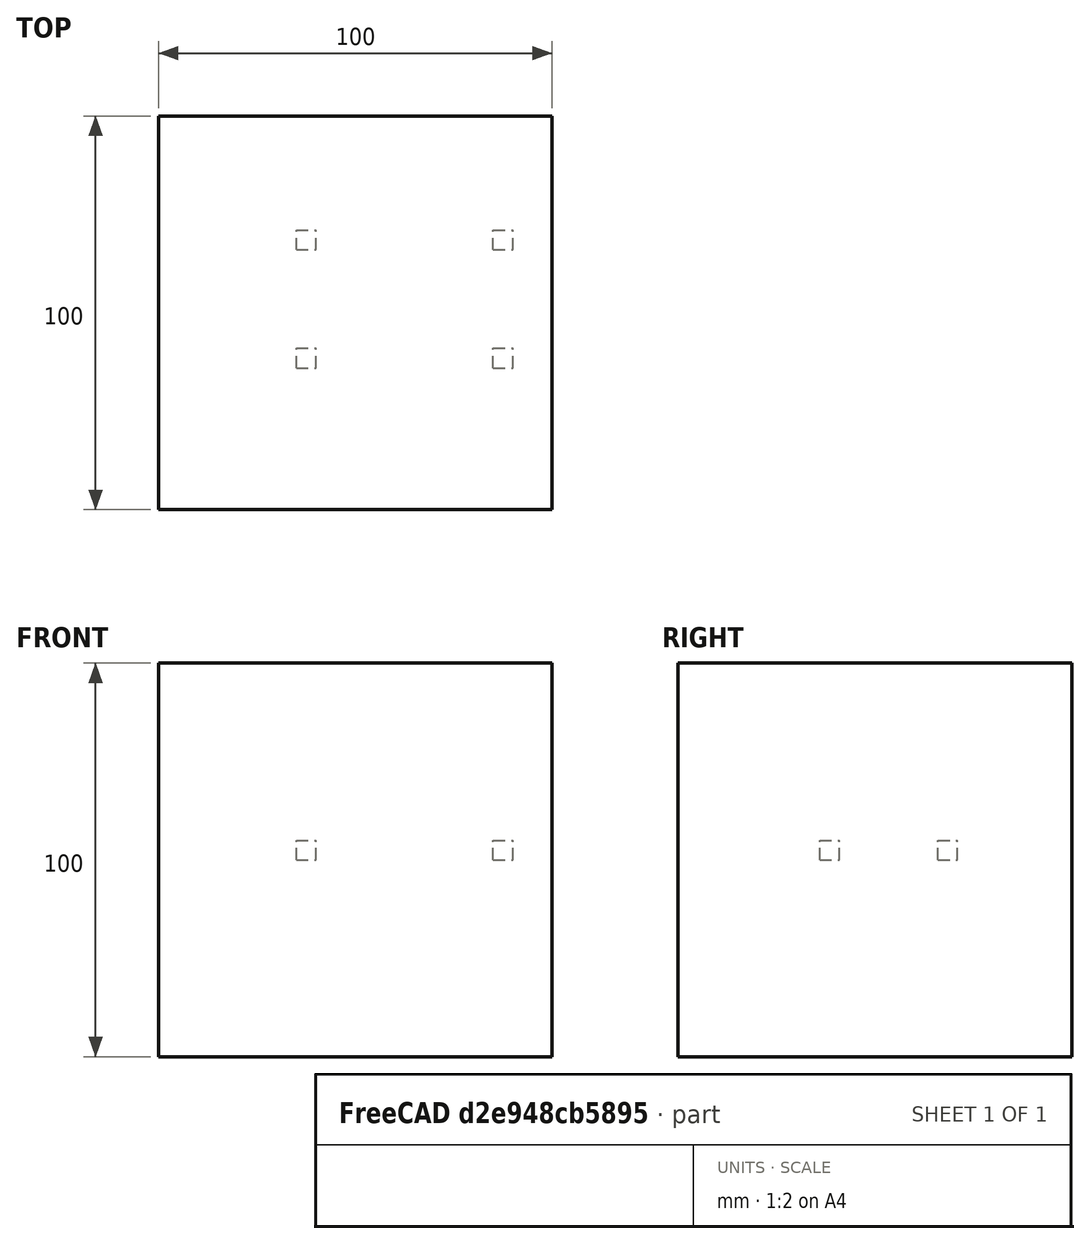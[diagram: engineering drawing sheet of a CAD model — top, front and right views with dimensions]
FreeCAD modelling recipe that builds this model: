
FCSTD DOCUMENT  (FreeCAD 1.0R39109 (Git))
Label: arrayTest-3
License: All rights reserved
LicenseURL: http://en.wikipedia.org/wiki/All_rights_reserved
objects: App::DocumentObjectGroupPython×1248, Part::FeaturePython×2, App::Part×2, Part::Box×1
note: 3 computed .brp shape members not serialized (recipe doc carries the construction recipe); baked Part::Feature solids carry a one-line shape summary decoded from their .brp

FEATURE [App::DocumentObjectGroupPython] HALFPI  # scripted group (container) (typed FeaturePython)
  name = HALFPI
  value = pi/2.
FEATURE [App::DocumentObjectGroupPython] PI  # scripted group (container) (typed FeaturePython)
  name = PI
  value = 1.*pi
FEATURE [App::DocumentObjectGroupPython] TWOPI  # scripted group (container) (typed FeaturePython)
  name = TWOPI
  value = 2.*pi
FEATURE [App::DocumentObjectGroupPython] Constants  # scripted group (container) (typed FeaturePython)
  Group = -> [HALFPI,PI,TWOPI]
FEATURE [App::DocumentObjectGroupPython] Variables  # scripted group (container) (typed FeaturePython)
FEATURE [App::DocumentObjectGroupPython] Quantities  # scripted group (container) (typed FeaturePython)
FEATURE [App::DocumentObjectGroupPython] Isotopes  # scripted group (container) (typed FeaturePython)
FEATURE [App::DocumentObjectGroupPython] Elements  # scripted group (container) (typed FeaturePython)
FEATURE [App::DocumentObjectGroupPython] G4Isotopes  # scripted group (container) (typed FeaturePython)
FEATURE [App::DocumentObjectGroupPython] H_element  # scripted group (container) (typed FeaturePython)
  Z = 1
  atom_value = 1.008
  formula = H
  name = H_element
FEATURE [App::DocumentObjectGroupPython] He_element  # scripted group (container) (typed FeaturePython)
  Z = 2
  atom_value = 4.0026
  formula = He
  name = He_element
FEATURE [App::DocumentObjectGroupPython] Li_element  # scripted group (container) (typed FeaturePython)
  Z = 3
  atom_value = 6.94
  formula = Li
  name = Li_element
FEATURE [App::DocumentObjectGroupPython] Be_element  # scripted group (container) (typed FeaturePython)
  Z = 4
  atom_value = 9.01218
  formula = Be
  name = Be_element
FEATURE [App::DocumentObjectGroupPython] B_element  # scripted group (container) (typed FeaturePython)
  Z = 5
  atom_value = 10.81
  formula = B
  name = B_element
FEATURE [App::DocumentObjectGroupPython] C_element  # scripted group (container) (typed FeaturePython)
  Z = 6
  atom_value = 12.011
  formula = C
  name = C_element
FEATURE [App::DocumentObjectGroupPython] N_element  # scripted group (container) (typed FeaturePython)
  Z = 7
  atom_value = 14.007
  formula = N
  name = N_element
FEATURE [App::DocumentObjectGroupPython] O_element  # scripted group (container) (typed FeaturePython)
  Z = 8
  atom_value = 15.999
  formula = O
  name = O_element
FEATURE [App::DocumentObjectGroupPython] F_element  # scripted group (container) (typed FeaturePython)
  Z = 9
  atom_value = 18.9984
  formula = F
  name = F_element
FEATURE [App::DocumentObjectGroupPython] Ne_element  # scripted group (container) (typed FeaturePython)
  Z = 10
  atom_value = 20.1797
  formula = Ne
  name = Ne_element
FEATURE [App::DocumentObjectGroupPython] Na_element  # scripted group (container) (typed FeaturePython)
  Z = 11
  atom_value = 22.9898
  formula = Na
  name = Na_element
FEATURE [App::DocumentObjectGroupPython] Mg_element  # scripted group (container) (typed FeaturePython)
  Z = 12
  atom_value = 24.305
  formula = Mg
  name = Mg_element
FEATURE [App::DocumentObjectGroupPython] Al_element  # scripted group (container) (typed FeaturePython)
  Z = 13
  atom_value = 26.9815
  formula = Al
  name = Al_element
FEATURE [App::DocumentObjectGroupPython] Si_element  # scripted group (container) (typed FeaturePython)
  Z = 14
  atom_value = 28.085
  formula = Si
  name = Si_element
FEATURE [App::DocumentObjectGroupPython] P_element  # scripted group (container) (typed FeaturePython)
  Z = 15
  atom_value = 30.9738
  formula = P
  name = P_element
FEATURE [App::DocumentObjectGroupPython] S_element  # scripted group (container) (typed FeaturePython)
  Z = 16
  atom_value = 32.06
  formula = S
  name = S_element
FEATURE [App::DocumentObjectGroupPython] Cl_element  # scripted group (container) (typed FeaturePython)
  Z = 17
  atom_value = 35.45
  formula = Cl
  name = Cl_element
FEATURE [App::DocumentObjectGroupPython] Ar_element  # scripted group (container) (typed FeaturePython)
  Z = 18
  atom_value = 39.95
  formula = Ar
  name = Ar_element
FEATURE [App::DocumentObjectGroupPython] K_element  # scripted group (container) (typed FeaturePython)
  Z = 19
  atom_value = 39.0983
  formula = K
  name = K_element
FEATURE [App::DocumentObjectGroupPython] Ca_element  # scripted group (container) (typed FeaturePython)
  Z = 20
  atom_value = 40.078
  formula = Ca
  name = Ca_element
FEATURE [App::DocumentObjectGroupPython] Sc_element  # scripted group (container) (typed FeaturePython)
  Z = 21
  atom_value = 44.9559
  formula = Sc
  name = Sc_element
FEATURE [App::DocumentObjectGroupPython] Ti_element  # scripted group (container) (typed FeaturePython)
  Z = 22
  atom_value = 47.867
  formula = Ti
  name = Ti_element
FEATURE [App::DocumentObjectGroupPython] V_element  # scripted group (container) (typed FeaturePython)
  Z = 23
  atom_value = 50.9415
  formula = V
  name = V_element
FEATURE [App::DocumentObjectGroupPython] Cr_element  # scripted group (container) (typed FeaturePython)
  Z = 24
  atom_value = 51.9961
  formula = Cr
  name = Cr_element
FEATURE [App::DocumentObjectGroupPython] Mn_element  # scripted group (container) (typed FeaturePython)
  Z = 25
  atom_value = 54.938
  formula = Mn
  name = Mn_element
FEATURE [App::DocumentObjectGroupPython] Fe_element  # scripted group (container) (typed FeaturePython)
  Z = 26
  atom_value = 55.845
  formula = Fe
  name = Fe_element
FEATURE [App::DocumentObjectGroupPython] Co_element  # scripted group (container) (typed FeaturePython)
  Z = 27
  atom_value = 58.9332
  formula = Co
  name = Co_element
FEATURE [App::DocumentObjectGroupPython] Ni_element  # scripted group (container) (typed FeaturePython)
  Z = 28
  atom_value = 58.6934
  formula = Ni
  name = Ni_element
FEATURE [App::DocumentObjectGroupPython] Cu_element  # scripted group (container) (typed FeaturePython)
  Z = 29
  atom_value = 63.546
  formula = Cu
  name = Cu_element
FEATURE [App::DocumentObjectGroupPython] Zn_element  # scripted group (container) (typed FeaturePython)
  Z = 30
  atom_value = 65.38
  formula = Zn
  name = Zn_element
FEATURE [App::DocumentObjectGroupPython] Ga_element  # scripted group (container) (typed FeaturePython)
  Z = 31
  atom_value = 69.723
  formula = Ga
  name = Ga_element
FEATURE [App::DocumentObjectGroupPython] Ge_element  # scripted group (container) (typed FeaturePython)
  Z = 32
  atom_value = 72.63
  formula = Ge
  name = Ge_element
FEATURE [App::DocumentObjectGroupPython] As_element  # scripted group (container) (typed FeaturePython)
  Z = 33
  atom_value = 74.9216
  formula = As
  name = As_element
FEATURE [App::DocumentObjectGroupPython] Se_element  # scripted group (container) (typed FeaturePython)
  Z = 34
  atom_value = 78.971
  formula = Se
  name = Se_element
FEATURE [App::DocumentObjectGroupPython] Br_element  # scripted group (container) (typed FeaturePython)
  Z = 35
  atom_value = 79.904
  formula = Br
  name = Br_element
FEATURE [App::DocumentObjectGroupPython] Kr_element  # scripted group (container) (typed FeaturePython)
  Z = 36
  atom_value = 83.798
  formula = Kr
  name = Kr_element
FEATURE [App::DocumentObjectGroupPython] Rb_element  # scripted group (container) (typed FeaturePython)
  Z = 37
  atom_value = 85.4678
  formula = Rb
  name = Rb_element
FEATURE [App::DocumentObjectGroupPython] Sr_element  # scripted group (container) (typed FeaturePython)
  Z = 38
  atom_value = 87.62
  formula = Sr
  name = Sr_element
FEATURE [App::DocumentObjectGroupPython] Y_element  # scripted group (container) (typed FeaturePython)
  Z = 39
  atom_value = 88.9058
  formula = Y
  name = Y_element
FEATURE [App::DocumentObjectGroupPython] Zr_element  # scripted group (container) (typed FeaturePython)
  Z = 40
  atom_value = 91.224
  formula = Zr
  name = Zr_element
FEATURE [App::DocumentObjectGroupPython] Nb_element  # scripted group (container) (typed FeaturePython)
  Z = 41
  atom_value = 92.9064
  formula = Nb
  name = Nb_element
FEATURE [App::DocumentObjectGroupPython] Mo_element  # scripted group (container) (typed FeaturePython)
  Z = 42
  atom_value = 95.95
  formula = Mo
  name = Mo_element
FEATURE [App::DocumentObjectGroupPython] Tc_element  # scripted group (container) (typed FeaturePython)
  Z = 43
  atom_value = 97
  formula = Tc
  name = Tc_element
FEATURE [App::DocumentObjectGroupPython] Ru_element  # scripted group (container) (typed FeaturePython)
  Z = 44
  atom_value = 101.07
  formula = Ru
  name = Ru_element
FEATURE [App::DocumentObjectGroupPython] Rh_element  # scripted group (container) (typed FeaturePython)
  Z = 45
  atom_value = 102.905
  formula = Rh
  name = Rh_element
FEATURE [App::DocumentObjectGroupPython] Pd_element  # scripted group (container) (typed FeaturePython)
  Z = 46
  atom_value = 106.42
  formula = Pd
  name = Pd_element
FEATURE [App::DocumentObjectGroupPython] Ag_element  # scripted group (container) (typed FeaturePython)
  Z = 47
  atom_value = 107.868
  formula = Ag
  name = Ag_element
FEATURE [App::DocumentObjectGroupPython] Cd_element  # scripted group (container) (typed FeaturePython)
  Z = 48
  atom_value = 112.414
  formula = Cd
  name = Cd_element
FEATURE [App::DocumentObjectGroupPython] In_element  # scripted group (container) (typed FeaturePython)
  Z = 49
  atom_value = 114.818
  formula = In
  name = In_element
FEATURE [App::DocumentObjectGroupPython] Sn_element  # scripted group (container) (typed FeaturePython)
  Z = 50
  atom_value = 118.71
  formula = Sn
  name = Sn_element
FEATURE [App::DocumentObjectGroupPython] Sb_element  # scripted group (container) (typed FeaturePython)
  Z = 51
  atom_value = 121.76
  formula = Sb
  name = Sb_element
FEATURE [App::DocumentObjectGroupPython] Te_element  # scripted group (container) (typed FeaturePython)
  Z = 52
  atom_value = 127.6
  formula = Te
  name = Te_element
FEATURE [App::DocumentObjectGroupPython] I_element  # scripted group (container) (typed FeaturePython)
  Z = 53
  atom_value = 126.904
  formula = I
  name = I_element
FEATURE [App::DocumentObjectGroupPython] Xe_element  # scripted group (container) (typed FeaturePython)
  Z = 54
  atom_value = 131.293
  formula = Xe
  name = Xe_element
FEATURE [App::DocumentObjectGroupPython] Cs_element  # scripted group (container) (typed FeaturePython)
  Z = 55
  atom_value = 132.905
  formula = Cs
  name = Cs_element
FEATURE [App::DocumentObjectGroupPython] Ba_element  # scripted group (container) (typed FeaturePython)
  Z = 56
  atom_value = 137.327
  formula = Ba
  name = Ba_element
FEATURE [App::DocumentObjectGroupPython] La_element  # scripted group (container) (typed FeaturePython)
  Z = 57
  atom_value = 138.905
  formula = La
  name = La_element
FEATURE [App::DocumentObjectGroupPython] Ce_element  # scripted group (container) (typed FeaturePython)
  Z = 58
  atom_value = 140.116
  formula = Ce
  name = Ce_element
FEATURE [App::DocumentObjectGroupPython] Pr_element  # scripted group (container) (typed FeaturePython)
  Z = 59
  atom_value = 140.908
  formula = Pr
  name = Pr_element
FEATURE [App::DocumentObjectGroupPython] Nd_element  # scripted group (container) (typed FeaturePython)
  Z = 60
  atom_value = 144.242
  formula = Nd
  name = Nd_element
FEATURE [App::DocumentObjectGroupPython] Pm_element  # scripted group (container) (typed FeaturePython)
  Z = 61
  atom_value = 145
  formula = Pm
  name = Pm_element
FEATURE [App::DocumentObjectGroupPython] Sm_element  # scripted group (container) (typed FeaturePython)
  Z = 62
  atom_value = 150.36
  formula = Sm
  name = Sm_element
FEATURE [App::DocumentObjectGroupPython] Eu_element  # scripted group (container) (typed FeaturePython)
  Z = 63
  atom_value = 151.964
  formula = Eu
  name = Eu_element
FEATURE [App::DocumentObjectGroupPython] Gd_element  # scripted group (container) (typed FeaturePython)
  Z = 64
  atom_value = 157.25
  formula = Gd
  name = Gd_element
FEATURE [App::DocumentObjectGroupPython] Tb_element  # scripted group (container) (typed FeaturePython)
  Z = 65
  atom_value = 158.925
  formula = Tb
  name = Tb_element
FEATURE [App::DocumentObjectGroupPython] Dy_element  # scripted group (container) (typed FeaturePython)
  Z = 66
  atom_value = 162.5
  formula = Dy
  name = Dy_element
FEATURE [App::DocumentObjectGroupPython] Ho_element  # scripted group (container) (typed FeaturePython)
  Z = 67
  atom_value = 164.93
  formula = Ho
  name = Ho_element
FEATURE [App::DocumentObjectGroupPython] Er_element  # scripted group (container) (typed FeaturePython)
  Z = 68
  atom_value = 167.259
  formula = Er
  name = Er_element
FEATURE [App::DocumentObjectGroupPython] Tm_element  # scripted group (container) (typed FeaturePython)
  Z = 69
  atom_value = 168.934
  formula = Tm
  name = Tm_element
FEATURE [App::DocumentObjectGroupPython] Yb_element  # scripted group (container) (typed FeaturePython)
  Z = 70
  atom_value = 173.045
  formula = Yb
  name = Yb_element
FEATURE [App::DocumentObjectGroupPython] Lu_element  # scripted group (container) (typed FeaturePython)
  Z = 71
  atom_value = 174.967
  formula = Lu
  name = Lu_element
FEATURE [App::DocumentObjectGroupPython] Hf_element  # scripted group (container) (typed FeaturePython)
  Z = 72
  atom_value = 178.49
  formula = Hf
  name = Hf_element
FEATURE [App::DocumentObjectGroupPython] Ta_element  # scripted group (container) (typed FeaturePython)
  Z = 73
  atom_value = 180.948
  formula = Ta
  name = Ta_element
FEATURE [App::DocumentObjectGroupPython] W_element  # scripted group (container) (typed FeaturePython)
  Z = 74
  atom_value = 183.84
  formula = W
  name = W_element
FEATURE [App::DocumentObjectGroupPython] Re_element  # scripted group (container) (typed FeaturePython)
  Z = 75
  atom_value = 186.207
  formula = Re
  name = Re_element
FEATURE [App::DocumentObjectGroupPython] Os_element  # scripted group (container) (typed FeaturePython)
  Z = 76
  atom_value = 190.23
  formula = Os
  name = Os_element
FEATURE [App::DocumentObjectGroupPython] Ir_element  # scripted group (container) (typed FeaturePython)
  Z = 77
  atom_value = 192.217
  formula = Ir
  name = Ir_element
FEATURE [App::DocumentObjectGroupPython] Pt_element  # scripted group (container) (typed FeaturePython)
  Z = 78
  atom_value = 195.084
  formula = Pt
  name = Pt_element
FEATURE [App::DocumentObjectGroupPython] Au_element  # scripted group (container) (typed FeaturePython)
  Z = 79
  atom_value = 196.967
  formula = Au
  name = Au_element
FEATURE [App::DocumentObjectGroupPython] Hg_element  # scripted group (container) (typed FeaturePython)
  Z = 80
  atom_value = 200.592
  formula = Hg
  name = Hg_element
FEATURE [App::DocumentObjectGroupPython] Tl_element  # scripted group (container) (typed FeaturePython)
  Z = 81
  atom_value = 204.38
  formula = Tl
  name = Tl_element
FEATURE [App::DocumentObjectGroupPython] Pb_element  # scripted group (container) (typed FeaturePython)
  Z = 82
  atom_value = 207.2
  formula = Pb
  name = Pb_element
FEATURE [App::DocumentObjectGroupPython] Bi_element  # scripted group (container) (typed FeaturePython)
  Z = 83
  atom_value = 208.98
  formula = Bi
  name = Bi_element
FEATURE [App::DocumentObjectGroupPython] Po_element  # scripted group (container) (typed FeaturePython)
  Z = 84
  atom_value = 209
  formula = Po
  name = Po_element
FEATURE [App::DocumentObjectGroupPython] At_element  # scripted group (container) (typed FeaturePython)
  Z = 85
  atom_value = 210
  formula = At
  name = At_element
FEATURE [App::DocumentObjectGroupPython] Rn_element  # scripted group (container) (typed FeaturePython)
  Z = 86
  atom_value = 222
  formula = Rn
  name = Rn_element
FEATURE [App::DocumentObjectGroupPython] Fr_element  # scripted group (container) (typed FeaturePython)
  Z = 87
  atom_value = 223
  formula = Fr
  name = Fr_element
FEATURE [App::DocumentObjectGroupPython] Ra_element  # scripted group (container) (typed FeaturePython)
  Z = 88
  atom_value = 226
  formula = Ra
  name = Ra_element
FEATURE [App::DocumentObjectGroupPython] Ac_element  # scripted group (container) (typed FeaturePython)
  Z = 89
  atom_value = 227
  formula = Ac
  name = Ac_element
FEATURE [App::DocumentObjectGroupPython] Th_element  # scripted group (container) (typed FeaturePython)
  Z = 90
  atom_value = 232.038
  formula = Th
  name = Th_element
FEATURE [App::DocumentObjectGroupPython] Pa_element  # scripted group (container) (typed FeaturePython)
  Z = 91
  atom_value = 231.036
  formula = Pa
  name = Pa_element
FEATURE [App::DocumentObjectGroupPython] U_element  # scripted group (container) (typed FeaturePython)
  Z = 92
  atom_value = 238.029
  formula = U
  name = U_element
FEATURE [App::DocumentObjectGroupPython] Np_element  # scripted group (container) (typed FeaturePython)
  Z = 93
  atom_value = 237
  formula = Np
  name = Np_element
FEATURE [App::DocumentObjectGroupPython] Pu_element  # scripted group (container) (typed FeaturePython)
  Z = 94
  atom_value = 244
  formula = Pu
  name = Pu_element
FEATURE [App::DocumentObjectGroupPython] Am_element  # scripted group (container) (typed FeaturePython)
  Z = 95
  atom_value = 243
  formula = Am
  name = Am_element
FEATURE [App::DocumentObjectGroupPython] Cm_element  # scripted group (container) (typed FeaturePython)
  Z = 96
  atom_value = 247
  formula = Cm
  name = Cm_element
FEATURE [App::DocumentObjectGroupPython] Bk_element  # scripted group (container) (typed FeaturePython)
  Z = 97
  atom_value = 247
  formula = Bk
  name = Bk_element
FEATURE [App::DocumentObjectGroupPython] Cf_element  # scripted group (container) (typed FeaturePython)
  Z = 98
  atom_value = 251
  formula = Cf
  name = Cf_element
FEATURE [App::DocumentObjectGroupPython] G4Elements  # scripted group (container) (typed FeaturePython)
  Group = -> [H_element,He_element,Li_element,Be_element,B_element,C_element,N_element,O_element,F_element,Ne_element,Na_element,Mg_element,Al_element,Si_element,P_element,S_element,Cl_element,Ar_element,K_element,Ca_element,Sc_element,Ti_element,V_element,Cr_element,Mn_element,Fe_element,Co_element,Ni_element,Cu_element,Zn_element,Ga_element,Ge_element,As_element,Se_element,Br_element,Kr_element,Rb_element,+61 more]
FEATURE [App::DocumentObjectGroupPython] H_element001  label="H_element : 0.101"  # scripted group (container) (typed FeaturePython)
  n = 0.101327
FEATURE [App::DocumentObjectGroupPython] C_element001  label="C_element : 0.775"  # scripted group (container) (typed FeaturePython)
  n = 0.7755
FEATURE [App::DocumentObjectGroupPython] N_element001  label="N_element : 0.035"  # scripted group (container) (typed FeaturePython)
  n = 0.035057
FEATURE [App::DocumentObjectGroupPython] O_element001  label="O_element : 0.052"  # scripted group (container) (typed FeaturePython)
  n = 0.0523159
FEATURE [App::DocumentObjectGroupPython] F_element001  label="F_element : 0.017"  # scripted group (container) (typed FeaturePython)
  n = 0.017422
FEATURE [App::DocumentObjectGroupPython] Ca_element001  label="Ca_element : 0.018"  # scripted group (container) (typed FeaturePython)
  n = 0.018378
FEATURE [App::DocumentObjectGroupPython] G4_A_150_TISSUE  label="G4_A-150_TISSUE"  # scripted group (container) (typed FeaturePython)
  Dunit = g/cm3
  Dvalue = 1.127
  Group = -> [H_element001,C_element001,N_element001,O_element001,F_element001,Ca_element001]
  conduct = 2
  density = 1
  expand = 3
  formula = G4_A-150_TISSUE
  name = G4_A-150_TISSUE
  specific = 4
FEATURE [App::DocumentObjectGroupPython] C_element002  label="C_element : 3"  # scripted group (container) (typed FeaturePython)
  n = 3
  ref = C_element
FEATURE [App::DocumentObjectGroupPython] H_element002  label="H_element : 6"  # scripted group (container) (typed FeaturePython)
  n = 6
  ref = H_element
FEATURE [App::DocumentObjectGroupPython] O_element002  label="O_element : 1"  # scripted group (container) (typed FeaturePython)
  n = 1
  ref = O_element
FEATURE [App::DocumentObjectGroupPython] G4_ACETONE  # scripted group (container) (typed FeaturePython)
  Dunit = g/cm3
  Dvalue = 0.7899
  Group = -> [C_element002,H_element002,O_element002]
  conduct = 2
  density = 1
  expand = 3
  formula = G4_ACETONE
  name = G4_ACETONE
  specific = 4
FEATURE [App::DocumentObjectGroupPython] C_element003  label="C_element : 2"  # scripted group (container) (typed FeaturePython)
  n = 2
  ref = C_element
FEATURE [App::DocumentObjectGroupPython] H_element003  label="H_element : 2"  # scripted group (container) (typed FeaturePython)
  n = 2
  ref = H_element
FEATURE [App::DocumentObjectGroupPython] G4_ACETYLENE  # scripted group (container) (typed FeaturePython)
  Dunit = g/cm3
  Dvalue = 0.0010967
  Group = -> [C_element003,H_element003]
  conduct = 2
  density = 1
  expand = 3
  formula = G4_ACETYLENE
  name = G4_ACETYLENE
  specific = 4
FEATURE [App::DocumentObjectGroupPython] C_element004  label="C_element : 5"  # scripted group (container) (typed FeaturePython)
  n = 5
  ref = C_element
FEATURE [App::DocumentObjectGroupPython] H_element004  label="H_element : 5"  # scripted group (container) (typed FeaturePython)
  n = 5
  ref = H_element
FEATURE [App::DocumentObjectGroupPython] N_element002  label="N_element : 5"  # scripted group (container) (typed FeaturePython)
  n = 5
  ref = N_element
FEATURE [App::DocumentObjectGroupPython] G4_ADENINE  # scripted group (container) (typed FeaturePython)
  Dunit = g/cm3
  Dvalue = 1.6
  Group = -> [C_element004,H_element004,N_element002]
  conduct = 2
  density = 1
  expand = 3
  formula = G4_ADENINE
  name = G4_ADENINE
  specific = 4
FEATURE [App::DocumentObjectGroupPython] H_element005  label="H_element : 0.114"  # scripted group (container) (typed FeaturePython)
  n = 0.114
FEATURE [App::DocumentObjectGroupPython] C_element005  label="C_element : 0.598"  # scripted group (container) (typed FeaturePython)
  n = 0.598
FEATURE [App::DocumentObjectGroupPython] N_element003  label="N_element : 0.007"  # scripted group (container) (typed FeaturePython)
  n = 0.007
FEATURE [App::DocumentObjectGroupPython] O_element003  label="O_element : 0.278"  # scripted group (container) (typed FeaturePython)
  n = 0.278
FEATURE [App::DocumentObjectGroupPython] Na_element001  label="Na_element : 0.001"  # scripted group (container) (typed FeaturePython)
  n = 0.001
FEATURE [App::DocumentObjectGroupPython] S_element001  label="S_element : 0.001"  # scripted group (container) (typed FeaturePython)
  n = 0.001
FEATURE [App::DocumentObjectGroupPython] Cl_element001  label="Cl_element : 0.001"  # scripted group (container) (typed FeaturePython)
  n = 0.001
FEATURE [App::DocumentObjectGroupPython] G4_ADIPOSE_TISSUE_ICRP  # scripted group (container) (typed FeaturePython)
  Dunit = g/cm3
  Dvalue = 0.95
  Group = -> [H_element005,C_element005,N_element003,O_element003,Na_element001,S_element001,Cl_element001]
  conduct = 2
  density = 1
  expand = 3
  formula = G4_ADIPOSE_TISSUE_ICRP
  name = G4_ADIPOSE_TISSUE_ICRP
  specific = 4
FEATURE [App::DocumentObjectGroupPython] C_element006  label="C_element : 0.000"  # scripted group (container) (typed FeaturePython)
  n = 0.000124
FEATURE [App::DocumentObjectGroupPython] N_element004  label="N_element : 0.755"  # scripted group (container) (typed FeaturePython)
  n = 0.755268
FEATURE [App::DocumentObjectGroupPython] O_element004  label="O_element : 0.232"  # scripted group (container) (typed FeaturePython)
  n = 0.231781
FEATURE [App::DocumentObjectGroupPython] Ar_element001  label="Ar_element : 0.013"  # scripted group (container) (typed FeaturePython)
  n = 0.012827
FEATURE [App::DocumentObjectGroupPython] G4_AIR  # scripted group (container) (typed FeaturePython)
  Dunit = g/cm3
  Dvalue = 0.00120479
  Group = -> [C_element006,N_element004,O_element004,Ar_element001]
  conduct = 2
  density = 1
  expand = 3
  formula = G4_AIR
  name = G4_AIR
  specific = 4
FEATURE [App::DocumentObjectGroupPython] C_element007  label="C_element : 006"  # scripted group (container) (typed FeaturePython)
  n = 3
  ref = C_element
FEATURE [App::DocumentObjectGroupPython] H_element006  label="H_element : 7"  # scripted group (container) (typed FeaturePython)
  n = 7
  ref = H_element
FEATURE [App::DocumentObjectGroupPython] N_element005  label="N_element : 1"  # scripted group (container) (typed FeaturePython)
  n = 1
  ref = N_element
FEATURE [App::DocumentObjectGroupPython] O_element005  label="O_element : 2"  # scripted group (container) (typed FeaturePython)
  n = 2
  ref = O_element
FEATURE [App::DocumentObjectGroupPython] G4_ALANINE  # scripted group (container) (typed FeaturePython)
  Dunit = g/cm3
  Dvalue = 1.42
  Group = -> [C_element007,H_element006,N_element005,O_element005]
  conduct = 2
  density = 1
  expand = 3
  formula = G4_ALANINE
  name = G4_ALANINE
  specific = 4
FEATURE [App::DocumentObjectGroupPython] Al_element001  label="Al_element : 2"  # scripted group (container) (typed FeaturePython)
  n = 2
  ref = Al_element
FEATURE [App::DocumentObjectGroupPython] O_element006  label="O_element : 3"  # scripted group (container) (typed FeaturePython)
  n = 3
  ref = O_element
FEATURE [App::DocumentObjectGroupPython] G4_ALUMINUM_OXIDE  # scripted group (container) (typed FeaturePython)
  Dunit = g/cm3
  Dvalue = 3.97
  Group = -> [Al_element001,O_element006]
  conduct = 2
  density = 1
  expand = 3
  formula = G4_ALUMINUM_OXIDE
  name = G4_ALUMINUM_OXIDE
  specific = 4
FEATURE [App::DocumentObjectGroupPython] H_element007  label="H_element : 0.106"  # scripted group (container) (typed FeaturePython)
  n = 0.10593
FEATURE [App::DocumentObjectGroupPython] C_element008  label="C_element : 0.789"  # scripted group (container) (typed FeaturePython)
  n = 0.788974
FEATURE [App::DocumentObjectGroupPython] O_element007  label="O_element : 0.105"  # scripted group (container) (typed FeaturePython)
  n = 0.105096
FEATURE [App::DocumentObjectGroupPython] G4_AMBER  # scripted group (container) (typed FeaturePython)
  Dunit = g/cm3
  Dvalue = 1.1
  Group = -> [H_element007,C_element008,O_element007]
  conduct = 2
  density = 1
  expand = 3
  formula = G4_AMBER
  name = G4_AMBER
  specific = 4
FEATURE [App::DocumentObjectGroupPython] N_element006  label="N_element : 006"  # scripted group (container) (typed FeaturePython)
  n = 1
  ref = N_element
FEATURE [App::DocumentObjectGroupPython] H_element008  label="H_element : 3"  # scripted group (container) (typed FeaturePython)
  n = 3
  ref = H_element
FEATURE [App::DocumentObjectGroupPython] G4_AMMONIA  # scripted group (container) (typed FeaturePython)
  Dunit = g/cm3
  Dvalue = 0.000826019
  Group = -> [N_element006,H_element008]
  conduct = 2
  density = 1
  expand = 3
  formula = G4_AMMONIA
  name = G4_AMMONIA
  specific = 4
FEATURE [App::DocumentObjectGroupPython] C_element009  label="C_element : 6"  # scripted group (container) (typed FeaturePython)
  n = 6
  ref = C_element
FEATURE [App::DocumentObjectGroupPython] H_element009  label="H_element : 008"  # scripted group (container) (typed FeaturePython)
  n = 7
  ref = H_element
FEATURE [App::DocumentObjectGroupPython] N_element007  label="N_element : 007"  # scripted group (container) (typed FeaturePython)
  n = 1
  ref = N_element
FEATURE [App::DocumentObjectGroupPython] G4_ANILINE  # scripted group (container) (typed FeaturePython)
  Dunit = g/cm3
  Dvalue = 1.0235
  Group = -> [C_element009,H_element009,N_element007]
  conduct = 2
  density = 1
  expand = 3
  formula = G4_ANILINE
  name = G4_ANILINE
  specific = 4
FEATURE [App::DocumentObjectGroupPython] C_element010  label="C_element : 14"  # scripted group (container) (typed FeaturePython)
  n = 14
  ref = C_element
FEATURE [App::DocumentObjectGroupPython] H_element010  label="H_element : 10"  # scripted group (container) (typed FeaturePython)
  n = 10
  ref = H_element
FEATURE [App::DocumentObjectGroupPython] G4_ANTHRACENE  # scripted group (container) (typed FeaturePython)
  Dunit = g/cm3
  Dvalue = 1.283
  Group = -> [C_element010,H_element010]
  conduct = 2
  density = 1
  expand = 3
  formula = G4_ANTHRACENE
  name = G4_ANTHRACENE
  specific = 4
FEATURE [App::DocumentObjectGroupPython] H_element011  label="H_element : 0.065"  # scripted group (container) (typed FeaturePython)
  n = 0.0654709
FEATURE [App::DocumentObjectGroupPython] C_element011  label="C_element : 0.537"  # scripted group (container) (typed FeaturePython)
  n = 0.536944
FEATURE [App::DocumentObjectGroupPython] N_element008  label="N_element : 0.021"  # scripted group (container) (typed FeaturePython)
  n = 0.0215
FEATURE [App::DocumentObjectGroupPython] O_element008  label="O_element : 0.032"  # scripted group (container) (typed FeaturePython)
  n = 0.032085
FEATURE [App::DocumentObjectGroupPython] F_element002  label="F_element : 0.167"  # scripted group (container) (typed FeaturePython)
  n = 0.167411
FEATURE [App::DocumentObjectGroupPython] Ca_element002  label="Ca_element : 0.177"  # scripted group (container) (typed FeaturePython)
  n = 0.176589
FEATURE [App::DocumentObjectGroupPython] G4_B_100_BONE  label="G4_B-100_BONE"  # scripted group (container) (typed FeaturePython)
  Dunit = g/cm3
  Dvalue = 1.45
  Group = -> [H_element011,C_element011,N_element008,O_element008,F_element002,Ca_element002]
  conduct = 2
  density = 1
  expand = 3
  formula = G4_B-100_BONE
  name = G4_B-100_BONE
  specific = 4
FEATURE [App::DocumentObjectGroupPython] H_element012  label="H_element : 0.057"  # scripted group (container) (typed FeaturePython)
  n = 0.057441
FEATURE [App::DocumentObjectGroupPython] C_element012  label="C_element : 0.790"  # scripted group (container) (typed FeaturePython)
  n = 0.774591
FEATURE [App::DocumentObjectGroupPython] O_element009  label="O_element : 0.168"  # scripted group (container) (typed FeaturePython)
  n = 0.167968
FEATURE [App::DocumentObjectGroupPython] G4_BAKELITE  # scripted group (container) (typed FeaturePython)
  Dunit = g/cm3
  Dvalue = 1.25
  Group = -> [H_element012,C_element012,O_element009]
  conduct = 2
  density = 1
  expand = 3
  formula = G4_BAKELITE
  name = G4_BAKELITE
  specific = 4
FEATURE [App::DocumentObjectGroupPython] Ba_element001  label="Ba_element : 1"  # scripted group (container) (typed FeaturePython)
  n = 1
  ref = Ba_element
FEATURE [App::DocumentObjectGroupPython] F_element003  label="F_element : 2"  # scripted group (container) (typed FeaturePython)
  n = 2
  ref = F_element
FEATURE [App::DocumentObjectGroupPython] G4_BARIUM_FLUORIDE  # scripted group (container) (typed FeaturePython)
  Dunit = g/cm3
  Dvalue = 4.89
  Group = -> [Ba_element001,F_element003]
  conduct = 2
  density = 1
  expand = 3
  formula = G4_BARIUM_FLUORIDE
  name = G4_BARIUM_FLUORIDE
  specific = 4
FEATURE [App::DocumentObjectGroupPython] Ba_element002  label="Ba_element : 002"  # scripted group (container) (typed FeaturePython)
  n = 1
  ref = Ba_element
FEATURE [App::DocumentObjectGroupPython] S_element002  label="S_element : 1"  # scripted group (container) (typed FeaturePython)
  n = 1
  ref = S_element
FEATURE [App::DocumentObjectGroupPython] O_element010  label="O_element : 4"  # scripted group (container) (typed FeaturePython)
  n = 4
  ref = O_element
FEATURE [App::DocumentObjectGroupPython] G4_BARIUM_SULFATE  # scripted group (container) (typed FeaturePython)
  Dunit = g/cm3
  Dvalue = 4.5
  Group = -> [Ba_element002,S_element002,O_element010]
  conduct = 2
  density = 1
  expand = 3
  formula = G4_BARIUM_SULFATE
  name = G4_BARIUM_SULFATE
  specific = 4
FEATURE [App::DocumentObjectGroupPython] C_element013  label="C_element : 007"  # scripted group (container) (typed FeaturePython)
  n = 6
  ref = C_element
FEATURE [App::DocumentObjectGroupPython] H_element013  label="H_element : 009"  # scripted group (container) (typed FeaturePython)
  n = 6
  ref = H_element
FEATURE [App::DocumentObjectGroupPython] G4_BENZENE  # scripted group (container) (typed FeaturePython)
  Dunit = g/cm3
  Dvalue = 0.87865
  Group = -> [C_element013,H_element013]
  conduct = 2
  density = 1
  expand = 3
  formula = G4_BENZENE
  name = G4_BENZENE
  specific = 4
FEATURE [App::DocumentObjectGroupPython] Be_element001  label="Be_element : 1"  # scripted group (container) (typed FeaturePython)
  n = 1
  ref = Be_element
FEATURE [App::DocumentObjectGroupPython] O_element011  label="O_element : 005"  # scripted group (container) (typed FeaturePython)
  n = 1
  ref = O_element
FEATURE [App::DocumentObjectGroupPython] G4_BERYLLIUM_OXIDE  # scripted group (container) (typed FeaturePython)
  Dunit = g/cm3
  Dvalue = 3.01
  Group = -> [Be_element001,O_element011]
  conduct = 2
  density = 1
  expand = 3
  formula = G4_BERYLLIUM_OXIDE
  name = G4_BERYLLIUM_OXIDE
  specific = 4
FEATURE [App::DocumentObjectGroupPython] Bi_element001  label="Bi_element : 4"  # scripted group (container) (typed FeaturePython)
  n = 4
  ref = Bi_element
FEATURE [App::DocumentObjectGroupPython] Ge_element001  label="Ge_element : 3"  # scripted group (container) (typed FeaturePython)
  n = 3
  ref = Ge_element
FEATURE [App::DocumentObjectGroupPython] O_element012  label="O_element : 12"  # scripted group (container) (typed FeaturePython)
  n = 12
  ref = O_element
FEATURE [App::DocumentObjectGroupPython] G4_BGO  # scripted group (container) (typed FeaturePython)
  Dunit = g/cm3
  Dvalue = 7.13
  Group = -> [Bi_element001,Ge_element001,O_element012]
  conduct = 2
  density = 1
  expand = 3
  formula = G4_BGO
  name = G4_BGO
  specific = 4
FEATURE [App::DocumentObjectGroupPython] H_element014  label="H_element : 0.102"  # scripted group (container) (typed FeaturePython)
  n = 0.102
FEATURE [App::DocumentObjectGroupPython] C_element014  label="C_element : 0.110"  # scripted group (container) (typed FeaturePython)
  n = 0.11
FEATURE [App::DocumentObjectGroupPython] N_element009  label="N_element : 0.033"  # scripted group (container) (typed FeaturePython)
  n = 0.033
FEATURE [App::DocumentObjectGroupPython] O_element013  label="O_element : 0.745"  # scripted group (container) (typed FeaturePython)
  n = 0.745
FEATURE [App::DocumentObjectGroupPython] Na_element002  label="Na_element : 0.002"  # scripted group (container) (typed FeaturePython)
  n = 0.001
FEATURE [App::DocumentObjectGroupPython] P_element001  label="P_element : 0.001"  # scripted group (container) (typed FeaturePython)
  n = 0.001
FEATURE [App::DocumentObjectGroupPython] S_element003  label="S_element : 0.002"  # scripted group (container) (typed FeaturePython)
  n = 0.002
FEATURE [App::DocumentObjectGroupPython] Cl_element002  label="Cl_element : 0.003"  # scripted group (container) (typed FeaturePython)
  n = 0.003
FEATURE [App::DocumentObjectGroupPython] K_element001  label="K_element : 0.002"  # scripted group (container) (typed FeaturePython)
  n = 0.002
FEATURE [App::DocumentObjectGroupPython] Fe_element001  label="Fe_element : 0.001"  # scripted group (container) (typed FeaturePython)
  n = 0.001
FEATURE [App::DocumentObjectGroupPython] G4_BLOOD_ICRP  # scripted group (container) (typed FeaturePython)
  Dunit = g/cm3
  Dvalue = 1.06
  Group = -> [H_element014,C_element014,N_element009,O_element013,Na_element002,P_element001,S_element003,Cl_element002,K_element001,Fe_element001]
  conduct = 2
  density = 1
  expand = 3
  formula = G4_BLOOD_ICRP
  name = G4_BLOOD_ICRP
  specific = 4
FEATURE [App::DocumentObjectGroupPython] H_element015  label="H_element : 0.064"  # scripted group (container) (typed FeaturePython)
  n = 0.064
FEATURE [App::DocumentObjectGroupPython] C_element015  label="C_element : 0.278"  # scripted group (container) (typed FeaturePython)
  n = 0.278
FEATURE [App::DocumentObjectGroupPython] N_element010  label="N_element : 0.027"  # scripted group (container) (typed FeaturePython)
  n = 0.027
FEATURE [App::DocumentObjectGroupPython] O_element014  label="O_element : 0.410"  # scripted group (container) (typed FeaturePython)
  n = 0.41
FEATURE [App::DocumentObjectGroupPython] Mg_element001  label="Mg_element : 0.002"  # scripted group (container) (typed FeaturePython)
  n = 0.002
FEATURE [App::DocumentObjectGroupPython] P_element002  label="P_element : 0.070"  # scripted group (container) (typed FeaturePython)
  n = 0.07
FEATURE [App::DocumentObjectGroupPython] S_element004  label="S_element : 0.003"  # scripted group (container) (typed FeaturePython)
  n = 0.002
FEATURE [App::DocumentObjectGroupPython] Ca_element003  label="Ca_element : 0.147"  # scripted group (container) (typed FeaturePython)
  n = 0.147
FEATURE [App::DocumentObjectGroupPython] G4_BONE_COMPACT_ICRU  # scripted group (container) (typed FeaturePython)
  Dunit = g/cm3
  Dvalue = 1.85
  Group = -> [H_element015,C_element015,N_element010,O_element014,Mg_element001,P_element002,S_element004,Ca_element003]
  conduct = 2
  density = 1
  expand = 3
  formula = G4_BONE_COMPACT_ICRU
  name = G4_BONE_COMPACT_ICRU
  specific = 4
FEATURE [App::DocumentObjectGroupPython] H_element016  label="H_element : 0.034"  # scripted group (container) (typed FeaturePython)
  n = 0.034
FEATURE [App::DocumentObjectGroupPython] C_element016  label="C_element : 0.155"  # scripted group (container) (typed FeaturePython)
  n = 0.155
FEATURE [App::DocumentObjectGroupPython] N_element011  label="N_element : 0.042"  # scripted group (container) (typed FeaturePython)
  n = 0.042
FEATURE [App::DocumentObjectGroupPython] O_element015  label="O_element : 0.435"  # scripted group (container) (typed FeaturePython)
  n = 0.435
FEATURE [App::DocumentObjectGroupPython] Na_element003  label="Na_element : 0.003"  # scripted group (container) (typed FeaturePython)
  n = 0.001
FEATURE [App::DocumentObjectGroupPython] Mg_element002  label="Mg_element : 0.003"  # scripted group (container) (typed FeaturePython)
  n = 0.002
FEATURE [App::DocumentObjectGroupPython] P_element003  label="P_element : 0.103"  # scripted group (container) (typed FeaturePython)
  n = 0.103
FEATURE [App::DocumentObjectGroupPython] S_element005  label="S_element : 0.004"  # scripted group (container) (typed FeaturePython)
  n = 0.003
FEATURE [App::DocumentObjectGroupPython] Ca_element004  label="Ca_element : 0.225"  # scripted group (container) (typed FeaturePython)
  n = 0.225
FEATURE [App::DocumentObjectGroupPython] G4_BONE_CORTICAL_ICRP  # scripted group (container) (typed FeaturePython)
  Dunit = g/cm3
  Dvalue = 1.92
  Group = -> [H_element016,C_element016,N_element011,O_element015,Na_element003,Mg_element002,P_element003,S_element005,Ca_element004]
  conduct = 2
  density = 1
  expand = 3
  formula = G4_BONE_CORTICAL_ICRP
  name = G4_BONE_CORTICAL_ICRP
  specific = 4
FEATURE [App::DocumentObjectGroupPython] B_element001  label="B_element : 4"  # scripted group (container) (typed FeaturePython)
  n = 4
  ref = B_element
FEATURE [App::DocumentObjectGroupPython] C_element017  label="C_element : 1"  # scripted group (container) (typed FeaturePython)
  n = 1
  ref = C_element
FEATURE [App::DocumentObjectGroupPython] G4_BORON_CARBIDE  # scripted group (container) (typed FeaturePython)
  Dunit = g/cm3
  Dvalue = 2.52
  Group = -> [B_element001,C_element017]
  conduct = 2
  density = 1
  expand = 3
  formula = G4_BORON_CARBIDE
  name = G4_BORON_CARBIDE
  specific = 4
FEATURE [App::DocumentObjectGroupPython] B_element002  label="B_element : 2"  # scripted group (container) (typed FeaturePython)
  n = 2
  ref = B_element
FEATURE [App::DocumentObjectGroupPython] O_element016  label="O_element : 006"  # scripted group (container) (typed FeaturePython)
  n = 3
  ref = O_element
FEATURE [App::DocumentObjectGroupPython] G4_BORON_OXIDE  # scripted group (container) (typed FeaturePython)
  Dunit = g/cm3
  Dvalue = 1.812
  Group = -> [B_element002,O_element016]
  conduct = 2
  density = 1
  expand = 3
  formula = G4_BORON_OXIDE
  name = G4_BORON_OXIDE
  specific = 4
FEATURE [App::DocumentObjectGroupPython] H_element017  label="H_element : 0.107"  # scripted group (container) (typed FeaturePython)
  n = 0.107
FEATURE [App::DocumentObjectGroupPython] C_element018  label="C_element : 0.145"  # scripted group (container) (typed FeaturePython)
  n = 0.145
FEATURE [App::DocumentObjectGroupPython] N_element012  label="N_element : 0.022"  # scripted group (container) (typed FeaturePython)
  n = 0.022
FEATURE [App::DocumentObjectGroupPython] O_element017  label="O_element : 0.712"  # scripted group (container) (typed FeaturePython)
  n = 0.712
FEATURE [App::DocumentObjectGroupPython] Na_element004  label="Na_element : 0.004"  # scripted group (container) (typed FeaturePython)
  n = 0.002
FEATURE [App::DocumentObjectGroupPython] P_element004  label="P_element : 0.004"  # scripted group (container) (typed FeaturePython)
  n = 0.004
FEATURE [App::DocumentObjectGroupPython] S_element006  label="S_element : 0.005"  # scripted group (container) (typed FeaturePython)
  n = 0.002
FEATURE [App::DocumentObjectGroupPython] Cl_element003  label="Cl_element : 0.004"  # scripted group (container) (typed FeaturePython)
  n = 0.003
FEATURE [App::DocumentObjectGroupPython] K_element002  label="K_element : 0.003"  # scripted group (container) (typed FeaturePython)
  n = 0.003
FEATURE [App::DocumentObjectGroupPython] G4_BRAIN_ICRP  # scripted group (container) (typed FeaturePython)
  Dunit = g/cm3
  Dvalue = 1.04
  Group = -> [H_element017,C_element018,N_element012,O_element017,Na_element004,P_element004,S_element006,Cl_element003,K_element002]
  conduct = 2
  density = 1
  expand = 3
  formula = G4_BRAIN_ICRP
  name = G4_BRAIN_ICRP
  specific = 4
FEATURE [App::DocumentObjectGroupPython] C_element019  label="C_element : 4"  # scripted group (container) (typed FeaturePython)
  n = 4
  ref = C_element
FEATURE [App::DocumentObjectGroupPython] H_element018  label="H_element : 010"  # scripted group (container) (typed FeaturePython)
  n = 10
  ref = H_element
FEATURE [App::DocumentObjectGroupPython] G4_BUTANE  # scripted group (container) (typed FeaturePython)
  Dunit = g/cm3
  Dvalue = 0.00249343
  Group = -> [C_element019,H_element018]
  conduct = 2
  density = 1
  expand = 3
  formula = G4_BUTANE
  name = G4_BUTANE
  specific = 4
FEATURE [App::DocumentObjectGroupPython] C_element020  label="C_element : 008"  # scripted group (container) (typed FeaturePython)
  n = 4
  ref = C_element
FEATURE [App::DocumentObjectGroupPython] H_element019  label="H_element : 011"  # scripted group (container) (typed FeaturePython)
  n = 10
  ref = H_element
FEATURE [App::DocumentObjectGroupPython] O_element018  label="O_element : 007"  # scripted group (container) (typed FeaturePython)
  n = 1
  ref = O_element
FEATURE [App::DocumentObjectGroupPython] G4_N_BUTYL_ALCOHOL  label="G4_N-BUTYL_ALCOHOL"  # scripted group (container) (typed FeaturePython)
  Dunit = g/cm3
  Dvalue = 0.8098
  Group = -> [C_element020,H_element019,O_element018]
  conduct = 2
  density = 1
  expand = 3
  formula = G4_N-BUTYL_ALCOHOL
  name = G4_N-BUTYL_ALCOHOL
  specific = 4
FEATURE [App::DocumentObjectGroupPython] H_element020  label="H_element : 0.025"  # scripted group (container) (typed FeaturePython)
  n = 0.02468
FEATURE [App::DocumentObjectGroupPython] C_element021  label="C_element : 0.502"  # scripted group (container) (typed FeaturePython)
  n = 0.501611
FEATURE [App::DocumentObjectGroupPython] O_element019  label="O_element : 0.005"  # scripted group (container) (typed FeaturePython)
  n = 0.004527
FEATURE [App::DocumentObjectGroupPython] F_element004  label="F_element : 0.465"  # scripted group (container) (typed FeaturePython)
  n = 0.465209
FEATURE [App::DocumentObjectGroupPython] Si_element001  label="Si_element : 0.004"  # scripted group (container) (typed FeaturePython)
  n = 0.003973
FEATURE [App::DocumentObjectGroupPython] G4_C_552  label="G4_C-552"  # scripted group (container) (typed FeaturePython)
  Dunit = g/cm3
  Dvalue = 1.76
  Group = -> [H_element020,C_element021,O_element019,F_element004,Si_element001]
  conduct = 2
  density = 1
  expand = 3
  formula = G4_C-552
  name = G4_C-552
  specific = 4
FEATURE [App::DocumentObjectGroupPython] Cd_element001  label="Cd_element : 1"  # scripted group (container) (typed FeaturePython)
  n = 1
  ref = Cd_element
FEATURE [App::DocumentObjectGroupPython] Te_element001  label="Te_element : 1"  # scripted group (container) (typed FeaturePython)
  n = 1
  ref = Te_element
FEATURE [App::DocumentObjectGroupPython] G4_CADMIUM_TELLURIDE  # scripted group (container) (typed FeaturePython)
  Dunit = g/cm3
  Dvalue = 6.2
  Group = -> [Cd_element001,Te_element001]
  conduct = 2
  density = 1
  expand = 3
  formula = G4_CADMIUM_TELLURIDE
  name = G4_CADMIUM_TELLURIDE
  specific = 4
FEATURE [App::DocumentObjectGroupPython] Cd_element002  label="Cd_element : 002"  # scripted group (container) (typed FeaturePython)
  n = 1
  ref = Cd_element
FEATURE [App::DocumentObjectGroupPython] W_element001  label="W_element : 1"  # scripted group (container) (typed FeaturePython)
  n = 1
  ref = W_element
FEATURE [App::DocumentObjectGroupPython] O_element020  label="O_element : 008"  # scripted group (container) (typed FeaturePython)
  n = 4
  ref = O_element
FEATURE [App::DocumentObjectGroupPython] G4_CADMIUM_TUNGSTATE  # scripted group (container) (typed FeaturePython)
  Dunit = g/cm3
  Dvalue = 7.9
  Group = -> [Cd_element002,W_element001,O_element020]
  conduct = 2
  density = 1
  expand = 3
  formula = G4_CADMIUM_TUNGSTATE
  name = G4_CADMIUM_TUNGSTATE
  specific = 4
FEATURE [App::DocumentObjectGroupPython] Ca_element005  label="Ca_element : 1"  # scripted group (container) (typed FeaturePython)
  n = 1
  ref = Ca_element
FEATURE [App::DocumentObjectGroupPython] C_element022  label="C_element : 009"  # scripted group (container) (typed FeaturePython)
  n = 1
  ref = C_element
FEATURE [App::DocumentObjectGroupPython] O_element021  label="O_element : 009"  # scripted group (container) (typed FeaturePython)
  n = 3
  ref = O_element
FEATURE [App::DocumentObjectGroupPython] G4_CALCIUM_CARBONATE  # scripted group (container) (typed FeaturePython)
  Dunit = g/cm3
  Dvalue = 2.8
  Group = -> [Ca_element005,C_element022,O_element021]
  conduct = 2
  density = 1
  expand = 3
  formula = G4_CALCIUM_CARBONATE
  name = G4_CALCIUM_CARBONATE
  specific = 4
FEATURE [App::DocumentObjectGroupPython] Ca_element006  label="Ca_element : 002"  # scripted group (container) (typed FeaturePython)
  n = 1
  ref = Ca_element
FEATURE [App::DocumentObjectGroupPython] F_element005  label="F_element : 003"  # scripted group (container) (typed FeaturePython)
  n = 2
  ref = F_element
FEATURE [App::DocumentObjectGroupPython] G4_CALCIUM_FLUORIDE  # scripted group (container) (typed FeaturePython)
  Dunit = g/cm3
  Dvalue = 3.18
  Group = -> [Ca_element006,F_element005]
  conduct = 2
  density = 1
  expand = 3
  formula = G4_CALCIUM_FLUORIDE
  name = G4_CALCIUM_FLUORIDE
  specific = 4
FEATURE [App::DocumentObjectGroupPython] Ca_element007  label="Ca_element : 003"  # scripted group (container) (typed FeaturePython)
  n = 1
  ref = Ca_element
FEATURE [App::DocumentObjectGroupPython] O_element022  label="O_element : 010"  # scripted group (container) (typed FeaturePython)
  n = 1
  ref = O_element
FEATURE [App::DocumentObjectGroupPython] G4_CALCIUM_OXIDE  # scripted group (container) (typed FeaturePython)
  Dunit = g/cm3
  Dvalue = 3.3
  Group = -> [Ca_element007,O_element022]
  conduct = 2
  density = 1
  expand = 3
  formula = G4_CALCIUM_OXIDE
  name = G4_CALCIUM_OXIDE
  specific = 4
FEATURE [App::DocumentObjectGroupPython] Ca_element008  label="Ca_element : 004"  # scripted group (container) (typed FeaturePython)
  n = 1
  ref = Ca_element
FEATURE [App::DocumentObjectGroupPython] S_element007  label="S_element : 002"  # scripted group (container) (typed FeaturePython)
  n = 1
  ref = S_element
FEATURE [App::DocumentObjectGroupPython] O_element023  label="O_element : 011"  # scripted group (container) (typed FeaturePython)
  n = 4
  ref = O_element
FEATURE [App::DocumentObjectGroupPython] G4_CALCIUM_SULFATE  # scripted group (container) (typed FeaturePython)
  Dunit = g/cm3
  Dvalue = 2.96
  Group = -> [Ca_element008,S_element007,O_element023]
  conduct = 2
  density = 1
  expand = 3
  formula = G4_CALCIUM_SULFATE
  name = G4_CALCIUM_SULFATE
  specific = 4
FEATURE [App::DocumentObjectGroupPython] Ca_element009  label="Ca_element : 005"  # scripted group (container) (typed FeaturePython)
  n = 1
  ref = Ca_element
FEATURE [App::DocumentObjectGroupPython] W_element002  label="W_element : 002"  # scripted group (container) (typed FeaturePython)
  n = 1
  ref = W_element
FEATURE [App::DocumentObjectGroupPython] O_element024  label="O_element : 012"  # scripted group (container) (typed FeaturePython)
  n = 4
  ref = O_element
FEATURE [App::DocumentObjectGroupPython] G4_CALCIUM_TUNGSTATE  # scripted group (container) (typed FeaturePython)
  Dunit = g/cm3
  Dvalue = 6.062
  Group = -> [Ca_element009,W_element002,O_element024]
  conduct = 2
  density = 1
  expand = 3
  formula = G4_CALCIUM_TUNGSTATE
  name = G4_CALCIUM_TUNGSTATE
  specific = 4
FEATURE [App::DocumentObjectGroupPython] C_element023  label="C_element : 010"  # scripted group (container) (typed FeaturePython)
  n = 1
  ref = C_element
FEATURE [App::DocumentObjectGroupPython] O_element025  label="O_element : 013"  # scripted group (container) (typed FeaturePython)
  n = 2
  ref = O_element
FEATURE [App::DocumentObjectGroupPython] G4_CARBON_DIOXIDE  # scripted group (container) (typed FeaturePython)
  Dunit = g/cm3
  Dvalue = 0.00184212
  Group = -> [C_element023,O_element025]
  conduct = 2
  density = 1
  expand = 3
  formula = G4_CARBON_DIOXIDE
  name = G4_CARBON_DIOXIDE
  specific = 4
FEATURE [App::DocumentObjectGroupPython] C_element024  label="C_element : 011"  # scripted group (container) (typed FeaturePython)
  n = 1
  ref = C_element
FEATURE [App::DocumentObjectGroupPython] Cl_element004  label="Cl_element : 4"  # scripted group (container) (typed FeaturePython)
  n = 4
  ref = Cl_element
FEATURE [App::DocumentObjectGroupPython] G4_CARBON_TETRACHLORIDE  # scripted group (container) (typed FeaturePython)
  Dunit = g/cm3
  Dvalue = 1.594
  Group = -> [C_element024,Cl_element004]
  conduct = 2
  density = 1
  expand = 3
  formula = G4_CARBON_TETRACHLORIDE
  name = G4_CARBON_TETRACHLORIDE
  specific = 4
FEATURE [App::DocumentObjectGroupPython] C_element025  label="C_element : 012"  # scripted group (container) (typed FeaturePython)
  n = 6
  ref = C_element
FEATURE [App::DocumentObjectGroupPython] H_element021  label="H_element : 012"  # scripted group (container) (typed FeaturePython)
  n = 10
  ref = H_element
FEATURE [App::DocumentObjectGroupPython] O_element026  label="O_element : 5"  # scripted group (container) (typed FeaturePython)
  n = 5
  ref = O_element
FEATURE [App::DocumentObjectGroupPython] G4_CELLULOSE_CELLOPHANE  # scripted group (container) (typed FeaturePython)
  Dunit = g/cm3
  Dvalue = 1.42
  Group = -> [C_element025,H_element021,O_element026]
  conduct = 2
  density = 1
  expand = 3
  formula = G4_CELLULOSE_CELLOPHANE
  name = G4_CELLULOSE_CELLOPHANE
  specific = 4
FEATURE [App::DocumentObjectGroupPython] H_element022  label="H_element : 0.067"  # scripted group (container) (typed FeaturePython)
  n = 0.067125
FEATURE [App::DocumentObjectGroupPython] C_element026  label="C_element : 0.545"  # scripted group (container) (typed FeaturePython)
  n = 0.545403
FEATURE [App::DocumentObjectGroupPython] O_element027  label="O_element : 0.387"  # scripted group (container) (typed FeaturePython)
  n = 0.387472
FEATURE [App::DocumentObjectGroupPython] G4_CELLULOSE_BUTYRATE  # scripted group (container) (typed FeaturePython)
  Dunit = g/cm3
  Dvalue = 1.2
  Group = -> [H_element022,C_element026,O_element027]
  conduct = 2
  density = 1
  expand = 3
  formula = G4_CELLULOSE_BUTYRATE
  name = G4_CELLULOSE_BUTYRATE
  specific = 4
FEATURE [App::DocumentObjectGroupPython] H_element023  label="H_element : 0.029"  # scripted group (container) (typed FeaturePython)
  n = 0.029216
FEATURE [App::DocumentObjectGroupPython] C_element027  label="C_element : 0.271"  # scripted group (container) (typed FeaturePython)
  n = 0.271296
FEATURE [App::DocumentObjectGroupPython] N_element013  label="N_element : 0.121"  # scripted group (container) (typed FeaturePython)
  n = 0.121276
FEATURE [App::DocumentObjectGroupPython] O_element028  label="O_element : 0.578"  # scripted group (container) (typed FeaturePython)
  n = 0.578212
FEATURE [App::DocumentObjectGroupPython] G4_CELLULOSE_NITRATE  # scripted group (container) (typed FeaturePython)
  Dunit = g/cm3
  Dvalue = 1.49
  Group = -> [H_element023,C_element027,N_element013,O_element028]
  conduct = 2
  density = 1
  expand = 3
  formula = G4_CELLULOSE_NITRATE
  name = G4_CELLULOSE_NITRATE
  specific = 4
FEATURE [App::DocumentObjectGroupPython] H_element024  label="H_element : 0.108"  # scripted group (container) (typed FeaturePython)
  n = 0.107596
FEATURE [App::DocumentObjectGroupPython] N_element014  label="N_element : 0.001"  # scripted group (container) (typed FeaturePython)
  n = 0.0008
FEATURE [App::DocumentObjectGroupPython] O_element029  label="O_element : 0.875"  # scripted group (container) (typed FeaturePython)
  n = 0.874976
FEATURE [App::DocumentObjectGroupPython] S_element008  label="S_element : 0.015"  # scripted group (container) (typed FeaturePython)
  n = 0.014627
FEATURE [App::DocumentObjectGroupPython] Ce_element001  label="Ce_element : 0.002"  # scripted group (container) (typed FeaturePython)
  n = 0.002001
FEATURE [App::DocumentObjectGroupPython] G4_CERIC_SULFATE  # scripted group (container) (typed FeaturePython)
  Dunit = g/cm3
  Dvalue = 1.03
  Group = -> [H_element024,N_element014,O_element029,S_element008,Ce_element001]
  conduct = 2
  density = 1
  expand = 3
  formula = G4_CERIC_SULFATE
  name = G4_CERIC_SULFATE
  specific = 4
FEATURE [App::DocumentObjectGroupPython] Cs_element001  label="Cs_element : 1"  # scripted group (container) (typed FeaturePython)
  n = 1
  ref = Cs_element
FEATURE [App::DocumentObjectGroupPython] F_element006  label="F_element : 1"  # scripted group (container) (typed FeaturePython)
  n = 1
  ref = F_element
FEATURE [App::DocumentObjectGroupPython] G4_CESIUM_FLUORIDE  # scripted group (container) (typed FeaturePython)
  Dunit = g/cm3
  Dvalue = 4.115
  Group = -> [Cs_element001,F_element006]
  conduct = 2
  density = 1
  expand = 3
  formula = G4_CESIUM_FLUORIDE
  name = G4_CESIUM_FLUORIDE
  specific = 4
FEATURE [App::DocumentObjectGroupPython] Cs_element002  label="Cs_element : 002"  # scripted group (container) (typed FeaturePython)
  n = 1
  ref = Cs_element
FEATURE [App::DocumentObjectGroupPython] I_element001  label="I_element : 1"  # scripted group (container) (typed FeaturePython)
  n = 1
  ref = I_element
FEATURE [App::DocumentObjectGroupPython] G4_CESIUM_IODIDE  # scripted group (container) (typed FeaturePython)
  Dunit = g/cm3
  Dvalue = 4.51
  Group = -> [Cs_element002,I_element001]
  conduct = 2
  density = 1
  expand = 3
  formula = G4_CESIUM_IODIDE
  name = G4_CESIUM_IODIDE
  specific = 4
FEATURE [App::DocumentObjectGroupPython] C_element028  label="C_element : 013"  # scripted group (container) (typed FeaturePython)
  n = 6
  ref = C_element
FEATURE [App::DocumentObjectGroupPython] H_element025  label="H_element : 013"  # scripted group (container) (typed FeaturePython)
  n = 5
  ref = H_element
FEATURE [App::DocumentObjectGroupPython] Cl_element005  label="Cl_element : 1"  # scripted group (container) (typed FeaturePython)
  n = 1
  ref = Cl_element
FEATURE [App::DocumentObjectGroupPython] G4_CHLOROBENZENE  # scripted group (container) (typed FeaturePython)
  Dunit = g/cm3
  Dvalue = 1.1058
  Group = -> [C_element028,H_element025,Cl_element005]
  conduct = 2
  density = 1
  expand = 3
  formula = G4_CHLOROBENZENE
  name = G4_CHLOROBENZENE
  specific = 4
FEATURE [App::DocumentObjectGroupPython] C_element029  label="C_element : 014"  # scripted group (container) (typed FeaturePython)
  n = 1
  ref = C_element
FEATURE [App::DocumentObjectGroupPython] H_element026  label="H_element : 1"  # scripted group (container) (typed FeaturePython)
  n = 1
  ref = H_element
FEATURE [App::DocumentObjectGroupPython] Cl_element006  label="Cl_element : 3"  # scripted group (container) (typed FeaturePython)
  n = 3
  ref = Cl_element
FEATURE [App::DocumentObjectGroupPython] G4_CHLOROFORM  # scripted group (container) (typed FeaturePython)
  Dunit = g/cm3
  Dvalue = 1.4832
  Group = -> [C_element029,H_element026,Cl_element006]
  conduct = 2
  density = 1
  expand = 3
  formula = G4_CHLOROFORM
  name = G4_CHLOROFORM
  specific = 4
FEATURE [App::DocumentObjectGroupPython] H_element027  label="H_element : 0.010"  # scripted group (container) (typed FeaturePython)
  n = 0.01
FEATURE [App::DocumentObjectGroupPython] C_element030  label="C_element : 0.001"  # scripted group (container) (typed FeaturePython)
  n = 0.001
FEATURE [App::DocumentObjectGroupPython] O_element030  label="O_element : 0.529"  # scripted group (container) (typed FeaturePython)
  n = 0.529107
FEATURE [App::DocumentObjectGroupPython] Na_element005  label="Na_element : 0.016"  # scripted group (container) (typed FeaturePython)
  n = 0.016
FEATURE [App::DocumentObjectGroupPython] Mg_element003  label="Mg_element : 0.004"  # scripted group (container) (typed FeaturePython)
  n = 0.002
FEATURE [App::DocumentObjectGroupPython] Al_element002  label="Al_element : 0.034"  # scripted group (container) (typed FeaturePython)
  n = 0.033872
FEATURE [App::DocumentObjectGroupPython] Si_element002  label="Si_element : 0.337"  # scripted group (container) (typed FeaturePython)
  n = 0.337021
FEATURE [App::DocumentObjectGroupPython] K_element003  label="K_element : 0.013"  # scripted group (container) (typed FeaturePython)
  n = 0.013
FEATURE [App::DocumentObjectGroupPython] Ca_element010  label="Ca_element : 0.044"  # scripted group (container) (typed FeaturePython)
  n = 0.044
FEATURE [App::DocumentObjectGroupPython] Fe_element002  label="Fe_element : 0.014"  # scripted group (container) (typed FeaturePython)
  n = 0.014
FEATURE [App::DocumentObjectGroupPython] G4_CONCRETE  # scripted group (container) (typed FeaturePython)
  Dunit = g/cm3
  Dvalue = 2.3
  Group = -> [H_element027,C_element030,O_element030,Na_element005,Mg_element003,Al_element002,Si_element002,K_element003,Ca_element010,Fe_element002]
  conduct = 2
  density = 1
  expand = 3
  formula = G4_CONCRETE
  name = G4_CONCRETE
  specific = 4
FEATURE [App::DocumentObjectGroupPython] C_element031  label="C_element : 015"  # scripted group (container) (typed FeaturePython)
  n = 6
  ref = C_element
FEATURE [App::DocumentObjectGroupPython] H_element028  label="H_element : 12"  # scripted group (container) (typed FeaturePython)
  n = 12
  ref = H_element
FEATURE [App::DocumentObjectGroupPython] G4_CYCLOHEXANE  # scripted group (container) (typed FeaturePython)
  Dunit = g/cm3
  Dvalue = 0.779
  Group = -> [C_element031,H_element028]
  conduct = 2
  density = 1
  expand = 3
  formula = G4_CYCLOHEXANE
  name = G4_CYCLOHEXANE
  specific = 4
FEATURE [App::DocumentObjectGroupPython] C_element032  label="C_element : 016"  # scripted group (container) (typed FeaturePython)
  n = 6
  ref = C_element
FEATURE [App::DocumentObjectGroupPython] H_element029  label="H_element : 4"  # scripted group (container) (typed FeaturePython)
  n = 4
  ref = H_element
FEATURE [App::DocumentObjectGroupPython] Cl_element007  label="Cl_element : 2"  # scripted group (container) (typed FeaturePython)
  n = 2
  ref = Cl_element
FEATURE [App::DocumentObjectGroupPython] G4_1_2_DICHLOROBENZENE  label="G4_1.2-DICHLOROBENZENE"  # scripted group (container) (typed FeaturePython)
  Dunit = g/cm3
  Dvalue = 1.3048
  Group = -> [C_element032,H_element029,Cl_element007]
  conduct = 2
  density = 1
  expand = 3
  formula = G4_1.2-DICHLOROBENZENE
  name = G4_1.2-DICHLOROBENZENE
  specific = 4
FEATURE [App::DocumentObjectGroupPython] C_element033  label="C_element : 017"  # scripted group (container) (typed FeaturePython)
  n = 4
  ref = C_element
FEATURE [App::DocumentObjectGroupPython] H_element030  label="H_element : 8"  # scripted group (container) (typed FeaturePython)
  n = 8
  ref = H_element
FEATURE [App::DocumentObjectGroupPython] O_element031  label="O_element : 014"  # scripted group (container) (typed FeaturePython)
  n = 1
  ref = O_element
FEATURE [App::DocumentObjectGroupPython] Cl_element008  label="Cl_element : 005"  # scripted group (container) (typed FeaturePython)
  n = 2
  ref = Cl_element
FEATURE [App::DocumentObjectGroupPython] G4_DICHLORODIETHYL_ETHER  # scripted group (container) (typed FeaturePython)
  Dunit = g/cm3
  Dvalue = 1.2199
  Group = -> [C_element033,H_element030,O_element031,Cl_element008]
  conduct = 2
  density = 1
  expand = 3
  formula = G4_DICHLORODIETHYL_ETHER
  name = G4_DICHLORODIETHYL_ETHER
  specific = 4
FEATURE [App::DocumentObjectGroupPython] C_element034  label="C_element : 018"  # scripted group (container) (typed FeaturePython)
  n = 2
  ref = C_element
FEATURE [App::DocumentObjectGroupPython] H_element031  label="H_element : 014"  # scripted group (container) (typed FeaturePython)
  n = 4
  ref = H_element
FEATURE [App::DocumentObjectGroupPython] Cl_element009  label="Cl_element : 006"  # scripted group (container) (typed FeaturePython)
  n = 2
  ref = Cl_element
FEATURE [App::DocumentObjectGroupPython] G4_1_2_DICHLOROETHANE  label="G4_1.2-DICHLOROETHANE"  # scripted group (container) (typed FeaturePython)
  Dunit = g/cm3
  Dvalue = 1.2351
  Group = -> [C_element034,H_element031,Cl_element009]
  conduct = 2
  density = 1
  expand = 3
  formula = G4_1.2-DICHLOROETHANE
  name = G4_1.2-DICHLOROETHANE
  specific = 4
FEATURE [App::DocumentObjectGroupPython] C_element035  label="C_element : 019"  # scripted group (container) (typed FeaturePython)
  n = 4
  ref = C_element
FEATURE [App::DocumentObjectGroupPython] H_element032  label="H_element : 015"  # scripted group (container) (typed FeaturePython)
  n = 10
  ref = H_element
FEATURE [App::DocumentObjectGroupPython] O_element032  label="O_element : 015"  # scripted group (container) (typed FeaturePython)
  n = 1
  ref = O_element
FEATURE [App::DocumentObjectGroupPython] G4_DIETHYL_ETHER  # scripted group (container) (typed FeaturePython)
  Dunit = g/cm3
  Dvalue = 0.71378
  Group = -> [C_element035,H_element032,O_element032]
  conduct = 2
  density = 1
  expand = 3
  formula = G4_DIETHYL_ETHER
  name = G4_DIETHYL_ETHER
  specific = 4
FEATURE [App::DocumentObjectGroupPython] C_element036  label="C_element : 020"  # scripted group (container) (typed FeaturePython)
  n = 3
  ref = C_element
FEATURE [App::DocumentObjectGroupPython] H_element033  label="H_element : 016"  # scripted group (container) (typed FeaturePython)
  n = 7
  ref = H_element
FEATURE [App::DocumentObjectGroupPython] N_element015  label="N_element : 008"  # scripted group (container) (typed FeaturePython)
  n = 1
  ref = N_element
FEATURE [App::DocumentObjectGroupPython] O_element033  label="O_element : 016"  # scripted group (container) (typed FeaturePython)
  n = 1
  ref = O_element
FEATURE [App::DocumentObjectGroupPython] G4_N_N_DIMETHYL_FORMAMIDE  label="G4_N.N-DIMETHYL_FORMAMIDE"  # scripted group (container) (typed FeaturePython)
  Dunit = g/cm3
  Dvalue = 0.9487
  Group = -> [C_element036,H_element033,N_element015,O_element033]
  conduct = 2
  density = 1
  expand = 3
  formula = G4_N.N-DIMETHYL_FORMAMIDE
  name = G4_N.N-DIMETHYL_FORMAMIDE
  specific = 4
FEATURE [App::DocumentObjectGroupPython] C_element037  label="C_element : 021"  # scripted group (container) (typed FeaturePython)
  n = 2
  ref = C_element
FEATURE [App::DocumentObjectGroupPython] H_element034  label="H_element : 017"  # scripted group (container) (typed FeaturePython)
  n = 6
  ref = H_element
FEATURE [App::DocumentObjectGroupPython] O_element034  label="O_element : 017"  # scripted group (container) (typed FeaturePython)
  n = 1
  ref = O_element
FEATURE [App::DocumentObjectGroupPython] S_element009  label="S_element : 003"  # scripted group (container) (typed FeaturePython)
  n = 1
  ref = S_element
FEATURE [App::DocumentObjectGroupPython] G4_DIMETHYL_SULFOXIDE  # scripted group (container) (typed FeaturePython)
  Dunit = g/cm3
  Dvalue = 1.1014
  Group = -> [C_element037,H_element034,O_element034,S_element009]
  conduct = 2
  density = 1
  expand = 3
  formula = G4_DIMETHYL_SULFOXIDE
  name = G4_DIMETHYL_SULFOXIDE
  specific = 4
FEATURE [App::DocumentObjectGroupPython] C_element038  label="C_element : 022"  # scripted group (container) (typed FeaturePython)
  n = 2
  ref = C_element
FEATURE [App::DocumentObjectGroupPython] H_element035  label="H_element : 018"  # scripted group (container) (typed FeaturePython)
  n = 6
  ref = H_element
FEATURE [App::DocumentObjectGroupPython] G4_ETHANE  # scripted group (container) (typed FeaturePython)
  Dunit = g/cm3
  Dvalue = 0.00125324
  Group = -> [C_element038,H_element035]
  conduct = 2
  density = 1
  expand = 3
  formula = G4_ETHANE
  name = G4_ETHANE
  specific = 4
FEATURE [App::DocumentObjectGroupPython] C_element039  label="C_element : 023"  # scripted group (container) (typed FeaturePython)
  n = 2
  ref = C_element
FEATURE [App::DocumentObjectGroupPython] H_element036  label="H_element : 019"  # scripted group (container) (typed FeaturePython)
  n = 6
  ref = H_element
FEATURE [App::DocumentObjectGroupPython] O_element035  label="O_element : 018"  # scripted group (container) (typed FeaturePython)
  n = 1
  ref = O_element
FEATURE [App::DocumentObjectGroupPython] G4_ETHYL_ALCOHOL  # scripted group (container) (typed FeaturePython)
  Dunit = g/cm3
  Dvalue = 0.7893
  Group = -> [C_element039,H_element036,O_element035]
  conduct = 2
  density = 1
  expand = 3
  formula = G4_ETHYL_ALCOHOL
  name = G4_ETHYL_ALCOHOL
  specific = 4
FEATURE [App::DocumentObjectGroupPython] H_element037  label="H_element : 0.090"  # scripted group (container) (typed FeaturePython)
  n = 0.090027
FEATURE [App::DocumentObjectGroupPython] C_element040  label="C_element : 0.585"  # scripted group (container) (typed FeaturePython)
  n = 0.585182
FEATURE [App::DocumentObjectGroupPython] O_element036  label="O_element : 0.325"  # scripted group (container) (typed FeaturePython)
  n = 0.324791
FEATURE [App::DocumentObjectGroupPython] G4_ETHYL_CELLULOSE  # scripted group (container) (typed FeaturePython)
  Dunit = g/cm3
  Dvalue = 1.13
  Group = -> [H_element037,C_element040,O_element036]
  conduct = 2
  density = 1
  expand = 3
  formula = G4_ETHYL_CELLULOSE
  name = G4_ETHYL_CELLULOSE
  specific = 4
FEATURE [App::DocumentObjectGroupPython] C_element041  label="C_element : 024"  # scripted group (container) (typed FeaturePython)
  n = 2
  ref = C_element
FEATURE [App::DocumentObjectGroupPython] H_element038  label="H_element : 020"  # scripted group (container) (typed FeaturePython)
  n = 4
  ref = H_element
FEATURE [App::DocumentObjectGroupPython] G4_ETHYLENE  # scripted group (container) (typed FeaturePython)
  Dunit = g/cm3
  Dvalue = 0.00117497
  Group = -> [C_element041,H_element038]
  conduct = 2
  density = 1
  expand = 3
  formula = G4_ETHYLENE
  name = G4_ETHYLENE
  specific = 4
FEATURE [App::DocumentObjectGroupPython] H_element039  label="H_element : 0.096"  # scripted group (container) (typed FeaturePython)
  n = 0.096
FEATURE [App::DocumentObjectGroupPython] C_element042  label="C_element : 0.195"  # scripted group (container) (typed FeaturePython)
  n = 0.195
FEATURE [App::DocumentObjectGroupPython] N_element016  label="N_element : 0.057"  # scripted group (container) (typed FeaturePython)
  n = 0.057
FEATURE [App::DocumentObjectGroupPython] O_element037  label="O_element : 0.646"  # scripted group (container) (typed FeaturePython)
  n = 0.646
FEATURE [App::DocumentObjectGroupPython] Na_element006  label="Na_element : 0.017"  # scripted group (container) (typed FeaturePython)
  n = 0.001
FEATURE [App::DocumentObjectGroupPython] P_element005  label="P_element : 0.104"  # scripted group (container) (typed FeaturePython)
  n = 0.001
FEATURE [App::DocumentObjectGroupPython] S_element010  label="S_element : 0.016"  # scripted group (container) (typed FeaturePython)
  n = 0.003
FEATURE [App::DocumentObjectGroupPython] Cl_element010  label="Cl_element : 0.005"  # scripted group (container) (typed FeaturePython)
  n = 0.001
FEATURE [App::DocumentObjectGroupPython] G4_EYE_LENS_ICRP  # scripted group (container) (typed FeaturePython)
  Dunit = g/cm3
  Dvalue = 1.07
  Group = -> [H_element039,C_element042,N_element016,O_element037,Na_element006,P_element005,S_element010,Cl_element010]
  conduct = 2
  density = 1
  expand = 3
  formula = G4_EYE_LENS_ICRP
  name = G4_EYE_LENS_ICRP
  specific = 4
FEATURE [App::DocumentObjectGroupPython] Fe_element003  label="Fe_element : 2"  # scripted group (container) (typed FeaturePython)
  n = 2
  ref = Fe_element
FEATURE [App::DocumentObjectGroupPython] O_element038  label="O_element : 019"  # scripted group (container) (typed FeaturePython)
  n = 3
  ref = O_element
FEATURE [App::DocumentObjectGroupPython] G4_FERRIC_OXIDE  # scripted group (container) (typed FeaturePython)
  Dunit = g/cm3
  Dvalue = 5.2
  Group = -> [Fe_element003,O_element038]
  conduct = 2
  density = 1
  expand = 3
  formula = G4_FERRIC_OXIDE
  name = G4_FERRIC_OXIDE
  specific = 4
FEATURE [App::DocumentObjectGroupPython] Fe_element004  label="Fe_element : 1"  # scripted group (container) (typed FeaturePython)
  n = 1
  ref = Fe_element
FEATURE [App::DocumentObjectGroupPython] B_element003  label="B_element : 1"  # scripted group (container) (typed FeaturePython)
  n = 1
  ref = B_element
FEATURE [App::DocumentObjectGroupPython] G4_FERROBORIDE  # scripted group (container) (typed FeaturePython)
  Dunit = g/cm3
  Dvalue = 7.15
  Group = -> [Fe_element004,B_element003]
  conduct = 2
  density = 1
  expand = 3
  formula = G4_FERROBORIDE
  name = G4_FERROBORIDE
  specific = 4
FEATURE [App::DocumentObjectGroupPython] Fe_element005  label="Fe_element : 003"  # scripted group (container) (typed FeaturePython)
  n = 1
  ref = Fe_element
FEATURE [App::DocumentObjectGroupPython] O_element039  label="O_element : 020"  # scripted group (container) (typed FeaturePython)
  n = 1
  ref = O_element
FEATURE [App::DocumentObjectGroupPython] G4_FERROUS_OXIDE  # scripted group (container) (typed FeaturePython)
  Dunit = g/cm3
  Dvalue = 5.7
  Group = -> [Fe_element005,O_element039]
  conduct = 2
  density = 1
  expand = 3
  formula = G4_FERROUS_OXIDE
  name = G4_FERROUS_OXIDE
  specific = 4
FEATURE [App::DocumentObjectGroupPython] H_element040  label="H_element : 0.115"  # scripted group (container) (typed FeaturePython)
  n = 0.108259
FEATURE [App::DocumentObjectGroupPython] N_element017  label="N_element : 0.000"  # scripted group (container) (typed FeaturePython)
  n = 2.7e-05
FEATURE [App::DocumentObjectGroupPython] O_element040  label="O_element : 0.879"  # scripted group (container) (typed FeaturePython)
  n = 0.878636
FEATURE [App::DocumentObjectGroupPython] Na_element007  label="Na_element : 0.000"  # scripted group (container) (typed FeaturePython)
  n = 2.2e-05
FEATURE [App::DocumentObjectGroupPython] S_element011  label="S_element : 0.013"  # scripted group (container) (typed FeaturePython)
  n = 0.012968
FEATURE [App::DocumentObjectGroupPython] Cl_element011  label="Cl_element : 0.000"  # scripted group (container) (typed FeaturePython)
  n = 3.4e-05
FEATURE [App::DocumentObjectGroupPython] Fe_element006  label="Fe_element : 0.000"  # scripted group (container) (typed FeaturePython)
  n = 5.4e-05
FEATURE [App::DocumentObjectGroupPython] G4_FERROUS_SULFATE  # scripted group (container) (typed FeaturePython)
  Dunit = g/cm3
  Dvalue = 1.024
  Group = -> [H_element040,N_element017,O_element040,Na_element007,S_element011,Cl_element011,Fe_element006]
  conduct = 2
  density = 1
  expand = 3
  formula = G4_FERROUS_SULFATE
  name = G4_FERROUS_SULFATE
  specific = 4
FEATURE [App::DocumentObjectGroupPython] C_element043  label="C_element : 0.099"  # scripted group (container) (typed FeaturePython)
  n = 0.099335
FEATURE [App::DocumentObjectGroupPython] F_element007  label="F_element : 0.314"  # scripted group (container) (typed FeaturePython)
  n = 0.314247
FEATURE [App::DocumentObjectGroupPython] Cl_element012  label="Cl_element : 0.586"  # scripted group (container) (typed FeaturePython)
  n = 0.586418
FEATURE [App::DocumentObjectGroupPython] G4_FREON_12  label="G4_FREON-12"  # scripted group (container) (typed FeaturePython)
  Dunit = g/cm3
  Dvalue = 1.12
  Group = -> [C_element043,F_element007,Cl_element012]
  conduct = 2
  density = 1
  expand = 3
  formula = G4_FREON-12
  name = G4_FREON-12
  specific = 4
FEATURE [App::DocumentObjectGroupPython] C_element044  label="C_element : 0.057"  # scripted group (container) (typed FeaturePython)
  n = 0.057245
FEATURE [App::DocumentObjectGroupPython] F_element008  label="F_element : 0.181"  # scripted group (container) (typed FeaturePython)
  n = 0.181096
FEATURE [App::DocumentObjectGroupPython] Br_element001  label="Br_element : 0.762"  # scripted group (container) (typed FeaturePython)
  n = 0.761659
FEATURE [App::DocumentObjectGroupPython] G4_FREON_12B2  label="G4_FREON-12B2"  # scripted group (container) (typed FeaturePython)
  Dunit = g/cm3
  Dvalue = 1.8
  Group = -> [C_element044,F_element008,Br_element001]
  conduct = 2
  density = 1
  expand = 3
  formula = G4_FREON-12B2
  name = G4_FREON-12B2
  specific = 4
FEATURE [App::DocumentObjectGroupPython] C_element045  label="C_element : 0.115"  # scripted group (container) (typed FeaturePython)
  n = 0.114983
FEATURE [App::DocumentObjectGroupPython] F_element009  label="F_element : 0.546"  # scripted group (container) (typed FeaturePython)
  n = 0.545621
FEATURE [App::DocumentObjectGroupPython] Cl_element013  label="Cl_element : 0.339"  # scripted group (container) (typed FeaturePython)
  n = 0.339396
FEATURE [App::DocumentObjectGroupPython] G4_FREON_13  label="G4_FREON-13"  # scripted group (container) (typed FeaturePython)
  Dunit = g/cm3
  Dvalue = 0.95
  Group = -> [C_element045,F_element009,Cl_element013]
  conduct = 2
  density = 1
  expand = 3
  formula = G4_FREON-13
  name = G4_FREON-13
  specific = 4
FEATURE [App::DocumentObjectGroupPython] C_element046  label="C_element : 025"  # scripted group (container) (typed FeaturePython)
  n = 1
  ref = C_element
FEATURE [App::DocumentObjectGroupPython] F_element010  label="F_element : 3"  # scripted group (container) (typed FeaturePython)
  n = 3
  ref = F_element
FEATURE [App::DocumentObjectGroupPython] Br_element002  label="Br_element : 1"  # scripted group (container) (typed FeaturePython)
  n = 1
  ref = Br_element
FEATURE [App::DocumentObjectGroupPython] G4_FREON_13B1  label="G4_FREON-13B1"  # scripted group (container) (typed FeaturePython)
  Dunit = g/cm3
  Dvalue = 1.5
  Group = -> [C_element046,F_element010,Br_element002]
  conduct = 2
  density = 1
  expand = 3
  formula = G4_FREON-13B1
  name = G4_FREON-13B1
  specific = 4
FEATURE [App::DocumentObjectGroupPython] C_element047  label="C_element : 0.061"  # scripted group (container) (typed FeaturePython)
  n = 0.061309
FEATURE [App::DocumentObjectGroupPython] F_element011  label="F_element : 0.291"  # scripted group (container) (typed FeaturePython)
  n = 0.290924
FEATURE [App::DocumentObjectGroupPython] I_element002  label="I_element : 0.648"  # scripted group (container) (typed FeaturePython)
  n = 0.647767
FEATURE [App::DocumentObjectGroupPython] G4_FREON_13I1  label="G4_FREON-13I1"  # scripted group (container) (typed FeaturePython)
  Dunit = g/cm3
  Dvalue = 1.8
  Group = -> [C_element047,F_element011,I_element002]
  conduct = 2
  density = 1
  expand = 3
  formula = G4_FREON-13I1
  name = G4_FREON-13I1
  specific = 4
FEATURE [App::DocumentObjectGroupPython] Gd_element001  label="Gd_element : 2"  # scripted group (container) (typed FeaturePython)
  n = 2
  ref = Gd_element
FEATURE [App::DocumentObjectGroupPython] O_element041  label="O_element : 021"  # scripted group (container) (typed FeaturePython)
  n = 2
  ref = O_element
FEATURE [App::DocumentObjectGroupPython] S_element012  label="S_element : 004"  # scripted group (container) (typed FeaturePython)
  n = 1
  ref = S_element
FEATURE [App::DocumentObjectGroupPython] G4_GADOLINIUM_OXYSULFIDE  # scripted group (container) (typed FeaturePython)
  Dunit = g/cm3
  Dvalue = 7.44
  Group = -> [Gd_element001,O_element041,S_element012]
  conduct = 2
  density = 1
  expand = 3
  formula = G4_GADOLINIUM_OXYSULFIDE
  name = G4_GADOLINIUM_OXYSULFIDE
  specific = 4
FEATURE [App::DocumentObjectGroupPython] Ga_element001  label="Ga_element : 1"  # scripted group (container) (typed FeaturePython)
  n = 1
  ref = Ga_element
FEATURE [App::DocumentObjectGroupPython] As_element001  label="As_element : 1"  # scripted group (container) (typed FeaturePython)
  n = 1
  ref = As_element
FEATURE [App::DocumentObjectGroupPython] G4_GALLIUM_ARSENIDE  # scripted group (container) (typed FeaturePython)
  Dunit = g/cm3
  Dvalue = 5.31
  Group = -> [Ga_element001,As_element001]
  conduct = 2
  density = 1
  expand = 3
  formula = G4_GALLIUM_ARSENIDE
  name = G4_GALLIUM_ARSENIDE
  specific = 4
FEATURE [App::DocumentObjectGroupPython] H_element041  label="H_element : 0.081"  # scripted group (container) (typed FeaturePython)
  n = 0.08118
FEATURE [App::DocumentObjectGroupPython] C_element048  label="C_element : 0.416"  # scripted group (container) (typed FeaturePython)
  n = 0.41606
FEATURE [App::DocumentObjectGroupPython] N_element018  label="N_element : 0.111"  # scripted group (container) (typed FeaturePython)
  n = 0.11124
FEATURE [App::DocumentObjectGroupPython] O_element042  label="O_element : 0.381"  # scripted group (container) (typed FeaturePython)
  n = 0.38064
FEATURE [App::DocumentObjectGroupPython] S_element013  label="S_element : 0.011"  # scripted group (container) (typed FeaturePython)
  n = 0.01088
FEATURE [App::DocumentObjectGroupPython] G4_GEL_PHOTO_EMULSION  # scripted group (container) (typed FeaturePython)
  Dunit = g/cm3
  Dvalue = 1.2914
  Group = -> [H_element041,C_element048,N_element018,O_element042,S_element013]
  conduct = 2
  density = 1
  expand = 3
  formula = G4_GEL_PHOTO_EMULSION
  name = G4_GEL_PHOTO_EMULSION
  specific = 4
FEATURE [App::DocumentObjectGroupPython] B_element004  label="B_element : 0.040"  # scripted group (container) (typed FeaturePython)
  n = 0.0400639
FEATURE [App::DocumentObjectGroupPython] O_element043  label="O_element : 0.540"  # scripted group (container) (typed FeaturePython)
  n = 0.539561
FEATURE [App::DocumentObjectGroupPython] Na_element008  label="Na_element : 0.028"  # scripted group (container) (typed FeaturePython)
  n = 0.0281909
FEATURE [App::DocumentObjectGroupPython] Al_element003  label="Al_element : 0.012"  # scripted group (container) (typed FeaturePython)
  n = 0.011644
FEATURE [App::DocumentObjectGroupPython] Si_element003  label="Si_element : 0.377"  # scripted group (container) (typed FeaturePython)
  n = 0.377219
FEATURE [App::DocumentObjectGroupPython] K_element004  label="K_element : 0.014"  # scripted group (container) (typed FeaturePython)
  n = 0.00332099
FEATURE [App::DocumentObjectGroupPython] G4_Pyrex_Glass  # scripted group (container) (typed FeaturePython)
  Dunit = g/cm3
  Dvalue = 2.23
  Group = -> [B_element004,O_element043,Na_element008,Al_element003,Si_element003,K_element004]
  conduct = 2
  density = 1
  expand = 3
  formula = G4_Pyrex_Glass
  name = G4_Pyrex_Glass
  specific = 4
FEATURE [App::DocumentObjectGroupPython] O_element044  label="O_element : 0.156"  # scripted group (container) (typed FeaturePython)
  n = 0.156453
FEATURE [App::DocumentObjectGroupPython] Si_element004  label="Si_element : 0.081"  # scripted group (container) (typed FeaturePython)
  n = 0.080866
FEATURE [App::DocumentObjectGroupPython] Ti_element001  label="Ti_element : 0.008"  # scripted group (container) (typed FeaturePython)
  n = 0.008092
FEATURE [App::DocumentObjectGroupPython] As_element002  label="As_element : 0.003"  # scripted group (container) (typed FeaturePython)
  n = 0.002651
FEATURE [App::DocumentObjectGroupPython] Pb_element001  label="Pb_element : 0.752"  # scripted group (container) (typed FeaturePython)
  n = 0.751938
FEATURE [App::DocumentObjectGroupPython] G4_GLASS_LEAD  # scripted group (container) (typed FeaturePython)
  Dunit = g/cm3
  Dvalue = 6.22
  Group = -> [O_element044,Si_element004,Ti_element001,As_element002,Pb_element001]
  conduct = 2
  density = 1
  expand = 3
  formula = G4_GLASS_LEAD
  name = G4_GLASS_LEAD
  specific = 4
FEATURE [App::DocumentObjectGroupPython] O_element045  label="O_element : 0.460"  # scripted group (container) (typed FeaturePython)
  n = 0.4598
FEATURE [App::DocumentObjectGroupPython] Na_element009  label="Na_element : 0.096"  # scripted group (container) (typed FeaturePython)
  n = 0.0964411
FEATURE [App::DocumentObjectGroupPython] Si_element005  label="Si_element : 0.378"  # scripted group (container) (typed FeaturePython)
  n = 0.336553
FEATURE [App::DocumentObjectGroupPython] Ca_element011  label="Ca_element : 0.107"  # scripted group (container) (typed FeaturePython)
  n = 0.107205
FEATURE [App::DocumentObjectGroupPython] G4_GLASS_PLATE  # scripted group (container) (typed FeaturePython)
  Dunit = g/cm3
  Dvalue = 2.4
  Group = -> [O_element045,Na_element009,Si_element005,Ca_element011]
  conduct = 2
  density = 1
  expand = 3
  formula = G4_GLASS_PLATE
  name = G4_GLASS_PLATE
  specific = 4
FEATURE [App::DocumentObjectGroupPython] C_element049  label="C_element : 026"  # scripted group (container) (typed FeaturePython)
  n = 5
  ref = C_element
FEATURE [App::DocumentObjectGroupPython] H_element042  label="H_element : 021"  # scripted group (container) (typed FeaturePython)
  n = 10
  ref = H_element
FEATURE [App::DocumentObjectGroupPython] N_element019  label="N_element : 2"  # scripted group (container) (typed FeaturePython)
  n = 2
  ref = N_element
FEATURE [App::DocumentObjectGroupPython] O_element046  label="O_element : 022"  # scripted group (container) (typed FeaturePython)
  n = 3
  ref = O_element
FEATURE [App::DocumentObjectGroupPython] G4_GLUTAMINE  # scripted group (container) (typed FeaturePython)
  Dunit = g/cm3
  Dvalue = 1.46
  Group = -> [C_element049,H_element042,N_element019,O_element046]
  conduct = 2
  density = 1
  expand = 3
  formula = G4_GLUTAMINE
  name = G4_GLUTAMINE
  specific = 4
FEATURE [App::DocumentObjectGroupPython] C_element050  label="C_element : 027"  # scripted group (container) (typed FeaturePython)
  n = 3
  ref = C_element
FEATURE [App::DocumentObjectGroupPython] H_element043  label="H_element : 022"  # scripted group (container) (typed FeaturePython)
  n = 8
  ref = H_element
FEATURE [App::DocumentObjectGroupPython] O_element047  label="O_element : 023"  # scripted group (container) (typed FeaturePython)
  n = 3
  ref = O_element
FEATURE [App::DocumentObjectGroupPython] G4_GLYCEROL  # scripted group (container) (typed FeaturePython)
  Dunit = g/cm3
  Dvalue = 1.2613
  Group = -> [C_element050,H_element043,O_element047]
  conduct = 2
  density = 1
  expand = 3
  formula = G4_GLYCEROL
  name = G4_GLYCEROL
  specific = 4
FEATURE [App::DocumentObjectGroupPython] C_element051  label="C_element : 028"  # scripted group (container) (typed FeaturePython)
  n = 5
  ref = C_element
FEATURE [App::DocumentObjectGroupPython] H_element044  label="H_element : 023"  # scripted group (container) (typed FeaturePython)
  n = 5
  ref = H_element
FEATURE [App::DocumentObjectGroupPython] N_element020  label="N_element : 009"  # scripted group (container) (typed FeaturePython)
  n = 5
  ref = N_element
FEATURE [App::DocumentObjectGroupPython] O_element048  label="O_element : 024"  # scripted group (container) (typed FeaturePython)
  n = 1
  ref = O_element
FEATURE [App::DocumentObjectGroupPython] G4_GUANINE  # scripted group (container) (typed FeaturePython)
  Dunit = g/cm3
  Dvalue = 2.2
  Group = -> [C_element051,H_element044,N_element020,O_element048]
  conduct = 2
  density = 1
  expand = 3
  formula = G4_GUANINE
  name = G4_GUANINE
  specific = 4
FEATURE [App::DocumentObjectGroupPython] Ca_element012  label="Ca_element : 006"  # scripted group (container) (typed FeaturePython)
  n = 1
  ref = Ca_element
FEATURE [App::DocumentObjectGroupPython] S_element014  label="S_element : 005"  # scripted group (container) (typed FeaturePython)
  n = 1
  ref = S_element
FEATURE [App::DocumentObjectGroupPython] O_element049  label="O_element : 6"  # scripted group (container) (typed FeaturePython)
  n = 6
  ref = O_element
FEATURE [App::DocumentObjectGroupPython] H_element045  label="H_element : 024"  # scripted group (container) (typed FeaturePython)
  n = 4
  ref = H_element
FEATURE [App::DocumentObjectGroupPython] G4_GYPSUM  # scripted group (container) (typed FeaturePython)
  Dunit = g/cm3
  Dvalue = 2.32
  Group = -> [Ca_element012,S_element014,O_element049,H_element045]
  conduct = 2
  density = 1
  expand = 3
  formula = G4_GYPSUM
  name = G4_GYPSUM
  specific = 4
FEATURE [App::DocumentObjectGroupPython] C_element052  label="C_element : 7"  # scripted group (container) (typed FeaturePython)
  n = 7
  ref = C_element
FEATURE [App::DocumentObjectGroupPython] H_element046  label="H_element : 16"  # scripted group (container) (typed FeaturePython)
  n = 16
  ref = H_element
FEATURE [App::DocumentObjectGroupPython] G4_N_HEPTANE  label="G4_N-HEPTANE"  # scripted group (container) (typed FeaturePython)
  Dunit = g/cm3
  Dvalue = 0.68376
  Group = -> [C_element052,H_element046]
  conduct = 2
  density = 1
  expand = 3
  formula = G4_N-HEPTANE
  name = G4_N-HEPTANE
  specific = 4
FEATURE [App::DocumentObjectGroupPython] C_element053  label="C_element : 029"  # scripted group (container) (typed FeaturePython)
  n = 6
  ref = C_element
FEATURE [App::DocumentObjectGroupPython] H_element047  label="H_element : 14"  # scripted group (container) (typed FeaturePython)
  n = 14
  ref = H_element
FEATURE [App::DocumentObjectGroupPython] G4_N_HEXANE  label="G4_N-HEXANE"  # scripted group (container) (typed FeaturePython)
  Dunit = g/cm3
  Dvalue = 0.6603
  Group = -> [C_element053,H_element047]
  conduct = 2
  density = 1
  expand = 3
  formula = G4_N-HEXANE
  name = G4_N-HEXANE
  specific = 4
FEATURE [App::DocumentObjectGroupPython] C_element054  label="C_element : 22"  # scripted group (container) (typed FeaturePython)
  n = 22
  ref = C_element
FEATURE [App::DocumentObjectGroupPython] H_element048  label="H_element : 025"  # scripted group (container) (typed FeaturePython)
  n = 10
  ref = H_element
FEATURE [App::DocumentObjectGroupPython] N_element021  label="N_element : 010"  # scripted group (container) (typed FeaturePython)
  n = 2
  ref = N_element
FEATURE [App::DocumentObjectGroupPython] O_element050  label="O_element : 025"  # scripted group (container) (typed FeaturePython)
  n = 5
  ref = O_element
FEATURE [App::DocumentObjectGroupPython] G4_KAPTON  # scripted group (container) (typed FeaturePython)
  Dunit = g/cm3
  Dvalue = 1.42
  Group = -> [C_element054,H_element048,N_element021,O_element050]
  conduct = 2
  density = 1
  expand = 3
  formula = G4_KAPTON
  name = G4_KAPTON
  specific = 4
FEATURE [App::DocumentObjectGroupPython] La_element001  label="La_element : 1"  # scripted group (container) (typed FeaturePython)
  n = 1
  ref = La_element
FEATURE [App::DocumentObjectGroupPython] Br_element003  label="Br_element : 002"  # scripted group (container) (typed FeaturePython)
  n = 1
  ref = Br_element
FEATURE [App::DocumentObjectGroupPython] O_element051  label="O_element : 026"  # scripted group (container) (typed FeaturePython)
  n = 1
  ref = O_element
FEATURE [App::DocumentObjectGroupPython] G4_LANTHANUM_OXYBROMIDE  # scripted group (container) (typed FeaturePython)
  Dunit = g/cm3
  Dvalue = 6.28
  Group = -> [La_element001,Br_element003,O_element051]
  conduct = 2
  density = 1
  expand = 3
  formula = G4_LANTHANUM_OXYBROMIDE
  name = G4_LANTHANUM_OXYBROMIDE
  specific = 4
FEATURE [App::DocumentObjectGroupPython] La_element002  label="La_element : 2"  # scripted group (container) (typed FeaturePython)
  n = 2
  ref = La_element
FEATURE [App::DocumentObjectGroupPython] O_element052  label="O_element : 027"  # scripted group (container) (typed FeaturePython)
  n = 2
  ref = O_element
FEATURE [App::DocumentObjectGroupPython] S_element015  label="S_element : 006"  # scripted group (container) (typed FeaturePython)
  n = 1
  ref = S_element
FEATURE [App::DocumentObjectGroupPython] G4_LANTHANUM_OXYSULFIDE  # scripted group (container) (typed FeaturePython)
  Dunit = g/cm3
  Dvalue = 5.86
  Group = -> [La_element002,O_element052,S_element015]
  conduct = 2
  density = 1
  expand = 3
  formula = G4_LANTHANUM_OXYSULFIDE
  name = G4_LANTHANUM_OXYSULFIDE
  specific = 4
FEATURE [App::DocumentObjectGroupPython] O_element053  label="O_element : 0.072"  # scripted group (container) (typed FeaturePython)
  n = 0.071682
FEATURE [App::DocumentObjectGroupPython] Pb_element002  label="Pb_element : 0.928"  # scripted group (container) (typed FeaturePython)
  n = 0.928318
FEATURE [App::DocumentObjectGroupPython] G4_LEAD_OXIDE  # scripted group (container) (typed FeaturePython)
  Dunit = g/cm3
  Dvalue = 9.53
  Group = -> [O_element053,Pb_element002]
  conduct = 2
  density = 1
  expand = 3
  formula = G4_LEAD_OXIDE
  name = G4_LEAD_OXIDE
  specific = 4
FEATURE [App::DocumentObjectGroupPython] Li_element001  label="Li_element : 1"  # scripted group (container) (typed FeaturePython)
  n = 1
  ref = Li_element
FEATURE [App::DocumentObjectGroupPython] N_element022  label="N_element : 011"  # scripted group (container) (typed FeaturePython)
  n = 1
  ref = N_element
FEATURE [App::DocumentObjectGroupPython] H_element049  label="H_element : 026"  # scripted group (container) (typed FeaturePython)
  n = 2
  ref = H_element
FEATURE [App::DocumentObjectGroupPython] G4_LITHIUM_AMIDE  # scripted group (container) (typed FeaturePython)
  Dunit = g/cm3
  Dvalue = 1.178
  Group = -> [Li_element001,N_element022,H_element049]
  conduct = 2
  density = 1
  expand = 3
  formula = G4_LITHIUM_AMIDE
  name = G4_LITHIUM_AMIDE
  specific = 4
FEATURE [App::DocumentObjectGroupPython] Li_element002  label="Li_element : 2"  # scripted group (container) (typed FeaturePython)
  n = 2
  ref = Li_element
FEATURE [App::DocumentObjectGroupPython] C_element055  label="C_element : 030"  # scripted group (container) (typed FeaturePython)
  n = 1
  ref = C_element
FEATURE [App::DocumentObjectGroupPython] O_element054  label="O_element : 028"  # scripted group (container) (typed FeaturePython)
  n = 3
  ref = O_element
FEATURE [App::DocumentObjectGroupPython] G4_LITHIUM_CARBONATE  # scripted group (container) (typed FeaturePython)
  Dunit = g/cm3
  Dvalue = 2.11
  Group = -> [Li_element002,C_element055,O_element054]
  conduct = 2
  density = 1
  expand = 3
  formula = G4_LITHIUM_CARBONATE
  name = G4_LITHIUM_CARBONATE
  specific = 4
FEATURE [App::DocumentObjectGroupPython] Li_element003  label="Li_element : 003"  # scripted group (container) (typed FeaturePython)
  n = 1
  ref = Li_element
FEATURE [App::DocumentObjectGroupPython] F_element012  label="F_element : 004"  # scripted group (container) (typed FeaturePython)
  n = 1
  ref = F_element
FEATURE [App::DocumentObjectGroupPython] G4_LITHIUM_FLUORIDE  # scripted group (container) (typed FeaturePython)
  Dunit = g/cm3
  Dvalue = 2.635
  Group = -> [Li_element003,F_element012]
  conduct = 2
  density = 1
  expand = 3
  formula = G4_LITHIUM_FLUORIDE
  name = G4_LITHIUM_FLUORIDE
  specific = 4
FEATURE [App::DocumentObjectGroupPython] Li_element004  label="Li_element : 004"  # scripted group (container) (typed FeaturePython)
  n = 1
  ref = Li_element
FEATURE [App::DocumentObjectGroupPython] H_element050  label="H_element : 027"  # scripted group (container) (typed FeaturePython)
  n = 1
  ref = H_element
FEATURE [App::DocumentObjectGroupPython] G4_LITHIUM_HYDRIDE  # scripted group (container) (typed FeaturePython)
  Dunit = g/cm3
  Dvalue = 0.82
  Group = -> [Li_element004,H_element050]
  conduct = 2
  density = 1
  expand = 3
  formula = G4_LITHIUM_HYDRIDE
  name = G4_LITHIUM_HYDRIDE
  specific = 4
FEATURE [App::DocumentObjectGroupPython] Li_element005  label="Li_element : 005"  # scripted group (container) (typed FeaturePython)
  n = 1
  ref = Li_element
FEATURE [App::DocumentObjectGroupPython] I_element003  label="I_element : 002"  # scripted group (container) (typed FeaturePython)
  n = 1
  ref = I_element
FEATURE [App::DocumentObjectGroupPython] G4_LITHIUM_IODIDE  # scripted group (container) (typed FeaturePython)
  Dunit = g/cm3
  Dvalue = 3.494
  Group = -> [Li_element005,I_element003]
  conduct = 2
  density = 1
  expand = 3
  formula = G4_LITHIUM_IODIDE
  name = G4_LITHIUM_IODIDE
  specific = 4
FEATURE [App::DocumentObjectGroupPython] Li_element006  label="Li_element : 006"  # scripted group (container) (typed FeaturePython)
  n = 2
  ref = Li_element
FEATURE [App::DocumentObjectGroupPython] O_element055  label="O_element : 029"  # scripted group (container) (typed FeaturePython)
  n = 1
  ref = O_element
FEATURE [App::DocumentObjectGroupPython] G4_LITHIUM_OXIDE  # scripted group (container) (typed FeaturePython)
  Dunit = g/cm3
  Dvalue = 2.013
  Group = -> [Li_element006,O_element055]
  conduct = 2
  density = 1
  expand = 3
  formula = G4_LITHIUM_OXIDE
  name = G4_LITHIUM_OXIDE
  specific = 4
FEATURE [App::DocumentObjectGroupPython] Li_element007  label="Li_element : 007"  # scripted group (container) (typed FeaturePython)
  n = 2
  ref = Li_element
FEATURE [App::DocumentObjectGroupPython] B_element005  label="B_element : 005"  # scripted group (container) (typed FeaturePython)
  n = 4
  ref = B_element
FEATURE [App::DocumentObjectGroupPython] O_element056  label="O_element : 7"  # scripted group (container) (typed FeaturePython)
  n = 7
  ref = O_element
FEATURE [App::DocumentObjectGroupPython] G4_LITHIUM_TETRABORATE  # scripted group (container) (typed FeaturePython)
  Dunit = g/cm3
  Dvalue = 2.44
  Group = -> [Li_element007,B_element005,O_element056]
  conduct = 2
  density = 1
  expand = 3
  formula = G4_LITHIUM_TETRABORATE
  name = G4_LITHIUM_TETRABORATE
  specific = 4
FEATURE [App::DocumentObjectGroupPython] H_element051  label="H_element : 0.105"  # scripted group (container) (typed FeaturePython)
  n = 0.105
FEATURE [App::DocumentObjectGroupPython] C_element056  label="C_element : 0.083"  # scripted group (container) (typed FeaturePython)
  n = 0.083
FEATURE [App::DocumentObjectGroupPython] N_element023  label="N_element : 0.023"  # scripted group (container) (typed FeaturePython)
  n = 0.023
FEATURE [App::DocumentObjectGroupPython] O_element057  label="O_element : 0.779"  # scripted group (container) (typed FeaturePython)
  n = 0.779
FEATURE [App::DocumentObjectGroupPython] Na_element010  label="Na_element : 0.097"  # scripted group (container) (typed FeaturePython)
  n = 0.002
FEATURE [App::DocumentObjectGroupPython] P_element006  label="P_element : 0.105"  # scripted group (container) (typed FeaturePython)
  n = 0.001
FEATURE [App::DocumentObjectGroupPython] S_element016  label="S_element : 0.017"  # scripted group (container) (typed FeaturePython)
  n = 0.002
FEATURE [App::DocumentObjectGroupPython] Cl_element014  label="Cl_element : 0.587"  # scripted group (container) (typed FeaturePython)
  n = 0.003
FEATURE [App::DocumentObjectGroupPython] K_element005  label="K_element : 0.015"  # scripted group (container) (typed FeaturePython)
  n = 0.002
FEATURE [App::DocumentObjectGroupPython] G4_LUNG_ICRP  # scripted group (container) (typed FeaturePython)
  Dunit = g/cm3
  Dvalue = 1.04
  Group = -> [H_element051,C_element056,N_element023,O_element057,Na_element010,P_element006,S_element016,Cl_element014,K_element005]
  conduct = 2
  density = 1
  expand = 3
  formula = G4_LUNG_ICRP
  name = G4_LUNG_ICRP
  specific = 4
FEATURE [App::DocumentObjectGroupPython] H_element052  label="H_element : 0.116"  # scripted group (container) (typed FeaturePython)
  n = 0.114318
FEATURE [App::DocumentObjectGroupPython] C_element057  label="C_element : 0.656"  # scripted group (container) (typed FeaturePython)
  n = 0.655824
FEATURE [App::DocumentObjectGroupPython] O_element058  label="O_element : 0.092"  # scripted group (container) (typed FeaturePython)
  n = 0.0921831
FEATURE [App::DocumentObjectGroupPython] Mg_element004  label="Mg_element : 0.135"  # scripted group (container) (typed FeaturePython)
  n = 0.134792
FEATURE [App::DocumentObjectGroupPython] Ca_element013  label="Ca_element : 0.003"  # scripted group (container) (typed FeaturePython)
  n = 0.002883
FEATURE [App::DocumentObjectGroupPython] G4_M3_WAX  # scripted group (container) (typed FeaturePython)
  Dunit = g/cm3
  Dvalue = 1.05
  Group = -> [H_element052,C_element057,O_element058,Mg_element004,Ca_element013]
  conduct = 2
  density = 1
  expand = 3
  formula = G4_M3_WAX
  name = G4_M3_WAX
  specific = 4
FEATURE [App::DocumentObjectGroupPython] Mg_element005  label="Mg_element : 1"  # scripted group (container) (typed FeaturePython)
  n = 1
  ref = Mg_element
FEATURE [App::DocumentObjectGroupPython] C_element058  label="C_element : 031"  # scripted group (container) (typed FeaturePython)
  n = 1
  ref = C_element
FEATURE [App::DocumentObjectGroupPython] O_element059  label="O_element : 030"  # scripted group (container) (typed FeaturePython)
  n = 3
  ref = O_element
FEATURE [App::DocumentObjectGroupPython] G4_MAGNESIUM_CARBONATE  # scripted group (container) (typed FeaturePython)
  Dunit = g/cm3
  Dvalue = 2.958
  Group = -> [Mg_element005,C_element058,O_element059]
  conduct = 2
  density = 1
  expand = 3
  formula = G4_MAGNESIUM_CARBONATE
  name = G4_MAGNESIUM_CARBONATE
  specific = 4
FEATURE [App::DocumentObjectGroupPython] Mg_element006  label="Mg_element : 002"  # scripted group (container) (typed FeaturePython)
  n = 1
  ref = Mg_element
FEATURE [App::DocumentObjectGroupPython] F_element013  label="F_element : 005"  # scripted group (container) (typed FeaturePython)
  n = 2
  ref = F_element
FEATURE [App::DocumentObjectGroupPython] G4_MAGNESIUM_FLUORIDE  # scripted group (container) (typed FeaturePython)
  Dunit = g/cm3
  Dvalue = 3
  Group = -> [Mg_element006,F_element013]
  conduct = 2
  density = 1
  expand = 3
  formula = G4_MAGNESIUM_FLUORIDE
  name = G4_MAGNESIUM_FLUORIDE
  specific = 4
FEATURE [App::DocumentObjectGroupPython] Mg_element007  label="Mg_element : 003"  # scripted group (container) (typed FeaturePython)
  n = 1
  ref = Mg_element
FEATURE [App::DocumentObjectGroupPython] O_element060  label="O_element : 031"  # scripted group (container) (typed FeaturePython)
  n = 1
  ref = O_element
FEATURE [App::DocumentObjectGroupPython] G4_MAGNESIUM_OXIDE  # scripted group (container) (typed FeaturePython)
  Dunit = g/cm3
  Dvalue = 3.58
  Group = -> [Mg_element007,O_element060]
  conduct = 2
  density = 1
  expand = 3
  formula = G4_MAGNESIUM_OXIDE
  name = G4_MAGNESIUM_OXIDE
  specific = 4
FEATURE [App::DocumentObjectGroupPython] Mg_element008  label="Mg_element : 004"  # scripted group (container) (typed FeaturePython)
  n = 1
  ref = Mg_element
FEATURE [App::DocumentObjectGroupPython] B_element006  label="B_element : 006"  # scripted group (container) (typed FeaturePython)
  n = 4
  ref = B_element
FEATURE [App::DocumentObjectGroupPython] O_element061  label="O_element : 032"  # scripted group (container) (typed FeaturePython)
  n = 7
  ref = O_element
FEATURE [App::DocumentObjectGroupPython] G4_MAGNESIUM_TETRABORATE  # scripted group (container) (typed FeaturePython)
  Dunit = g/cm3
  Dvalue = 2.53
  Group = -> [Mg_element008,B_element006,O_element061]
  conduct = 2
  density = 1
  expand = 3
  formula = G4_MAGNESIUM_TETRABORATE
  name = G4_MAGNESIUM_TETRABORATE
  specific = 4
FEATURE [App::DocumentObjectGroupPython] Hg_element001  label="Hg_element : 1"  # scripted group (container) (typed FeaturePython)
  n = 1
  ref = Hg_element
FEATURE [App::DocumentObjectGroupPython] I_element004  label="I_element : 2"  # scripted group (container) (typed FeaturePython)
  n = 2
  ref = I_element
FEATURE [App::DocumentObjectGroupPython] G4_MERCURIC_IODIDE  # scripted group (container) (typed FeaturePython)
  Dunit = g/cm3
  Dvalue = 6.36
  Group = -> [Hg_element001,I_element004]
  conduct = 2
  density = 1
  expand = 3
  formula = G4_MERCURIC_IODIDE
  name = G4_MERCURIC_IODIDE
  specific = 4
FEATURE [App::DocumentObjectGroupPython] C_element059  label="C_element : 032"  # scripted group (container) (typed FeaturePython)
  n = 1
  ref = C_element
FEATURE [App::DocumentObjectGroupPython] H_element053  label="H_element : 028"  # scripted group (container) (typed FeaturePython)
  n = 4
  ref = H_element
FEATURE [App::DocumentObjectGroupPython] G4_METHANE  # scripted group (container) (typed FeaturePython)
  Dunit = g/cm3
  Dvalue = 0.000667151
  Group = -> [C_element059,H_element053]
  conduct = 2
  density = 1
  expand = 3
  formula = G4_METHANE
  name = G4_METHANE
  specific = 4
FEATURE [App::DocumentObjectGroupPython] C_element060  label="C_element : 033"  # scripted group (container) (typed FeaturePython)
  n = 1
  ref = C_element
FEATURE [App::DocumentObjectGroupPython] H_element054  label="H_element : 029"  # scripted group (container) (typed FeaturePython)
  n = 4
  ref = H_element
FEATURE [App::DocumentObjectGroupPython] O_element062  label="O_element : 033"  # scripted group (container) (typed FeaturePython)
  n = 1
  ref = O_element
FEATURE [App::DocumentObjectGroupPython] G4_METHANOL  # scripted group (container) (typed FeaturePython)
  Dunit = g/cm3
  Dvalue = 0.7914
  Group = -> [C_element060,H_element054,O_element062]
  conduct = 2
  density = 1
  expand = 3
  formula = G4_METHANOL
  name = G4_METHANOL
  specific = 4
FEATURE [App::DocumentObjectGroupPython] H_element055  label="H_element : 0.134"  # scripted group (container) (typed FeaturePython)
  n = 0.13404
FEATURE [App::DocumentObjectGroupPython] C_element061  label="C_element : 0.778"  # scripted group (container) (typed FeaturePython)
  n = 0.77796
FEATURE [App::DocumentObjectGroupPython] O_element063  label="O_element : 0.035"  # scripted group (container) (typed FeaturePython)
  n = 0.03502
FEATURE [App::DocumentObjectGroupPython] Mg_element009  label="Mg_element : 0.039"  # scripted group (container) (typed FeaturePython)
  n = 0.038594
FEATURE [App::DocumentObjectGroupPython] Ti_element002  label="Ti_element : 0.014"  # scripted group (container) (typed FeaturePython)
  n = 0.014386
FEATURE [App::DocumentObjectGroupPython] G4_MIX_D_WAX  # scripted group (container) (typed FeaturePython)
  Dunit = g/cm3
  Dvalue = 0.99
  Group = -> [H_element055,C_element061,O_element063,Mg_element009,Ti_element002]
  conduct = 2
  density = 1
  expand = 3
  formula = G4_MIX_D_WAX
  name = G4_MIX_D_WAX
  specific = 4
FEATURE [App::DocumentObjectGroupPython] H_element056  label="H_element : 0.135"  # scripted group (container) (typed FeaturePython)
  n = 0.081192
FEATURE [App::DocumentObjectGroupPython] C_element062  label="C_element : 0.583"  # scripted group (container) (typed FeaturePython)
  n = 0.583442
FEATURE [App::DocumentObjectGroupPython] N_element024  label="N_element : 0.018"  # scripted group (container) (typed FeaturePython)
  n = 0.017798
FEATURE [App::DocumentObjectGroupPython] O_element064  label="O_element : 0.186"  # scripted group (container) (typed FeaturePython)
  n = 0.186381
FEATURE [App::DocumentObjectGroupPython] Mg_element010  label="Mg_element : 0.130"  # scripted group (container) (typed FeaturePython)
  n = 0.130287
FEATURE [App::DocumentObjectGroupPython] Cl_element015  label="Cl_element : 0.588"  # scripted group (container) (typed FeaturePython)
  n = 0.0009
FEATURE [App::DocumentObjectGroupPython] G4_MS20_TISSUE  # scripted group (container) (typed FeaturePython)
  Dunit = g/cm3
  Dvalue = 1
  Group = -> [H_element056,C_element062,N_element024,O_element064,Mg_element010,Cl_element015]
  conduct = 2
  density = 1
  expand = 3
  formula = G4_MS20_TISSUE
  name = G4_MS20_TISSUE
  specific = 4
FEATURE [App::DocumentObjectGroupPython] H_element057  label="H_element : 0.136"  # scripted group (container) (typed FeaturePython)
  n = 0.102
FEATURE [App::DocumentObjectGroupPython] C_element063  label="C_element : 0.143"  # scripted group (container) (typed FeaturePython)
  n = 0.143
FEATURE [App::DocumentObjectGroupPython] N_element025  label="N_element : 0.034"  # scripted group (container) (typed FeaturePython)
  n = 0.034
FEATURE [App::DocumentObjectGroupPython] O_element065  label="O_element : 0.710"  # scripted group (container) (typed FeaturePython)
  n = 0.71
FEATURE [App::DocumentObjectGroupPython] Na_element011  label="Na_element : 0.098"  # scripted group (container) (typed FeaturePython)
  n = 0.001
FEATURE [App::DocumentObjectGroupPython] P_element007  label="P_element : 0.002"  # scripted group (container) (typed FeaturePython)
  n = 0.002
FEATURE [App::DocumentObjectGroupPython] S_element017  label="S_element : 0.018"  # scripted group (container) (typed FeaturePython)
  n = 0.003
FEATURE [App::DocumentObjectGroupPython] Cl_element016  label="Cl_element : 0.589"  # scripted group (container) (typed FeaturePython)
  n = 0.001
FEATURE [App::DocumentObjectGroupPython] K_element006  label="K_element : 0.004"  # scripted group (container) (typed FeaturePython)
  n = 0.004
FEATURE [App::DocumentObjectGroupPython] G4_MUSCLE_SKELETAL_ICRP  # scripted group (container) (typed FeaturePython)
  Dunit = g/cm3
  Dvalue = 1.05
  Group = -> [H_element057,C_element063,N_element025,O_element065,Na_element011,P_element007,S_element017,Cl_element016,K_element006]
  conduct = 2
  density = 1
  expand = 3
  formula = G4_MUSCLE_SKELETAL_ICRP
  name = G4_MUSCLE_SKELETAL_ICRP
  specific = 4
FEATURE [App::DocumentObjectGroupPython] H_element058  label="H_element : 0.137"  # scripted group (container) (typed FeaturePython)
  n = 0.102102
FEATURE [App::DocumentObjectGroupPython] C_element064  label="C_element : 0.123"  # scripted group (container) (typed FeaturePython)
  n = 0.123123
FEATURE [App::DocumentObjectGroupPython] N_element026  label="N_element : 0.756"  # scripted group (container) (typed FeaturePython)
  n = 0.035035
FEATURE [App::DocumentObjectGroupPython] O_element066  label="O_element : 0.730"  # scripted group (container) (typed FeaturePython)
  n = 0.72973
FEATURE [App::DocumentObjectGroupPython] Na_element012  label="Na_element : 0.099"  # scripted group (container) (typed FeaturePython)
  n = 0.001001
FEATURE [App::DocumentObjectGroupPython] P_element008  label="P_element : 0.106"  # scripted group (container) (typed FeaturePython)
  n = 0.002002
FEATURE [App::DocumentObjectGroupPython] S_element018  label="S_element : 0.019"  # scripted group (container) (typed FeaturePython)
  n = 0.004004
FEATURE [App::DocumentObjectGroupPython] K_element007  label="K_element : 0.016"  # scripted group (container) (typed FeaturePython)
  n = 0.003003
FEATURE [App::DocumentObjectGroupPython] G4_MUSCLE_STRIATED_ICRU  # scripted group (container) (typed FeaturePython)
  Dunit = g/cm3
  Dvalue = 1.04
  Group = -> [H_element058,C_element064,N_element026,O_element066,Na_element012,P_element008,S_element018,K_element007]
  conduct = 2
  density = 1
  expand = 3
  formula = G4_MUSCLE_STRIATED_ICRU
  name = G4_MUSCLE_STRIATED_ICRU
  specific = 4
FEATURE [App::DocumentObjectGroupPython] H_element059  label="H_element : 0.098"  # scripted group (container) (typed FeaturePython)
  n = 0.0982341
FEATURE [App::DocumentObjectGroupPython] C_element065  label="C_element : 0.156"  # scripted group (container) (typed FeaturePython)
  n = 0.156214
FEATURE [App::DocumentObjectGroupPython] N_element027  label="N_element : 0.757"  # scripted group (container) (typed FeaturePython)
  n = 0.035451
FEATURE [App::DocumentObjectGroupPython] O_element067  label="O_element : 0.880"  # scripted group (container) (typed FeaturePython)
  n = 0.710101
FEATURE [App::DocumentObjectGroupPython] G4_MUSCLE_WITH_SUCROSE  # scripted group (container) (typed FeaturePython)
  Dunit = g/cm3
  Dvalue = 1.11
  Group = -> [H_element059,C_element065,N_element027,O_element067]
  conduct = 2
  density = 1
  expand = 3
  formula = G4_MUSCLE_WITH_SUCROSE
  name = G4_MUSCLE_WITH_SUCROSE
  specific = 4
FEATURE [App::DocumentObjectGroupPython] H_element060  label="H_element : 0.138"  # scripted group (container) (typed FeaturePython)
  n = 0.101969
FEATURE [App::DocumentObjectGroupPython] C_element066  label="C_element : 0.120"  # scripted group (container) (typed FeaturePython)
  n = 0.120058
FEATURE [App::DocumentObjectGroupPython] N_element028  label="N_element : 0.758"  # scripted group (container) (typed FeaturePython)
  n = 0.035451
FEATURE [App::DocumentObjectGroupPython] O_element068  label="O_element : 0.743"  # scripted group (container) (typed FeaturePython)
  n = 0.742522
FEATURE [App::DocumentObjectGroupPython] G4_MUSCLE_WITHOUT_SUCROSE  # scripted group (container) (typed FeaturePython)
  Dunit = g/cm3
  Dvalue = 1.07
  Group = -> [H_element060,C_element066,N_element028,O_element068]
  conduct = 2
  density = 1
  expand = 3
  formula = G4_MUSCLE_WITHOUT_SUCROSE
  name = G4_MUSCLE_WITHOUT_SUCROSE
  specific = 4
FEATURE [App::DocumentObjectGroupPython] C_element067  label="C_element : 10"  # scripted group (container) (typed FeaturePython)
  n = 10
  ref = C_element
FEATURE [App::DocumentObjectGroupPython] H_element061  label="H_element : 030"  # scripted group (container) (typed FeaturePython)
  n = 8
  ref = H_element
FEATURE [App::DocumentObjectGroupPython] G4_NAPHTHALENE  # scripted group (container) (typed FeaturePython)
  Dunit = g/cm3
  Dvalue = 1.145
  Group = -> [C_element067,H_element061]
  conduct = 2
  density = 1
  expand = 3
  formula = G4_NAPHTHALENE
  name = G4_NAPHTHALENE
  specific = 4
FEATURE [App::DocumentObjectGroupPython] C_element068  label="C_element : 034"  # scripted group (container) (typed FeaturePython)
  n = 6
  ref = C_element
FEATURE [App::DocumentObjectGroupPython] H_element062  label="H_element : 031"  # scripted group (container) (typed FeaturePython)
  n = 5
  ref = H_element
FEATURE [App::DocumentObjectGroupPython] N_element029  label="N_element : 012"  # scripted group (container) (typed FeaturePython)
  n = 1
  ref = N_element
FEATURE [App::DocumentObjectGroupPython] O_element069  label="O_element : 034"  # scripted group (container) (typed FeaturePython)
  n = 2
  ref = O_element
FEATURE [App::DocumentObjectGroupPython] G4_NITROBENZENE  # scripted group (container) (typed FeaturePython)
  Dunit = g/cm3
  Dvalue = 1.19867
  Group = -> [C_element068,H_element062,N_element029,O_element069]
  conduct = 2
  density = 1
  expand = 3
  formula = G4_NITROBENZENE
  name = G4_NITROBENZENE
  specific = 4
FEATURE [App::DocumentObjectGroupPython] N_element030  label="N_element : 013"  # scripted group (container) (typed FeaturePython)
  n = 2
  ref = N_element
FEATURE [App::DocumentObjectGroupPython] O_element070  label="O_element : 035"  # scripted group (container) (typed FeaturePython)
  n = 1
  ref = O_element
FEATURE [App::DocumentObjectGroupPython] G4_NITROUS_OXIDE  # scripted group (container) (typed FeaturePython)
  Dunit = g/cm3
  Dvalue = 0.00183094
  Group = -> [N_element030,O_element070]
  conduct = 2
  density = 1
  expand = 3
  formula = G4_NITROUS_OXIDE
  name = G4_NITROUS_OXIDE
  specific = 4
FEATURE [App::DocumentObjectGroupPython] H_element063  label="H_element : 0.104"  # scripted group (container) (typed FeaturePython)
  n = 0.103509
FEATURE [App::DocumentObjectGroupPython] C_element069  label="C_element : 0.648"  # scripted group (container) (typed FeaturePython)
  n = 0.648416
FEATURE [App::DocumentObjectGroupPython] N_element031  label="N_element : 0.100"  # scripted group (container) (typed FeaturePython)
  n = 0.0995361
FEATURE [App::DocumentObjectGroupPython] O_element071  label="O_element : 0.149"  # scripted group (container) (typed FeaturePython)
  n = 0.148539
FEATURE [App::DocumentObjectGroupPython] G4_NYLON_8062  label="G4_NYLON-8062"  # scripted group (container) (typed FeaturePython)
  Dunit = g/cm3
  Dvalue = 1.08
  Group = -> [H_element063,C_element069,N_element031,O_element071]
  conduct = 2
  density = 1
  expand = 3
  formula = G4_NYLON-8062
  name = G4_NYLON-8062
  specific = 4
FEATURE [App::DocumentObjectGroupPython] C_element070  label="C_element : 035"  # scripted group (container) (typed FeaturePython)
  n = 6
  ref = C_element
FEATURE [App::DocumentObjectGroupPython] H_element064  label="H_element : 11"  # scripted group (container) (typed FeaturePython)
  n = 11
  ref = H_element
FEATURE [App::DocumentObjectGroupPython] N_element032  label="N_element : 014"  # scripted group (container) (typed FeaturePython)
  n = 1
  ref = N_element
FEATURE [App::DocumentObjectGroupPython] O_element072  label="O_element : 036"  # scripted group (container) (typed FeaturePython)
  n = 1
  ref = O_element
FEATURE [App::DocumentObjectGroupPython] G4_NYLON_6_6  label="G4_NYLON-6-6"  # scripted group (container) (typed FeaturePython)
  Dunit = g/cm3
  Dvalue = 1.14
  Group = -> [C_element070,H_element064,N_element032,O_element072]
  conduct = 2
  density = 1
  expand = 3
  formula = G4_NYLON-6-6
  name = G4_NYLON-6-6
  specific = 4
FEATURE [App::DocumentObjectGroupPython] H_element065  label="H_element : 0.139"  # scripted group (container) (typed FeaturePython)
  n = 0.107062
FEATURE [App::DocumentObjectGroupPython] C_element071  label="C_element : 0.680"  # scripted group (container) (typed FeaturePython)
  n = 0.680449
FEATURE [App::DocumentObjectGroupPython] N_element033  label="N_element : 0.099"  # scripted group (container) (typed FeaturePython)
  n = 0.099189
FEATURE [App::DocumentObjectGroupPython] O_element073  label="O_element : 0.113"  # scripted group (container) (typed FeaturePython)
  n = 0.1133
FEATURE [App::DocumentObjectGroupPython] G4_NYLON_6_10  label="G4_NYLON-6-10"  # scripted group (container) (typed FeaturePython)
  Dunit = g/cm3
  Dvalue = 1.14
  Group = -> [H_element065,C_element071,N_element033,O_element073]
  conduct = 2
  density = 1
  expand = 3
  formula = G4_NYLON-6-10
  name = G4_NYLON-6-10
  specific = 4
FEATURE [App::DocumentObjectGroupPython] H_element066  label="H_element : 0.140"  # scripted group (container) (typed FeaturePython)
  n = 0.115476
FEATURE [App::DocumentObjectGroupPython] C_element072  label="C_element : 0.721"  # scripted group (container) (typed FeaturePython)
  n = 0.720818
FEATURE [App::DocumentObjectGroupPython] N_element034  label="N_element : 0.076"  # scripted group (container) (typed FeaturePython)
  n = 0.0764169
FEATURE [App::DocumentObjectGroupPython] O_element074  label="O_element : 0.087"  # scripted group (container) (typed FeaturePython)
  n = 0.0872889
FEATURE [App::DocumentObjectGroupPython] G4_NYLON_11_RILSAN  label="G4_NYLON-11_RILSAN"  # scripted group (container) (typed FeaturePython)
  Dunit = g/cm3
  Dvalue = 1.425
  Group = -> [H_element066,C_element072,N_element034,O_element074]
  conduct = 2
  density = 1
  expand = 3
  formula = G4_NYLON-11_RILSAN
  name = G4_NYLON-11_RILSAN
  specific = 4
FEATURE [App::DocumentObjectGroupPython] C_element073  label="C_element : 8"  # scripted group (container) (typed FeaturePython)
  n = 8
  ref = C_element
FEATURE [App::DocumentObjectGroupPython] H_element067  label="H_element : 18"  # scripted group (container) (typed FeaturePython)
  n = 18
  ref = H_element
FEATURE [App::DocumentObjectGroupPython] G4_OCTANE  # scripted group (container) (typed FeaturePython)
  Dunit = g/cm3
  Dvalue = 0.7026
  Group = -> [C_element073,H_element067]
  conduct = 2
  density = 1
  expand = 3
  formula = G4_OCTANE
  name = G4_OCTANE
  specific = 4
FEATURE [App::DocumentObjectGroupPython] C_element074  label="C_element : 25"  # scripted group (container) (typed FeaturePython)
  n = 25
  ref = C_element
FEATURE [App::DocumentObjectGroupPython] H_element068  label="H_element : 52"  # scripted group (container) (typed FeaturePython)
  n = 52
  ref = H_element
FEATURE [App::DocumentObjectGroupPython] G4_PARAFFIN  # scripted group (container) (typed FeaturePython)
  Dunit = g/cm3
  Dvalue = 0.93
  Group = -> [C_element074,H_element068]
  conduct = 2
  density = 1
  expand = 3
  formula = G4_PARAFFIN
  name = G4_PARAFFIN
  specific = 4
FEATURE [App::DocumentObjectGroupPython] C_element075  label="C_element : 036"  # scripted group (container) (typed FeaturePython)
  n = 5
  ref = C_element
FEATURE [App::DocumentObjectGroupPython] H_element069  label="H_element : 032"  # scripted group (container) (typed FeaturePython)
  n = 12
  ref = H_element
FEATURE [App::DocumentObjectGroupPython] G4_N_PENTANE  label="G4_N-PENTANE"  # scripted group (container) (typed FeaturePython)
  Dunit = g/cm3
  Dvalue = 0.6262
  Group = -> [C_element075,H_element069]
  conduct = 2
  density = 1
  expand = 3
  formula = G4_N-PENTANE
  name = G4_N-PENTANE
  specific = 4
FEATURE [App::DocumentObjectGroupPython] H_element070  label="H_element : 0.014"  # scripted group (container) (typed FeaturePython)
  n = 0.0141
FEATURE [App::DocumentObjectGroupPython] C_element076  label="C_element : 0.072"  # scripted group (container) (typed FeaturePython)
  n = 0.072261
FEATURE [App::DocumentObjectGroupPython] N_element035  label="N_element : 0.019"  # scripted group (container) (typed FeaturePython)
  n = 0.01932
FEATURE [App::DocumentObjectGroupPython] O_element075  label="O_element : 0.066"  # scripted group (container) (typed FeaturePython)
  n = 0.066101
FEATURE [App::DocumentObjectGroupPython] S_element019  label="S_element : 0.020"  # scripted group (container) (typed FeaturePython)
  n = 0.00189
FEATURE [App::DocumentObjectGroupPython] Br_element004  label="Br_element : 0.349"  # scripted group (container) (typed FeaturePython)
  n = 0.349103
FEATURE [App::DocumentObjectGroupPython] Ag_element001  label="Ag_element : 0.474"  # scripted group (container) (typed FeaturePython)
  n = 0.474105
FEATURE [App::DocumentObjectGroupPython] I_element005  label="I_element : 0.003"  # scripted group (container) (typed FeaturePython)
  n = 0.00312
FEATURE [App::DocumentObjectGroupPython] G4_PHOTO_EMULSION  # scripted group (container) (typed FeaturePython)
  Dunit = g/cm3
  Dvalue = 3.815
  Group = -> [H_element070,C_element076,N_element035,O_element075,S_element019,Br_element004,Ag_element001,I_element005]
  conduct = 2
  density = 1
  expand = 3
  formula = G4_PHOTO_EMULSION
  name = G4_PHOTO_EMULSION
  specific = 4
FEATURE [App::DocumentObjectGroupPython] C_element077  label="C_element : 9"  # scripted group (container) (typed FeaturePython)
  n = 9
  ref = C_element
FEATURE [App::DocumentObjectGroupPython] H_element071  label="H_element : 033"  # scripted group (container) (typed FeaturePython)
  n = 10
  ref = H_element
FEATURE [App::DocumentObjectGroupPython] G4_PLASTIC_SC_VINYLTOLUENE  # scripted group (container) (typed FeaturePython)
  Dunit = g/cm3
  Dvalue = 1.032
  Group = -> [C_element077,H_element071]
  conduct = 2
  density = 1
  expand = 3
  formula = G4_PLASTIC_SC_VINYLTOLUENE
  name = G4_PLASTIC_SC_VINYLTOLUENE
  specific = 4
FEATURE [App::DocumentObjectGroupPython] Pu_element001  label="Pu_element : 1"  # scripted group (container) (typed FeaturePython)
  n = 1
  ref = Pu_element
FEATURE [App::DocumentObjectGroupPython] O_element076  label="O_element : 037"  # scripted group (container) (typed FeaturePython)
  n = 2
  ref = O_element
FEATURE [App::DocumentObjectGroupPython] G4_PLUTONIUM_DIOXIDE  # scripted group (container) (typed FeaturePython)
  Dunit = g/cm3
  Dvalue = 11.46
  Group = -> [Pu_element001,O_element076]
  conduct = 2
  density = 1
  expand = 3
  formula = G4_PLUTONIUM_DIOXIDE
  name = G4_PLUTONIUM_DIOXIDE
  specific = 4
FEATURE [App::DocumentObjectGroupPython] C_element078  label="C_element : 037"  # scripted group (container) (typed FeaturePython)
  n = 3
  ref = C_element
FEATURE [App::DocumentObjectGroupPython] H_element072  label="H_element : 034"  # scripted group (container) (typed FeaturePython)
  n = 3
  ref = H_element
FEATURE [App::DocumentObjectGroupPython] N_element036  label="N_element : 015"  # scripted group (container) (typed FeaturePython)
  n = 1
  ref = N_element
FEATURE [App::DocumentObjectGroupPython] G4_POLYACRYLONITRILE  # scripted group (container) (typed FeaturePython)
  Dunit = g/cm3
  Dvalue = 1.17
  Group = -> [C_element078,H_element072,N_element036]
  conduct = 2
  density = 1
  expand = 3
  formula = G4_POLYACRYLONITRILE
  name = G4_POLYACRYLONITRILE
  specific = 4
FEATURE [App::DocumentObjectGroupPython] C_element079  label="C_element : 16"  # scripted group (container) (typed FeaturePython)
  n = 16
  ref = C_element
FEATURE [App::DocumentObjectGroupPython] H_element073  label="H_element : 035"  # scripted group (container) (typed FeaturePython)
  n = 14
  ref = H_element
FEATURE [App::DocumentObjectGroupPython] O_element077  label="O_element : 038"  # scripted group (container) (typed FeaturePython)
  n = 3
  ref = O_element
FEATURE [App::DocumentObjectGroupPython] G4_POLYCARBONATE  # scripted group (container) (typed FeaturePython)
  Dunit = g/cm3
  Dvalue = 1.2
  Group = -> [C_element079,H_element073,O_element077]
  conduct = 2
  density = 1
  expand = 3
  formula = G4_POLYCARBONATE
  name = G4_POLYCARBONATE
  specific = 4
FEATURE [App::DocumentObjectGroupPython] C_element080  label="C_element : 038"  # scripted group (container) (typed FeaturePython)
  n = 8
  ref = C_element
FEATURE [App::DocumentObjectGroupPython] H_element074  label="H_element : 036"  # scripted group (container) (typed FeaturePython)
  n = 7
  ref = H_element
FEATURE [App::DocumentObjectGroupPython] Cl_element017  label="Cl_element : 007"  # scripted group (container) (typed FeaturePython)
  n = 1
  ref = Cl_element
FEATURE [App::DocumentObjectGroupPython] G4_POLYCHLOROSTYRENE  # scripted group (container) (typed FeaturePython)
  Dunit = g/cm3
  Dvalue = 1.3
  Group = -> [C_element080,H_element074,Cl_element017]
  conduct = 2
  density = 1
  expand = 3
  formula = G4_POLYCHLOROSTYRENE
  name = G4_POLYCHLOROSTYRENE
  specific = 4
FEATURE [App::DocumentObjectGroupPython] C_element081  label="C_element : 039"  # scripted group (container) (typed FeaturePython)
  n = 1
  ref = C_element
FEATURE [App::DocumentObjectGroupPython] H_element075  label="H_element : 037"  # scripted group (container) (typed FeaturePython)
  n = 2
  ref = H_element
FEATURE [App::DocumentObjectGroupPython] G4_POLYETHYLENE  # scripted group (container) (typed FeaturePython)
  Dunit = g/cm3
  Dvalue = 0.94
  Group = -> [C_element081,H_element075]
  conduct = 2
  density = 1
  expand = 3
  formula = G4_POLYETHYLENE
  name = G4_POLYETHYLENE
  specific = 4
FEATURE [App::DocumentObjectGroupPython] C_element082  label="C_element : 040"  # scripted group (container) (typed FeaturePython)
  n = 10
  ref = C_element
FEATURE [App::DocumentObjectGroupPython] H_element076  label="H_element : 038"  # scripted group (container) (typed FeaturePython)
  n = 8
  ref = H_element
FEATURE [App::DocumentObjectGroupPython] O_element078  label="O_element : 039"  # scripted group (container) (typed FeaturePython)
  n = 4
  ref = O_element
FEATURE [App::DocumentObjectGroupPython] G4_MYLAR  # scripted group (container) (typed FeaturePython)
  Dunit = g/cm3
  Dvalue = 1.4
  Group = -> [C_element082,H_element076,O_element078]
  conduct = 2
  density = 1
  expand = 3
  formula = G4_MYLAR
  name = G4_MYLAR
  specific = 4
FEATURE [App::DocumentObjectGroupPython] C_element083  label="C_element : 041"  # scripted group (container) (typed FeaturePython)
  n = 5
  ref = C_element
FEATURE [App::DocumentObjectGroupPython] H_element077  label="H_element : 039"  # scripted group (container) (typed FeaturePython)
  n = 8
  ref = H_element
FEATURE [App::DocumentObjectGroupPython] O_element079  label="O_element : 040"  # scripted group (container) (typed FeaturePython)
  n = 2
  ref = O_element
FEATURE [App::DocumentObjectGroupPython] G4_PLEXIGLASS  # scripted group (container) (typed FeaturePython)
  Dunit = g/cm3
  Dvalue = 1.19
  Group = -> [C_element083,H_element077,O_element079]
  conduct = 2
  density = 1
  expand = 3
  formula = G4_PLEXIGLASS
  name = G4_PLEXIGLASS
  specific = 4
FEATURE [App::DocumentObjectGroupPython] C_element084  label="C_element : 042"  # scripted group (container) (typed FeaturePython)
  n = 1
  ref = C_element
FEATURE [App::DocumentObjectGroupPython] H_element078  label="H_element : 040"  # scripted group (container) (typed FeaturePython)
  n = 2
  ref = H_element
FEATURE [App::DocumentObjectGroupPython] O_element080  label="O_element : 041"  # scripted group (container) (typed FeaturePython)
  n = 1
  ref = O_element
FEATURE [App::DocumentObjectGroupPython] G4_POLYOXYMETHYLENE  # scripted group (container) (typed FeaturePython)
  Dunit = g/cm3
  Dvalue = 1.425
  Group = -> [C_element084,H_element078,O_element080]
  conduct = 2
  density = 1
  expand = 3
  formula = G4_POLYOXYMETHYLENE
  name = G4_POLYOXYMETHYLENE
  specific = 4
FEATURE [App::DocumentObjectGroupPython] C_element085  label="C_element : 043"  # scripted group (container) (typed FeaturePython)
  n = 2
  ref = C_element
FEATURE [App::DocumentObjectGroupPython] H_element079  label="H_element : 041"  # scripted group (container) (typed FeaturePython)
  n = 4
  ref = H_element
FEATURE [App::DocumentObjectGroupPython] G4_POLYPROPYLENE  # scripted group (container) (typed FeaturePython)
  Dunit = g/cm3
  Dvalue = 0.9
  Group = -> [C_element085,H_element079]
  conduct = 2
  density = 1
  expand = 3
  formula = G4_POLYPROPYLENE
  name = G4_POLYPROPYLENE
  specific = 4
FEATURE [App::DocumentObjectGroupPython] C_element086  label="C_element : 044"  # scripted group (container) (typed FeaturePython)
  n = 8
  ref = C_element
FEATURE [App::DocumentObjectGroupPython] H_element080  label="H_element : 042"  # scripted group (container) (typed FeaturePython)
  n = 8
  ref = H_element
FEATURE [App::DocumentObjectGroupPython] G4_POLYSTYRENE  # scripted group (container) (typed FeaturePython)
  Dunit = g/cm3
  Dvalue = 1.06
  Group = -> [C_element086,H_element080]
  conduct = 2
  density = 1
  expand = 3
  formula = G4_POLYSTYRENE
  name = G4_POLYSTYRENE
  specific = 4
FEATURE [App::DocumentObjectGroupPython] C_element087  label="C_element : 045"  # scripted group (container) (typed FeaturePython)
  n = 2
  ref = C_element
FEATURE [App::DocumentObjectGroupPython] F_element014  label="F_element : 4"  # scripted group (container) (typed FeaturePython)
  n = 4
  ref = F_element
FEATURE [App::DocumentObjectGroupPython] G4_TEFLON  # scripted group (container) (typed FeaturePython)
  Dunit = g/cm3
  Dvalue = 2.2
  Group = -> [C_element087,F_element014]
  conduct = 2
  density = 1
  expand = 3
  formula = G4_TEFLON
  name = G4_TEFLON
  specific = 4
FEATURE [App::DocumentObjectGroupPython] C_element088  label="C_element : 046"  # scripted group (container) (typed FeaturePython)
  n = 2
  ref = C_element
FEATURE [App::DocumentObjectGroupPython] F_element015  label="F_element : 006"  # scripted group (container) (typed FeaturePython)
  n = 3
  ref = F_element
FEATURE [App::DocumentObjectGroupPython] Cl_element018  label="Cl_element : 008"  # scripted group (container) (typed FeaturePython)
  n = 1
  ref = Cl_element
FEATURE [App::DocumentObjectGroupPython] G4_POLYTRIFLUOROCHLOROETHYLENE  # scripted group (container) (typed FeaturePython)
  Dunit = g/cm3
  Dvalue = 2.1
  Group = -> [C_element088,F_element015,Cl_element018]
  conduct = 2
  density = 1
  expand = 3
  formula = G4_POLYTRIFLUOROCHLOROETHYLENE
  name = G4_POLYTRIFLUOROCHLOROETHYLENE
  specific = 4
FEATURE [App::DocumentObjectGroupPython] C_element089  label="C_element : 047"  # scripted group (container) (typed FeaturePython)
  n = 4
  ref = C_element
FEATURE [App::DocumentObjectGroupPython] H_element081  label="H_element : 043"  # scripted group (container) (typed FeaturePython)
  n = 6
  ref = H_element
FEATURE [App::DocumentObjectGroupPython] O_element081  label="O_element : 042"  # scripted group (container) (typed FeaturePython)
  n = 2
  ref = O_element
FEATURE [App::DocumentObjectGroupPython] G4_POLYVINYL_ACETATE  # scripted group (container) (typed FeaturePython)
  Dunit = g/cm3
  Dvalue = 1.19
  Group = -> [C_element089,H_element081,O_element081]
  conduct = 2
  density = 1
  expand = 3
  formula = G4_POLYVINYL_ACETATE
  name = G4_POLYVINYL_ACETATE
  specific = 4
FEATURE [App::DocumentObjectGroupPython] C_element090  label="C_element : 048"  # scripted group (container) (typed FeaturePython)
  n = 2
  ref = C_element
FEATURE [App::DocumentObjectGroupPython] H_element082  label="H_element : 044"  # scripted group (container) (typed FeaturePython)
  n = 4
  ref = H_element
FEATURE [App::DocumentObjectGroupPython] O_element082  label="O_element : 043"  # scripted group (container) (typed FeaturePython)
  n = 1
  ref = O_element
FEATURE [App::DocumentObjectGroupPython] G4_POLYVINYL_ALCOHOL  # scripted group (container) (typed FeaturePython)
  Dunit = g/cm3
  Dvalue = 1.3
  Group = -> [C_element090,H_element082,O_element082]
  conduct = 2
  density = 1
  expand = 3
  formula = G4_POLYVINYL_ALCOHOL
  name = G4_POLYVINYL_ALCOHOL
  specific = 4
FEATURE [App::DocumentObjectGroupPython] C_element091  label="C_element : 049"  # scripted group (container) (typed FeaturePython)
  n = 8
  ref = C_element
FEATURE [App::DocumentObjectGroupPython] H_element083  label="H_element : 045"  # scripted group (container) (typed FeaturePython)
  n = 14
  ref = H_element
FEATURE [App::DocumentObjectGroupPython] O_element083  label="O_element : 044"  # scripted group (container) (typed FeaturePython)
  n = 2
  ref = O_element
FEATURE [App::DocumentObjectGroupPython] G4_POLYVINYL_BUTYRAL  # scripted group (container) (typed FeaturePython)
  Dunit = g/cm3
  Dvalue = 1.12
  Group = -> [C_element091,H_element083,O_element083]
  conduct = 2
  density = 1
  expand = 3
  formula = G4_POLYVINYL_BUTYRAL
  name = G4_POLYVINYL_BUTYRAL
  specific = 4
FEATURE [App::DocumentObjectGroupPython] C_element092  label="C_element : 050"  # scripted group (container) (typed FeaturePython)
  n = 2
  ref = C_element
FEATURE [App::DocumentObjectGroupPython] H_element084  label="H_element : 046"  # scripted group (container) (typed FeaturePython)
  n = 3
  ref = H_element
FEATURE [App::DocumentObjectGroupPython] Cl_element019  label="Cl_element : 009"  # scripted group (container) (typed FeaturePython)
  n = 1
  ref = Cl_element
FEATURE [App::DocumentObjectGroupPython] G4_POLYVINYL_CHLORIDE  # scripted group (container) (typed FeaturePython)
  Dunit = g/cm3
  Dvalue = 1.3
  Group = -> [C_element092,H_element084,Cl_element019]
  conduct = 2
  density = 1
  expand = 3
  formula = G4_POLYVINYL_CHLORIDE
  name = G4_POLYVINYL_CHLORIDE
  specific = 4
FEATURE [App::DocumentObjectGroupPython] C_element093  label="C_element : 051"  # scripted group (container) (typed FeaturePython)
  n = 2
  ref = C_element
FEATURE [App::DocumentObjectGroupPython] H_element085  label="H_element : 047"  # scripted group (container) (typed FeaturePython)
  n = 2
  ref = H_element
FEATURE [App::DocumentObjectGroupPython] Cl_element020  label="Cl_element : 010"  # scripted group (container) (typed FeaturePython)
  n = 2
  ref = Cl_element
FEATURE [App::DocumentObjectGroupPython] G4_POLYVINYLIDENE_CHLORIDE  # scripted group (container) (typed FeaturePython)
  Dunit = g/cm3
  Dvalue = 1.7
  Group = -> [C_element093,H_element085,Cl_element020]
  conduct = 2
  density = 1
  expand = 3
  formula = G4_POLYVINYLIDENE_CHLORIDE
  name = G4_POLYVINYLIDENE_CHLORIDE
  specific = 4
FEATURE [App::DocumentObjectGroupPython] C_element094  label="C_element : 052"  # scripted group (container) (typed FeaturePython)
  n = 2
  ref = C_element
FEATURE [App::DocumentObjectGroupPython] H_element086  label="H_element : 048"  # scripted group (container) (typed FeaturePython)
  n = 2
  ref = H_element
FEATURE [App::DocumentObjectGroupPython] F_element016  label="F_element : 007"  # scripted group (container) (typed FeaturePython)
  n = 2
  ref = F_element
FEATURE [App::DocumentObjectGroupPython] G4_POLYVINYLIDENE_FLUORIDE  # scripted group (container) (typed FeaturePython)
  Dunit = g/cm3
  Dvalue = 1.76
  Group = -> [C_element094,H_element086,F_element016]
  conduct = 2
  density = 1
  expand = 3
  formula = G4_POLYVINYLIDENE_FLUORIDE
  name = G4_POLYVINYLIDENE_FLUORIDE
  specific = 4
FEATURE [App::DocumentObjectGroupPython] C_element095  label="C_element : 053"  # scripted group (container) (typed FeaturePython)
  n = 6
  ref = C_element
FEATURE [App::DocumentObjectGroupPython] H_element087  label="H_element : 9"  # scripted group (container) (typed FeaturePython)
  n = 9
  ref = H_element
FEATURE [App::DocumentObjectGroupPython] N_element037  label="N_element : 016"  # scripted group (container) (typed FeaturePython)
  n = 1
  ref = N_element
FEATURE [App::DocumentObjectGroupPython] O_element084  label="O_element : 045"  # scripted group (container) (typed FeaturePython)
  n = 1
  ref = O_element
FEATURE [App::DocumentObjectGroupPython] G4_POLYVINYL_PYRROLIDONE  # scripted group (container) (typed FeaturePython)
  Dunit = g/cm3
  Dvalue = 1.25
  Group = -> [C_element095,H_element087,N_element037,O_element084]
  conduct = 2
  density = 1
  expand = 3
  formula = G4_POLYVINYL_PYRROLIDONE
  name = G4_POLYVINYL_PYRROLIDONE
  specific = 4
FEATURE [App::DocumentObjectGroupPython] K_element008  label="K_element : 1"  # scripted group (container) (typed FeaturePython)
  n = 1
  ref = K_element
FEATURE [App::DocumentObjectGroupPython] I_element006  label="I_element : 003"  # scripted group (container) (typed FeaturePython)
  n = 1
  ref = I_element
FEATURE [App::DocumentObjectGroupPython] G4_POTASSIUM_IODIDE  # scripted group (container) (typed FeaturePython)
  Dunit = g/cm3
  Dvalue = 3.13
  Group = -> [K_element008,I_element006]
  conduct = 2
  density = 1
  expand = 3
  formula = G4_POTASSIUM_IODIDE
  name = G4_POTASSIUM_IODIDE
  specific = 4
FEATURE [App::DocumentObjectGroupPython] K_element009  label="K_element : 2"  # scripted group (container) (typed FeaturePython)
  n = 2
  ref = K_element
FEATURE [App::DocumentObjectGroupPython] O_element085  label="O_element : 046"  # scripted group (container) (typed FeaturePython)
  n = 1
  ref = O_element
FEATURE [App::DocumentObjectGroupPython] G4_POTASSIUM_OXIDE  # scripted group (container) (typed FeaturePython)
  Dunit = g/cm3
  Dvalue = 2.32
  Group = -> [K_element009,O_element085]
  conduct = 2
  density = 1
  expand = 3
  formula = G4_POTASSIUM_OXIDE
  name = G4_POTASSIUM_OXIDE
  specific = 4
FEATURE [App::DocumentObjectGroupPython] C_element096  label="C_element : 054"  # scripted group (container) (typed FeaturePython)
  n = 3
  ref = C_element
FEATURE [App::DocumentObjectGroupPython] H_element088  label="H_element : 049"  # scripted group (container) (typed FeaturePython)
  n = 8
  ref = H_element
FEATURE [App::DocumentObjectGroupPython] G4_PROPANE  # scripted group (container) (typed FeaturePython)
  Dunit = g/cm3
  Dvalue = 0.00187939
  Group = -> [C_element096,H_element088]
  conduct = 2
  density = 1
  expand = 3
  formula = G4_PROPANE
  name = G4_PROPANE
  specific = 4
FEATURE [App::DocumentObjectGroupPython] C_element097  label="C_element : 055"  # scripted group (container) (typed FeaturePython)
  n = 3
  ref = C_element
FEATURE [App::DocumentObjectGroupPython] H_element089  label="H_element : 050"  # scripted group (container) (typed FeaturePython)
  n = 8
  ref = H_element
FEATURE [App::DocumentObjectGroupPython] G4_lPROPANE  # scripted group (container) (typed FeaturePython)
  Dunit = g/cm3
  Dvalue = 0.43
  Group = -> [C_element097,H_element089]
  conduct = 2
  density = 1
  expand = 3
  formula = G4_lPROPANE
  name = G4_lPROPANE
  specific = 4
FEATURE [App::DocumentObjectGroupPython] C_element098  label="C_element : 056"  # scripted group (container) (typed FeaturePython)
  n = 3
  ref = C_element
FEATURE [App::DocumentObjectGroupPython] H_element090  label="H_element : 051"  # scripted group (container) (typed FeaturePython)
  n = 8
  ref = H_element
FEATURE [App::DocumentObjectGroupPython] O_element086  label="O_element : 047"  # scripted group (container) (typed FeaturePython)
  n = 1
  ref = O_element
FEATURE [App::DocumentObjectGroupPython] G4_N_PROPYL_ALCOHOL  label="G4_N-PROPYL_ALCOHOL"  # scripted group (container) (typed FeaturePython)
  Dunit = g/cm3
  Dvalue = 0.8035
  Group = -> [C_element098,H_element090,O_element086]
  conduct = 2
  density = 1
  expand = 3
  formula = G4_N-PROPYL_ALCOHOL
  name = G4_N-PROPYL_ALCOHOL
  specific = 4
FEATURE [App::DocumentObjectGroupPython] C_element099  label="C_element : 057"  # scripted group (container) (typed FeaturePython)
  n = 5
  ref = C_element
FEATURE [App::DocumentObjectGroupPython] H_element091  label="H_element : 052"  # scripted group (container) (typed FeaturePython)
  n = 5
  ref = H_element
FEATURE [App::DocumentObjectGroupPython] N_element038  label="N_element : 017"  # scripted group (container) (typed FeaturePython)
  n = 1
  ref = N_element
FEATURE [App::DocumentObjectGroupPython] G4_PYRIDINE  # scripted group (container) (typed FeaturePython)
  Dunit = g/cm3
  Dvalue = 0.9819
  Group = -> [C_element099,H_element091,N_element038]
  conduct = 2
  density = 1
  expand = 3
  formula = G4_PYRIDINE
  name = G4_PYRIDINE
  specific = 4
FEATURE [App::DocumentObjectGroupPython] H_element092  label="H_element : 0.144"  # scripted group (container) (typed FeaturePython)
  n = 0.143711
FEATURE [App::DocumentObjectGroupPython] C_element100  label="C_element : 0.856"  # scripted group (container) (typed FeaturePython)
  n = 0.856289
FEATURE [App::DocumentObjectGroupPython] G4_RUBBER_BUTYL  # scripted group (container) (typed FeaturePython)
  Dunit = g/cm3
  Dvalue = 0.92
  Group = -> [H_element092,C_element100]
  conduct = 2
  density = 1
  expand = 3
  formula = G4_RUBBER_BUTYL
  name = G4_RUBBER_BUTYL
  specific = 4
FEATURE [App::DocumentObjectGroupPython] H_element093  label="H_element : 0.118"  # scripted group (container) (typed FeaturePython)
  n = 0.118371
FEATURE [App::DocumentObjectGroupPython] C_element101  label="C_element : 0.882"  # scripted group (container) (typed FeaturePython)
  n = 0.881629
FEATURE [App::DocumentObjectGroupPython] G4_RUBBER_NATURAL  # scripted group (container) (typed FeaturePython)
  Dunit = g/cm3
  Dvalue = 0.92
  Group = -> [H_element093,C_element101]
  conduct = 2
  density = 1
  expand = 3
  formula = G4_RUBBER_NATURAL
  name = G4_RUBBER_NATURAL
  specific = 4
FEATURE [App::DocumentObjectGroupPython] H_element094  label="H_element : 0.145"  # scripted group (container) (typed FeaturePython)
  n = 0.05692
FEATURE [App::DocumentObjectGroupPython] C_element102  label="C_element : 0.543"  # scripted group (container) (typed FeaturePython)
  n = 0.542646
FEATURE [App::DocumentObjectGroupPython] Cl_element021  label="Cl_element : 0.400"  # scripted group (container) (typed FeaturePython)
  n = 0.400434
FEATURE [App::DocumentObjectGroupPython] G4_RUBBER_NEOPRENE  # scripted group (container) (typed FeaturePython)
  Dunit = g/cm3
  Dvalue = 1.23
  Group = -> [H_element094,C_element102,Cl_element021]
  conduct = 2
  density = 1
  expand = 3
  formula = G4_RUBBER_NEOPRENE
  name = G4_RUBBER_NEOPRENE
  specific = 4
FEATURE [App::DocumentObjectGroupPython] Si_element006  label="Si_element : 1"  # scripted group (container) (typed FeaturePython)
  n = 1
  ref = Si_element
FEATURE [App::DocumentObjectGroupPython] O_element087  label="O_element : 048"  # scripted group (container) (typed FeaturePython)
  n = 2
  ref = O_element
FEATURE [App::DocumentObjectGroupPython] G4_SILICON_DIOXIDE  # scripted group (container) (typed FeaturePython)
  Dunit = g/cm3
  Dvalue = 2.32
  Group = -> [Si_element006,O_element087]
  conduct = 2
  density = 1
  expand = 3
  formula = G4_SILICON_DIOXIDE
  name = G4_SILICON_DIOXIDE
  specific = 4
FEATURE [App::DocumentObjectGroupPython] Ag_element002  label="Ag_element : 1"  # scripted group (container) (typed FeaturePython)
  n = 1
  ref = Ag_element
FEATURE [App::DocumentObjectGroupPython] Br_element005  label="Br_element : 003"  # scripted group (container) (typed FeaturePython)
  n = 1
  ref = Br_element
FEATURE [App::DocumentObjectGroupPython] G4_SILVER_BROMIDE  # scripted group (container) (typed FeaturePython)
  Dunit = g/cm3
  Dvalue = 6.473
  Group = -> [Ag_element002,Br_element005]
  conduct = 2
  density = 1
  expand = 3
  formula = G4_SILVER_BROMIDE
  name = G4_SILVER_BROMIDE
  specific = 4
FEATURE [App::DocumentObjectGroupPython] Ag_element003  label="Ag_element : 002"  # scripted group (container) (typed FeaturePython)
  n = 1
  ref = Ag_element
FEATURE [App::DocumentObjectGroupPython] Cl_element022  label="Cl_element : 011"  # scripted group (container) (typed FeaturePython)
  n = 1
  ref = Cl_element
FEATURE [App::DocumentObjectGroupPython] G4_SILVER_CHLORIDE  # scripted group (container) (typed FeaturePython)
  Dunit = g/cm3
  Dvalue = 5.56
  Group = -> [Ag_element003,Cl_element022]
  conduct = 2
  density = 1
  expand = 3
  formula = G4_SILVER_CHLORIDE
  name = G4_SILVER_CHLORIDE
  specific = 4
FEATURE [App::DocumentObjectGroupPython] Br_element006  label="Br_element : 0.423"  # scripted group (container) (typed FeaturePython)
  n = 0.422895
FEATURE [App::DocumentObjectGroupPython] Ag_element004  label="Ag_element : 0.574"  # scripted group (container) (typed FeaturePython)
  n = 0.573748
FEATURE [App::DocumentObjectGroupPython] I_element007  label="I_element : 0.649"  # scripted group (container) (typed FeaturePython)
  n = 0.003357
FEATURE [App::DocumentObjectGroupPython] G4_SILVER_HALIDES  # scripted group (container) (typed FeaturePython)
  Dunit = g/cm3
  Dvalue = 6.47
  Group = -> [Br_element006,Ag_element004,I_element007]
  conduct = 2
  density = 1
  expand = 3
  formula = G4_SILVER_HALIDES
  name = G4_SILVER_HALIDES
  specific = 4
FEATURE [App::DocumentObjectGroupPython] Ag_element005  label="Ag_element : 003"  # scripted group (container) (typed FeaturePython)
  n = 1
  ref = Ag_element
FEATURE [App::DocumentObjectGroupPython] I_element008  label="I_element : 004"  # scripted group (container) (typed FeaturePython)
  n = 1
  ref = I_element
FEATURE [App::DocumentObjectGroupPython] G4_SILVER_IODIDE  # scripted group (container) (typed FeaturePython)
  Dunit = g/cm3
  Dvalue = 6.01
  Group = -> [Ag_element005,I_element008]
  conduct = 2
  density = 1
  expand = 3
  formula = G4_SILVER_IODIDE
  name = G4_SILVER_IODIDE
  specific = 4
FEATURE [App::DocumentObjectGroupPython] H_element095  label="H_element : 0.100"  # scripted group (container) (typed FeaturePython)
  n = 0.1
FEATURE [App::DocumentObjectGroupPython] C_element103  label="C_element : 0.204"  # scripted group (container) (typed FeaturePython)
  n = 0.204
FEATURE [App::DocumentObjectGroupPython] N_element039  label="N_element : 0.759"  # scripted group (container) (typed FeaturePython)
  n = 0.042
FEATURE [App::DocumentObjectGroupPython] O_element088  label="O_element : 0.645"  # scripted group (container) (typed FeaturePython)
  n = 0.645
FEATURE [App::DocumentObjectGroupPython] Na_element013  label="Na_element : 0.100"  # scripted group (container) (typed FeaturePython)
  n = 0.002
FEATURE [App::DocumentObjectGroupPython] P_element009  label="P_element : 0.107"  # scripted group (container) (typed FeaturePython)
  n = 0.001
FEATURE [App::DocumentObjectGroupPython] S_element020  label="S_element : 0.021"  # scripted group (container) (typed FeaturePython)
  n = 0.002
FEATURE [App::DocumentObjectGroupPython] Cl_element023  label="Cl_element : 0.590"  # scripted group (container) (typed FeaturePython)
  n = 0.003
FEATURE [App::DocumentObjectGroupPython] K_element010  label="K_element : 0.001"  # scripted group (container) (typed FeaturePython)
  n = 0.001
FEATURE [App::DocumentObjectGroupPython] G4_SKIN_ICRP  # scripted group (container) (typed FeaturePython)
  Dunit = g/cm3
  Dvalue = 1.09
  Group = -> [H_element095,C_element103,N_element039,O_element088,Na_element013,P_element009,S_element020,Cl_element023,K_element010]
  conduct = 2
  density = 1
  expand = 3
  formula = G4_SKIN_ICRP
  name = G4_SKIN_ICRP
  specific = 4
FEATURE [App::DocumentObjectGroupPython] Na_element014  label="Na_element : 2"  # scripted group (container) (typed FeaturePython)
  n = 2
  ref = Na_element
FEATURE [App::DocumentObjectGroupPython] C_element104  label="C_element : 058"  # scripted group (container) (typed FeaturePython)
  n = 1
  ref = C_element
FEATURE [App::DocumentObjectGroupPython] O_element089  label="O_element : 049"  # scripted group (container) (typed FeaturePython)
  n = 3
  ref = O_element
FEATURE [App::DocumentObjectGroupPython] G4_SODIUM_CARBONATE  # scripted group (container) (typed FeaturePython)
  Dunit = g/cm3
  Dvalue = 2.532
  Group = -> [Na_element014,C_element104,O_element089]
  conduct = 2
  density = 1
  expand = 3
  formula = G4_SODIUM_CARBONATE
  name = G4_SODIUM_CARBONATE
  specific = 4
FEATURE [App::DocumentObjectGroupPython] Na_element015  label="Na_element : 1"  # scripted group (container) (typed FeaturePython)
  n = 1
  ref = Na_element
FEATURE [App::DocumentObjectGroupPython] I_element009  label="I_element : 005"  # scripted group (container) (typed FeaturePython)
  n = 1
  ref = I_element
FEATURE [App::DocumentObjectGroupPython] G4_SODIUM_IODIDE  # scripted group (container) (typed FeaturePython)
  Dunit = g/cm3
  Dvalue = 3.667
  Group = -> [Na_element015,I_element009]
  conduct = 2
  density = 1
  expand = 3
  formula = G4_SODIUM_IODIDE
  name = G4_SODIUM_IODIDE
  specific = 4
FEATURE [App::DocumentObjectGroupPython] Na_element016  label="Na_element : 003"  # scripted group (container) (typed FeaturePython)
  n = 2
  ref = Na_element
FEATURE [App::DocumentObjectGroupPython] O_element090  label="O_element : 050"  # scripted group (container) (typed FeaturePython)
  n = 1
  ref = O_element
FEATURE [App::DocumentObjectGroupPython] G4_SODIUM_MONOXIDE  # scripted group (container) (typed FeaturePython)
  Dunit = g/cm3
  Dvalue = 2.27
  Group = -> [Na_element016,O_element090]
  conduct = 2
  density = 1
  expand = 3
  formula = G4_SODIUM_MONOXIDE
  name = G4_SODIUM_MONOXIDE
  specific = 4
FEATURE [App::DocumentObjectGroupPython] Na_element017  label="Na_element : 004"  # scripted group (container) (typed FeaturePython)
  n = 1
  ref = Na_element
FEATURE [App::DocumentObjectGroupPython] N_element040  label="N_element : 018"  # scripted group (container) (typed FeaturePython)
  n = 1
  ref = N_element
FEATURE [App::DocumentObjectGroupPython] O_element091  label="O_element : 051"  # scripted group (container) (typed FeaturePython)
  n = 3
  ref = O_element
FEATURE [App::DocumentObjectGroupPython] G4_SODIUM_NITRATE  # scripted group (container) (typed FeaturePython)
  Dunit = g/cm3
  Dvalue = 2.261
  Group = -> [Na_element017,N_element040,O_element091]
  conduct = 2
  density = 1
  expand = 3
  formula = G4_SODIUM_NITRATE
  name = G4_SODIUM_NITRATE
  specific = 4
FEATURE [App::DocumentObjectGroupPython] C_element105  label="C_element : 059"  # scripted group (container) (typed FeaturePython)
  n = 14
  ref = C_element
FEATURE [App::DocumentObjectGroupPython] H_element096  label="H_element : 053"  # scripted group (container) (typed FeaturePython)
  n = 12
  ref = H_element
FEATURE [App::DocumentObjectGroupPython] G4_STILBENE  # scripted group (container) (typed FeaturePython)
  Dunit = g/cm3
  Dvalue = 0.9707
  Group = -> [C_element105,H_element096]
  conduct = 2
  density = 1
  expand = 3
  formula = G4_STILBENE
  name = G4_STILBENE
  specific = 4
FEATURE [App::DocumentObjectGroupPython] C_element106  label="C_element : 12"  # scripted group (container) (typed FeaturePython)
  n = 12
  ref = C_element
FEATURE [App::DocumentObjectGroupPython] H_element097  label="H_element : 22"  # scripted group (container) (typed FeaturePython)
  n = 22
  ref = H_element
FEATURE [App::DocumentObjectGroupPython] O_element092  label="O_element : 11"  # scripted group (container) (typed FeaturePython)
  n = 11
  ref = O_element
FEATURE [App::DocumentObjectGroupPython] G4_SUCROSE  # scripted group (container) (typed FeaturePython)
  Dunit = g/cm3
  Dvalue = 1.5805
  Group = -> [C_element106,H_element097,O_element092]
  conduct = 2
  density = 1
  expand = 3
  formula = G4_SUCROSE
  name = G4_SUCROSE
  specific = 4
FEATURE [App::DocumentObjectGroupPython] C_element107  label="C_element : 18"  # scripted group (container) (typed FeaturePython)
  n = 18
  ref = C_element
FEATURE [App::DocumentObjectGroupPython] H_element098  label="H_element : 054"  # scripted group (container) (typed FeaturePython)
  n = 14
  ref = H_element
FEATURE [App::DocumentObjectGroupPython] G4_TERPHENYL  # scripted group (container) (typed FeaturePython)
  Dunit = g/cm3
  Dvalue = 1.24
  Group = -> [C_element107,H_element098]
  conduct = 2
  density = 1
  expand = 3
  formula = G4_TERPHENYL
  name = G4_TERPHENYL
  specific = 4
FEATURE [App::DocumentObjectGroupPython] H_element099  label="H_element : 0.146"  # scripted group (container) (typed FeaturePython)
  n = 0.106
FEATURE [App::DocumentObjectGroupPython] C_element108  label="C_element : 0.883"  # scripted group (container) (typed FeaturePython)
  n = 0.099
FEATURE [App::DocumentObjectGroupPython] N_element041  label="N_element : 0.020"  # scripted group (container) (typed FeaturePython)
  n = 0.02
FEATURE [App::DocumentObjectGroupPython] O_element093  label="O_element : 0.766"  # scripted group (container) (typed FeaturePython)
  n = 0.766
FEATURE [App::DocumentObjectGroupPython] Na_element018  label="Na_element : 0.101"  # scripted group (container) (typed FeaturePython)
  n = 0.002
FEATURE [App::DocumentObjectGroupPython] P_element010  label="P_element : 0.108"  # scripted group (container) (typed FeaturePython)
  n = 0.001
FEATURE [App::DocumentObjectGroupPython] S_element021  label="S_element : 0.022"  # scripted group (container) (typed FeaturePython)
  n = 0.002
FEATURE [App::DocumentObjectGroupPython] Cl_element024  label="Cl_element : 0.002"  # scripted group (container) (typed FeaturePython)
  n = 0.002
FEATURE [App::DocumentObjectGroupPython] K_element011  label="K_element : 0.017"  # scripted group (container) (typed FeaturePython)
  n = 0.002
FEATURE [App::DocumentObjectGroupPython] G4_TESTIS_ICRP  # scripted group (container) (typed FeaturePython)
  Dunit = g/cm3
  Dvalue = 1.04
  Group = -> [H_element099,C_element108,N_element041,O_element093,Na_element018,P_element010,S_element021,Cl_element024,K_element011]
  conduct = 2
  density = 1
  expand = 3
  formula = G4_TESTIS_ICRP
  name = G4_TESTIS_ICRP
  specific = 4
FEATURE [App::DocumentObjectGroupPython] C_element109  label="C_element : 060"  # scripted group (container) (typed FeaturePython)
  n = 2
  ref = C_element
FEATURE [App::DocumentObjectGroupPython] Cl_element025  label="Cl_element : 012"  # scripted group (container) (typed FeaturePython)
  n = 4
  ref = Cl_element
FEATURE [App::DocumentObjectGroupPython] G4_TETRACHLOROETHYLENE  # scripted group (container) (typed FeaturePython)
  Dunit = g/cm3
  Dvalue = 1.625
  Group = -> [C_element109,Cl_element025]
  conduct = 2
  density = 1
  expand = 3
  formula = G4_TETRACHLOROETHYLENE
  name = G4_TETRACHLOROETHYLENE
  specific = 4
FEATURE [App::DocumentObjectGroupPython] Tl_element001  label="Tl_element : 1"  # scripted group (container) (typed FeaturePython)
  n = 1
  ref = Tl_element
FEATURE [App::DocumentObjectGroupPython] Cl_element026  label="Cl_element : 013"  # scripted group (container) (typed FeaturePython)
  n = 1
  ref = Cl_element
FEATURE [App::DocumentObjectGroupPython] G4_THALLIUM_CHLORIDE  # scripted group (container) (typed FeaturePython)
  Dunit = g/cm3
  Dvalue = 7.004
  Group = -> [Tl_element001,Cl_element026]
  conduct = 2
  density = 1
  expand = 3
  formula = G4_THALLIUM_CHLORIDE
  name = G4_THALLIUM_CHLORIDE
  specific = 4
FEATURE [App::DocumentObjectGroupPython] H_element100  label="H_element : 0.147"  # scripted group (container) (typed FeaturePython)
  n = 0.105
FEATURE [App::DocumentObjectGroupPython] C_element110  label="C_element : 0.256"  # scripted group (container) (typed FeaturePython)
  n = 0.256
FEATURE [App::DocumentObjectGroupPython] N_element042  label="N_element : 0.760"  # scripted group (container) (typed FeaturePython)
  n = 0.027
FEATURE [App::DocumentObjectGroupPython] O_element094  label="O_element : 0.602"  # scripted group (container) (typed FeaturePython)
  n = 0.602
FEATURE [App::DocumentObjectGroupPython] Na_element019  label="Na_element : 0.102"  # scripted group (container) (typed FeaturePython)
  n = 0.001
FEATURE [App::DocumentObjectGroupPython] P_element011  label="P_element : 0.109"  # scripted group (container) (typed FeaturePython)
  n = 0.002
FEATURE [App::DocumentObjectGroupPython] S_element022  label="S_element : 0.023"  # scripted group (container) (typed FeaturePython)
  n = 0.003
FEATURE [App::DocumentObjectGroupPython] Cl_element027  label="Cl_element : 0.591"  # scripted group (container) (typed FeaturePython)
  n = 0.002
FEATURE [App::DocumentObjectGroupPython] K_element012  label="K_element : 0.018"  # scripted group (container) (typed FeaturePython)
  n = 0.002
FEATURE [App::DocumentObjectGroupPython] G4_TISSUE_SOFT_ICRP  # scripted group (container) (typed FeaturePython)
  Dunit = g/cm3
  Dvalue = 1.03
  Group = -> [H_element100,C_element110,N_element042,O_element094,Na_element019,P_element011,S_element022,Cl_element027,K_element012]
  conduct = 2
  density = 1
  expand = 3
  formula = G4_TISSUE_SOFT_ICRP
  name = G4_TISSUE_SOFT_ICRP
  specific = 4
FEATURE [App::DocumentObjectGroupPython] H_element101  label="H_element : 0.148"  # scripted group (container) (typed FeaturePython)
  n = 0.101
FEATURE [App::DocumentObjectGroupPython] C_element111  label="C_element : 0.111"  # scripted group (container) (typed FeaturePython)
  n = 0.111
FEATURE [App::DocumentObjectGroupPython] N_element043  label="N_element : 0.026"  # scripted group (container) (typed FeaturePython)
  n = 0.026
FEATURE [App::DocumentObjectGroupPython] O_element095  label="O_element : 0.762"  # scripted group (container) (typed FeaturePython)
  n = 0.762
FEATURE [App::DocumentObjectGroupPython] G4_TISSUE_SOFT_ICRU_4  label="G4_TISSUE_SOFT_ICRU-4"  # scripted group (container) (typed FeaturePython)
  Dunit = g/cm3
  Dvalue = 1
  Group = -> [H_element101,C_element111,N_element043,O_element095]
  conduct = 2
  density = 1
  expand = 3
  formula = G4_TISSUE_SOFT_ICRU-4
  name = G4_TISSUE_SOFT_ICRU-4
  specific = 4
FEATURE [App::DocumentObjectGroupPython] H_element102  label="H_element : 0.149"  # scripted group (container) (typed FeaturePython)
  n = 0.101869
FEATURE [App::DocumentObjectGroupPython] C_element112  label="C_element : 0.456"  # scripted group (container) (typed FeaturePython)
  n = 0.456179
FEATURE [App::DocumentObjectGroupPython] N_element044  label="N_element : 0.761"  # scripted group (container) (typed FeaturePython)
  n = 0.035172
FEATURE [App::DocumentObjectGroupPython] O_element096  label="O_element : 0.407"  # scripted group (container) (typed FeaturePython)
  n = 0.40678
FEATURE [App::DocumentObjectGroupPython] G4_TISSUE_METHANE  label="G4_TISSUE-METHANE"  # scripted group (container) (typed FeaturePython)
  Dunit = g/cm3
  Dvalue = 0.00106409
  Group = -> [H_element102,C_element112,N_element044,O_element096]
  conduct = 2
  density = 1
  expand = 3
  formula = G4_TISSUE-METHANE
  name = G4_TISSUE-METHANE
  specific = 4
FEATURE [App::DocumentObjectGroupPython] H_element103  label="H_element : 0.103"  # scripted group (container) (typed FeaturePython)
  n = 0.102672
FEATURE [App::DocumentObjectGroupPython] C_element113  label="C_element : 0.569"  # scripted group (container) (typed FeaturePython)
  n = 0.56894
FEATURE [App::DocumentObjectGroupPython] N_element045  label="N_element : 0.762"  # scripted group (container) (typed FeaturePython)
  n = 0.035022
FEATURE [App::DocumentObjectGroupPython] O_element097  label="O_element : 0.293"  # scripted group (container) (typed FeaturePython)
  n = 0.293366
FEATURE [App::DocumentObjectGroupPython] G4_TISSUE_PROPANE  label="G4_TISSUE-PROPANE"  # scripted group (container) (typed FeaturePython)
  Dunit = g/cm3
  Dvalue = 0.00182628
  Group = -> [H_element103,C_element113,N_element045,O_element097]
  conduct = 2
  density = 1
  expand = 3
  formula = G4_TISSUE-PROPANE
  name = G4_TISSUE-PROPANE
  specific = 4
FEATURE [App::DocumentObjectGroupPython] Ti_element003  label="Ti_element : 1"  # scripted group (container) (typed FeaturePython)
  n = 1
  ref = Ti_element
FEATURE [App::DocumentObjectGroupPython] O_element098  label="O_element : 052"  # scripted group (container) (typed FeaturePython)
  n = 2
  ref = O_element
FEATURE [App::DocumentObjectGroupPython] G4_TITANIUM_DIOXIDE  # scripted group (container) (typed FeaturePython)
  Dunit = g/cm3
  Dvalue = 4.26
  Group = -> [Ti_element003,O_element098]
  conduct = 2
  density = 1
  expand = 3
  formula = G4_TITANIUM_DIOXIDE
  name = G4_TITANIUM_DIOXIDE
  specific = 4
FEATURE [App::DocumentObjectGroupPython] C_element114  label="C_element : 061"  # scripted group (container) (typed FeaturePython)
  n = 7
  ref = C_element
FEATURE [App::DocumentObjectGroupPython] H_element104  label="H_element : 055"  # scripted group (container) (typed FeaturePython)
  n = 8
  ref = H_element
FEATURE [App::DocumentObjectGroupPython] G4_TOLUENE  # scripted group (container) (typed FeaturePython)
  Dunit = g/cm3
  Dvalue = 0.8669
  Group = -> [C_element114,H_element104]
  conduct = 2
  density = 1
  expand = 3
  formula = G4_TOLUENE
  name = G4_TOLUENE
  specific = 4
FEATURE [App::DocumentObjectGroupPython] C_element115  label="C_element : 062"  # scripted group (container) (typed FeaturePython)
  n = 2
  ref = C_element
FEATURE [App::DocumentObjectGroupPython] H_element105  label="H_element : 056"  # scripted group (container) (typed FeaturePython)
  n = 1
  ref = H_element
FEATURE [App::DocumentObjectGroupPython] Cl_element028  label="Cl_element : 014"  # scripted group (container) (typed FeaturePython)
  n = 3
  ref = Cl_element
FEATURE [App::DocumentObjectGroupPython] G4_TRICHLOROETHYLENE  # scripted group (container) (typed FeaturePython)
  Dunit = g/cm3
  Dvalue = 1.46
  Group = -> [C_element115,H_element105,Cl_element028]
  conduct = 2
  density = 1
  expand = 3
  formula = G4_TRICHLOROETHYLENE
  name = G4_TRICHLOROETHYLENE
  specific = 4
FEATURE [App::DocumentObjectGroupPython] C_element116  label="C_element : 063"  # scripted group (container) (typed FeaturePython)
  n = 6
  ref = C_element
FEATURE [App::DocumentObjectGroupPython] H_element106  label="H_element : 15"  # scripted group (container) (typed FeaturePython)
  n = 15
  ref = H_element
FEATURE [App::DocumentObjectGroupPython] O_element099  label="O_element : 053"  # scripted group (container) (typed FeaturePython)
  n = 4
  ref = O_element
FEATURE [App::DocumentObjectGroupPython] P_element012  label="P_element : 1"  # scripted group (container) (typed FeaturePython)
  n = 1
  ref = P_element
FEATURE [App::DocumentObjectGroupPython] G4_TRIETHYL_PHOSPHATE  # scripted group (container) (typed FeaturePython)
  Dunit = g/cm3
  Dvalue = 1.07
  Group = -> [C_element116,H_element106,O_element099,P_element012]
  conduct = 2
  density = 1
  expand = 3
  formula = G4_TRIETHYL_PHOSPHATE
  name = G4_TRIETHYL_PHOSPHATE
  specific = 4
FEATURE [App::DocumentObjectGroupPython] W_element003  label="W_element : 003"  # scripted group (container) (typed FeaturePython)
  n = 1
  ref = W_element
FEATURE [App::DocumentObjectGroupPython] F_element017  label="F_element : 6"  # scripted group (container) (typed FeaturePython)
  n = 6
  ref = F_element
FEATURE [App::DocumentObjectGroupPython] G4_TUNGSTEN_HEXAFLUORIDE  # scripted group (container) (typed FeaturePython)
  Dunit = g/cm3
  Dvalue = 2.4
  Group = -> [W_element003,F_element017]
  conduct = 2
  density = 1
  expand = 3
  formula = G4_TUNGSTEN_HEXAFLUORIDE
  name = G4_TUNGSTEN_HEXAFLUORIDE
  specific = 4
FEATURE [App::DocumentObjectGroupPython] U_element001  label="U_element : 1"  # scripted group (container) (typed FeaturePython)
  n = 1
  ref = U_element
FEATURE [App::DocumentObjectGroupPython] C_element117  label="C_element : 064"  # scripted group (container) (typed FeaturePython)
  n = 2
  ref = C_element
FEATURE [App::DocumentObjectGroupPython] G4_URANIUM_DICARBIDE  # scripted group (container) (typed FeaturePython)
  Dunit = g/cm3
  Dvalue = 11.28
  Group = -> [U_element001,C_element117]
  conduct = 2
  density = 1
  expand = 3
  formula = G4_URANIUM_DICARBIDE
  name = G4_URANIUM_DICARBIDE
  specific = 4
FEATURE [App::DocumentObjectGroupPython] U_element002  label="U_element : 002"  # scripted group (container) (typed FeaturePython)
  n = 1
  ref = U_element
FEATURE [App::DocumentObjectGroupPython] C_element118  label="C_element : 065"  # scripted group (container) (typed FeaturePython)
  n = 1
  ref = C_element
FEATURE [App::DocumentObjectGroupPython] G4_URANIUM_MONOCARBIDE  # scripted group (container) (typed FeaturePython)
  Dunit = g/cm3
  Dvalue = 13.63
  Group = -> [U_element002,C_element118]
  conduct = 2
  density = 1
  expand = 3
  formula = G4_URANIUM_MONOCARBIDE
  name = G4_URANIUM_MONOCARBIDE
  specific = 4
FEATURE [App::DocumentObjectGroupPython] U_element003  label="U_element : 003"  # scripted group (container) (typed FeaturePython)
  n = 1
  ref = U_element
FEATURE [App::DocumentObjectGroupPython] O_element100  label="O_element : 054"  # scripted group (container) (typed FeaturePython)
  n = 2
  ref = O_element
FEATURE [App::DocumentObjectGroupPython] G4_URANIUM_OXIDE  # scripted group (container) (typed FeaturePython)
  Dunit = g/cm3
  Dvalue = 10.96
  Group = -> [U_element003,O_element100]
  conduct = 2
  density = 1
  expand = 3
  formula = G4_URANIUM_OXIDE
  name = G4_URANIUM_OXIDE
  specific = 4
FEATURE [App::DocumentObjectGroupPython] C_element119  label="C_element : 066"  # scripted group (container) (typed FeaturePython)
  n = 1
  ref = C_element
FEATURE [App::DocumentObjectGroupPython] H_element107  label="H_element : 057"  # scripted group (container) (typed FeaturePython)
  n = 4
  ref = H_element
FEATURE [App::DocumentObjectGroupPython] N_element046  label="N_element : 019"  # scripted group (container) (typed FeaturePython)
  n = 2
  ref = N_element
FEATURE [App::DocumentObjectGroupPython] O_element101  label="O_element : 055"  # scripted group (container) (typed FeaturePython)
  n = 1
  ref = O_element
FEATURE [App::DocumentObjectGroupPython] G4_UREA  # scripted group (container) (typed FeaturePython)
  Dunit = g/cm3
  Dvalue = 1.323
  Group = -> [C_element119,H_element107,N_element046,O_element101]
  conduct = 2
  density = 1
  expand = 3
  formula = G4_UREA
  name = G4_UREA
  specific = 4
FEATURE [App::DocumentObjectGroupPython] C_element120  label="C_element : 067"  # scripted group (container) (typed FeaturePython)
  n = 5
  ref = C_element
FEATURE [App::DocumentObjectGroupPython] H_element108  label="H_element : 058"  # scripted group (container) (typed FeaturePython)
  n = 11
  ref = H_element
FEATURE [App::DocumentObjectGroupPython] N_element047  label="N_element : 020"  # scripted group (container) (typed FeaturePython)
  n = 1
  ref = N_element
FEATURE [App::DocumentObjectGroupPython] O_element102  label="O_element : 056"  # scripted group (container) (typed FeaturePython)
  n = 2
  ref = O_element
FEATURE [App::DocumentObjectGroupPython] G4_VALINE  # scripted group (container) (typed FeaturePython)
  Dunit = g/cm3
  Dvalue = 1.23
  Group = -> [C_element120,H_element108,N_element047,O_element102]
  conduct = 2
  density = 1
  expand = 3
  formula = G4_VALINE
  name = G4_VALINE
  specific = 4
FEATURE [App::DocumentObjectGroupPython] H_element109  label="H_element : 0.009"  # scripted group (container) (typed FeaturePython)
  n = 0.009417
FEATURE [App::DocumentObjectGroupPython] C_element121  label="C_element : 0.281"  # scripted group (container) (typed FeaturePython)
  n = 0.280555
FEATURE [App::DocumentObjectGroupPython] F_element018  label="F_element : 0.710"  # scripted group (container) (typed FeaturePython)
  n = 0.710028
FEATURE [App::DocumentObjectGroupPython] G4_VITON  # scripted group (container) (typed FeaturePython)
  Dunit = g/cm3
  Dvalue = 1.8
  Group = -> [H_element109,C_element121,F_element018]
  conduct = 2
  density = 1
  expand = 3
  formula = G4_VITON
  name = G4_VITON
  specific = 4
FEATURE [App::DocumentObjectGroupPython] H_element110  label="H_element : 059"  # scripted group (container) (typed FeaturePython)
  n = 2
  ref = H_element
FEATURE [App::DocumentObjectGroupPython] O_element103  label="O_element : 057"  # scripted group (container) (typed FeaturePython)
  n = 1
  ref = O_element
FEATURE [App::DocumentObjectGroupPython] G4_WATER  # scripted group (container) (typed FeaturePython)
  Dunit = g/cm3
  Dvalue = 1
  Group = -> [H_element110,O_element103]
  conduct = 2
  density = 1
  expand = 3
  formula = G4_WATER
  name = G4_WATER
  specific = 4
FEATURE [App::DocumentObjectGroupPython] H_element111  label="H_element : 060"  # scripted group (container) (typed FeaturePython)
  n = 2
  ref = H_element
FEATURE [App::DocumentObjectGroupPython] O_element104  label="O_element : 058"  # scripted group (container) (typed FeaturePython)
  n = 1
  ref = O_element
FEATURE [App::DocumentObjectGroupPython] G4_WATER_VAPOR  # scripted group (container) (typed FeaturePython)
  Dunit = g/cm3
  Dvalue = 0.000756182
  Group = -> [H_element111,O_element104]
  conduct = 2
  density = 1
  expand = 3
  formula = G4_WATER_VAPOR
  name = G4_WATER_VAPOR
  specific = 4
FEATURE [App::DocumentObjectGroupPython] C_element122  label="C_element : 068"  # scripted group (container) (typed FeaturePython)
  n = 8
  ref = C_element
FEATURE [App::DocumentObjectGroupPython] H_element112  label="H_element : 061"  # scripted group (container) (typed FeaturePython)
  n = 10
  ref = H_element
FEATURE [App::DocumentObjectGroupPython] G4_XYLENE  # scripted group (container) (typed FeaturePython)
  Dunit = g/cm3
  Dvalue = 0.87
  Group = -> [C_element122,H_element112]
  conduct = 2
  density = 1
  expand = 3
  formula = G4_XYLENE
  name = G4_XYLENE
  specific = 4
FEATURE [App::DocumentObjectGroupPython] C_element123  label="C_element : 069"  # scripted group (container) (typed FeaturePython)
  n = 1
  ref = C_element
FEATURE [App::DocumentObjectGroupPython] G4_GRAPHITE  # scripted group (container) (typed FeaturePython)
  Dunit = g/cm3
  Dvalue = 2.21
  Group = -> [C_element123]
  conduct = 2
  density = 1
  expand = 3
  formula = G4_GRAPHITE
  name = G4_GRAPHITE
  specific = 4
FEATURE [App::DocumentObjectGroupPython] NIST  # scripted group (container) (typed FeaturePython)
  Group = -> [G4_A_150_TISSUE,G4_ACETONE,G4_ACETYLENE,G4_ADENINE,G4_ADIPOSE_TISSUE_ICRP,G4_AIR,G4_ALANINE,G4_ALUMINUM_OXIDE,G4_AMBER,G4_AMMONIA,G4_ANILINE,G4_ANTHRACENE,G4_B_100_BONE,G4_BAKELITE,G4_BARIUM_FLUORIDE,G4_BARIUM_SULFATE,G4_BENZENE,G4_BERYLLIUM_OXIDE,G4_BGO,G4_BLOOD_ICRP,G4_BONE_COMPACT_ICRU,G4_BONE_CORTICAL_ICRP,G4_BORON_CARBIDE,G4_BORON_OXIDE,G4_BRAIN_ICRP,G4_BUTANE,G4_N_BUTYL_ALCOHOL,G4_C_552,+152 more]
FEATURE [App::DocumentObjectGroupPython] H_element113  label="H_element : 062"  # scripted group (container) (typed FeaturePython)
  n = 1
  ref = H_element
FEATURE [App::DocumentObjectGroupPython] G4_H  # scripted group (container) (typed FeaturePython)
  Dunit = g/cm3
  Dvalue = 8.3748e-05
  Group = -> [H_element113]
  conduct = 2
  density = 1
  expand = 3
  formula = H
  name = G4_H
  specific = 4
FEATURE [App::DocumentObjectGroupPython] He_element001  label="He_element : 1"  # scripted group (container) (typed FeaturePython)
  n = 1
  ref = He_element
FEATURE [App::DocumentObjectGroupPython] G4_He  # scripted group (container) (typed FeaturePython)
  Dunit = g/cm3
  Dvalue = 0.000166322
  Group = -> [He_element001]
  conduct = 2
  density = 1
  expand = 3
  formula = He
  name = G4_He
  specific = 4
FEATURE [App::DocumentObjectGroupPython] Li_element008  label="Li_element : 008"  # scripted group (container) (typed FeaturePython)
  n = 1
  ref = Li_element
FEATURE [App::DocumentObjectGroupPython] G4_Li  # scripted group (container) (typed FeaturePython)
  Dunit = g/cm3
  Dvalue = 0.534
  Group = -> [Li_element008]
  conduct = 2
  density = 1
  expand = 3
  formula = Li
  name = G4_Li
  specific = 4
FEATURE [App::DocumentObjectGroupPython] Be_element002  label="Be_element : 002"  # scripted group (container) (typed FeaturePython)
  n = 1
  ref = Be_element
FEATURE [App::DocumentObjectGroupPython] G4_Be  # scripted group (container) (typed FeaturePython)
  Dunit = g/cm3
  Dvalue = 1.848
  Group = -> [Be_element002]
  conduct = 2
  density = 1
  expand = 3
  formula = Be
  name = G4_Be
  specific = 4
FEATURE [App::DocumentObjectGroupPython] B_element007  label="B_element : 007"  # scripted group (container) (typed FeaturePython)
  n = 1
  ref = B_element
FEATURE [App::DocumentObjectGroupPython] G4_B  # scripted group (container) (typed FeaturePython)
  Dunit = g/cm3
  Dvalue = 2.37
  Group = -> [B_element007]
  conduct = 2
  density = 1
  expand = 3
  formula = B
  name = G4_B
  specific = 4
FEATURE [App::DocumentObjectGroupPython] C_element124  label="C_element : 070"  # scripted group (container) (typed FeaturePython)
  n = 1
  ref = C_element
FEATURE [App::DocumentObjectGroupPython] G4_C  # scripted group (container) (typed FeaturePython)
  Dunit = g/cm3
  Dvalue = 2
  Group = -> [C_element124]
  conduct = 2
  density = 1
  expand = 3
  formula = C
  name = G4_C
  specific = 4
FEATURE [App::DocumentObjectGroupPython] N_element048  label="N_element : 021"  # scripted group (container) (typed FeaturePython)
  n = 1
  ref = N_element
FEATURE [App::DocumentObjectGroupPython] G4_N  # scripted group (container) (typed FeaturePython)
  Dunit = g/cm3
  Dvalue = 0.0011652
  Group = -> [N_element048]
  conduct = 2
  density = 1
  expand = 3
  formula = N
  name = G4_N
  specific = 4
FEATURE [App::DocumentObjectGroupPython] O_element105  label="O_element : 059"  # scripted group (container) (typed FeaturePython)
  n = 1
  ref = O_element
FEATURE [App::DocumentObjectGroupPython] G4_O  # scripted group (container) (typed FeaturePython)
  Dunit = g/cm3
  Dvalue = 0.00133151
  Group = -> [O_element105]
  conduct = 2
  density = 1
  expand = 3
  formula = O
  name = G4_O
  specific = 4
FEATURE [App::DocumentObjectGroupPython] F_element019  label="F_element : 008"  # scripted group (container) (typed FeaturePython)
  n = 1
  ref = F_element
FEATURE [App::DocumentObjectGroupPython] G4_F  # scripted group (container) (typed FeaturePython)
  Dunit = g/cm3
  Dvalue = 0.00158029
  Group = -> [F_element019]
  conduct = 2
  density = 1
  expand = 3
  formula = F
  name = G4_F
  specific = 4
FEATURE [App::DocumentObjectGroupPython] Ne_element001  label="Ne_element : 1"  # scripted group (container) (typed FeaturePython)
  n = 1
  ref = Ne_element
FEATURE [App::DocumentObjectGroupPython] G4_Ne  # scripted group (container) (typed FeaturePython)
  Dunit = g/cm3
  Dvalue = 0.000838505
  Group = -> [Ne_element001]
  conduct = 2
  density = 1
  expand = 3
  formula = Ne
  name = G4_Ne
  specific = 4
FEATURE [App::DocumentObjectGroupPython] Na_element020  label="Na_element : 005"  # scripted group (container) (typed FeaturePython)
  n = 1
  ref = Na_element
FEATURE [App::DocumentObjectGroupPython] G4_Na  # scripted group (container) (typed FeaturePython)
  Dunit = g/cm3
  Dvalue = 0.971
  Group = -> [Na_element020]
  conduct = 2
  density = 1
  expand = 3
  formula = Na
  name = G4_Na
  specific = 4
FEATURE [App::DocumentObjectGroupPython] Mg_element011  label="Mg_element : 005"  # scripted group (container) (typed FeaturePython)
  n = 1
  ref = Mg_element
FEATURE [App::DocumentObjectGroupPython] G4_Mg  # scripted group (container) (typed FeaturePython)
  Dunit = g/cm3
  Dvalue = 1.74
  Group = -> [Mg_element011]
  conduct = 2
  density = 1
  expand = 3
  formula = Mg
  name = G4_Mg
  specific = 4
FEATURE [App::DocumentObjectGroupPython] Al_element004  label="Al_element : 1"  # scripted group (container) (typed FeaturePython)
  n = 1
  ref = Al_element
FEATURE [App::DocumentObjectGroupPython] G4_Al  # scripted group (container) (typed FeaturePython)
  Dunit = g/cm3
  Dvalue = 2.699
  Group = -> [Al_element004]
  conduct = 2
  density = 1
  expand = 3
  formula = Al
  name = G4_Al
  specific = 4
FEATURE [App::DocumentObjectGroupPython] Si_element007  label="Si_element : 002"  # scripted group (container) (typed FeaturePython)
  n = 1
  ref = Si_element
FEATURE [App::DocumentObjectGroupPython] G4_Si  # scripted group (container) (typed FeaturePython)
  Dunit = g/cm3
  Dvalue = 2.33
  Group = -> [Si_element007]
  conduct = 2
  density = 1
  expand = 3
  formula = Si
  name = G4_Si
  specific = 4
FEATURE [App::DocumentObjectGroupPython] P_element013  label="P_element : 002"  # scripted group (container) (typed FeaturePython)
  n = 1
  ref = P_element
FEATURE [App::DocumentObjectGroupPython] G4_P  # scripted group (container) (typed FeaturePython)
  Dunit = g/cm3
  Dvalue = 2.2
  Group = -> [P_element013]
  conduct = 2
  density = 1
  expand = 3
  formula = P
  name = G4_P
  specific = 4
FEATURE [App::DocumentObjectGroupPython] S_element023  label="S_element : 007"  # scripted group (container) (typed FeaturePython)
  n = 1
  ref = S_element
FEATURE [App::DocumentObjectGroupPython] G4_S  # scripted group (container) (typed FeaturePython)
  Dunit = g/cm3
  Dvalue = 2
  Group = -> [S_element023]
  conduct = 2
  density = 1
  expand = 3
  formula = S
  name = G4_S
  specific = 4
FEATURE [App::DocumentObjectGroupPython] Cl_element029  label="Cl_element : 015"  # scripted group (container) (typed FeaturePython)
  n = 1
  ref = Cl_element
FEATURE [App::DocumentObjectGroupPython] G4_Cl  # scripted group (container) (typed FeaturePython)
  Dunit = g/cm3
  Dvalue = 0.00299473
  Group = -> [Cl_element029]
  conduct = 2
  density = 1
  expand = 3
  formula = Cl
  name = G4_Cl
  specific = 4
FEATURE [App::DocumentObjectGroupPython] Ar_element002  label="Ar_element : 1"  # scripted group (container) (typed FeaturePython)
  n = 1
  ref = Ar_element
FEATURE [App::DocumentObjectGroupPython] G4_Ar  # scripted group (container) (typed FeaturePython)
  Dunit = g/cm3
  Dvalue = 0.00166201
  Group = -> [Ar_element002]
  conduct = 2
  density = 1
  expand = 3
  formula = Ar
  name = G4_Ar
  specific = 4
FEATURE [App::DocumentObjectGroupPython] K_element013  label="K_element : 003"  # scripted group (container) (typed FeaturePython)
  n = 1
  ref = K_element
FEATURE [App::DocumentObjectGroupPython] G4_K  # scripted group (container) (typed FeaturePython)
  Dunit = g/cm3
  Dvalue = 0.862
  Group = -> [K_element013]
  conduct = 2
  density = 1
  expand = 3
  formula = K
  name = G4_K
  specific = 4
FEATURE [App::DocumentObjectGroupPython] Ca_element014  label="Ca_element : 007"  # scripted group (container) (typed FeaturePython)
  n = 1
  ref = Ca_element
FEATURE [App::DocumentObjectGroupPython] G4_Ca  # scripted group (container) (typed FeaturePython)
  Dunit = g/cm3
  Dvalue = 1.55
  Group = -> [Ca_element014]
  conduct = 2
  density = 1
  expand = 3
  formula = Ca
  name = G4_Ca
  specific = 4
FEATURE [App::DocumentObjectGroupPython] Sc_element001  label="Sc_element : 1"  # scripted group (container) (typed FeaturePython)
  n = 1
  ref = Sc_element
FEATURE [App::DocumentObjectGroupPython] G4_Sc  # scripted group (container) (typed FeaturePython)
  Dunit = g/cm3
  Dvalue = 2.989
  Group = -> [Sc_element001]
  conduct = 2
  density = 1
  expand = 3
  formula = Sc
  name = G4_Sc
  specific = 4
FEATURE [App::DocumentObjectGroupPython] Ti_element004  label="Ti_element : 002"  # scripted group (container) (typed FeaturePython)
  n = 1
  ref = Ti_element
FEATURE [App::DocumentObjectGroupPython] G4_Ti  # scripted group (container) (typed FeaturePython)
  Dunit = g/cm3
  Dvalue = 4.54
  Group = -> [Ti_element004]
  conduct = 2
  density = 1
  expand = 3
  formula = Ti
  name = G4_Ti
  specific = 4
FEATURE [App::DocumentObjectGroupPython] V_element001  label="V_element : 1"  # scripted group (container) (typed FeaturePython)
  n = 1
  ref = V_element
FEATURE [App::DocumentObjectGroupPython] G4_V  # scripted group (container) (typed FeaturePython)
  Dunit = g/cm3
  Dvalue = 6.11
  Group = -> [V_element001]
  conduct = 2
  density = 1
  expand = 3
  formula = V
  name = G4_V
  specific = 4
FEATURE [App::DocumentObjectGroupPython] Cr_element001  label="Cr_element : 1"  # scripted group (container) (typed FeaturePython)
  n = 1
  ref = Cr_element
FEATURE [App::DocumentObjectGroupPython] G4_Cr  # scripted group (container) (typed FeaturePython)
  Dunit = g/cm3
  Dvalue = 7.18
  Group = -> [Cr_element001]
  conduct = 2
  density = 1
  expand = 3
  formula = Cr
  name = G4_Cr
  specific = 4
FEATURE [App::DocumentObjectGroupPython] Mn_element001  label="Mn_element : 1"  # scripted group (container) (typed FeaturePython)
  n = 1
  ref = Mn_element
FEATURE [App::DocumentObjectGroupPython] G4_Mn  # scripted group (container) (typed FeaturePython)
  Dunit = g/cm3
  Dvalue = 7.44
  Group = -> [Mn_element001]
  conduct = 2
  density = 1
  expand = 3
  formula = Mn
  name = G4_Mn
  specific = 4
FEATURE [App::DocumentObjectGroupPython] Fe_element007  label="Fe_element : 004"  # scripted group (container) (typed FeaturePython)
  n = 1
  ref = Fe_element
FEATURE [App::DocumentObjectGroupPython] G4_Fe  # scripted group (container) (typed FeaturePython)
  Dunit = g/cm3
  Dvalue = 7.874
  Group = -> [Fe_element007]
  conduct = 2
  density = 1
  expand = 3
  formula = Fe
  name = G4_Fe
  specific = 4
FEATURE [App::DocumentObjectGroupPython] Co_element001  label="Co_element : 1"  # scripted group (container) (typed FeaturePython)
  n = 1
  ref = Co_element
FEATURE [App::DocumentObjectGroupPython] G4_Co  # scripted group (container) (typed FeaturePython)
  Dunit = g/cm3
  Dvalue = 8.9
  Group = -> [Co_element001]
  conduct = 2
  density = 1
  expand = 3
  formula = Co
  name = G4_Co
  specific = 4
FEATURE [App::DocumentObjectGroupPython] Ni_element001  label="Ni_element : 1"  # scripted group (container) (typed FeaturePython)
  n = 1
  ref = Ni_element
FEATURE [App::DocumentObjectGroupPython] G4_Ni  # scripted group (container) (typed FeaturePython)
  Dunit = g/cm3
  Dvalue = 8.902
  Group = -> [Ni_element001]
  conduct = 2
  density = 1
  expand = 3
  formula = Ni
  name = G4_Ni
  specific = 4
FEATURE [App::DocumentObjectGroupPython] Cu_element001  label="Cu_element : 1"  # scripted group (container) (typed FeaturePython)
  n = 1
  ref = Cu_element
FEATURE [App::DocumentObjectGroupPython] G4_Cu  # scripted group (container) (typed FeaturePython)
  Dunit = g/cm3
  Dvalue = 8.96
  Group = -> [Cu_element001]
  conduct = 2
  density = 1
  expand = 3
  formula = Cu
  name = G4_Cu
  specific = 4
FEATURE [App::DocumentObjectGroupPython] Zn_element001  label="Zn_element : 1"  # scripted group (container) (typed FeaturePython)
  n = 1
  ref = Zn_element
FEATURE [App::DocumentObjectGroupPython] G4_Zn  # scripted group (container) (typed FeaturePython)
  Dunit = g/cm3
  Dvalue = 7.133
  Group = -> [Zn_element001]
  conduct = 2
  density = 1
  expand = 3
  formula = Zn
  name = G4_Zn
  specific = 4
FEATURE [App::DocumentObjectGroupPython] Ga_element002  label="Ga_element : 002"  # scripted group (container) (typed FeaturePython)
  n = 1
  ref = Ga_element
FEATURE [App::DocumentObjectGroupPython] G4_Ga  # scripted group (container) (typed FeaturePython)
  Dunit = g/cm3
  Dvalue = 5.904
  Group = -> [Ga_element002]
  conduct = 2
  density = 1
  expand = 3
  formula = Ga
  name = G4_Ga
  specific = 4
FEATURE [App::DocumentObjectGroupPython] Ge_element002  label="Ge_element : 1"  # scripted group (container) (typed FeaturePython)
  n = 1
  ref = Ge_element
FEATURE [App::DocumentObjectGroupPython] G4_Ge  # scripted group (container) (typed FeaturePython)
  Dunit = g/cm3
  Dvalue = 5.323
  Group = -> [Ge_element002]
  conduct = 2
  density = 1
  expand = 3
  formula = Ge
  name = G4_Ge
  specific = 4
FEATURE [App::DocumentObjectGroupPython] As_element003  label="As_element : 002"  # scripted group (container) (typed FeaturePython)
  n = 1
  ref = As_element
FEATURE [App::DocumentObjectGroupPython] G4_As  # scripted group (container) (typed FeaturePython)
  Dunit = g/cm3
  Dvalue = 5.73
  Group = -> [As_element003]
  conduct = 2
  density = 1
  expand = 3
  formula = As
  name = G4_As
  specific = 4
FEATURE [App::DocumentObjectGroupPython] Se_element001  label="Se_element : 1"  # scripted group (container) (typed FeaturePython)
  n = 1
  ref = Se_element
FEATURE [App::DocumentObjectGroupPython] G4_Se  # scripted group (container) (typed FeaturePython)
  Dunit = g/cm3
  Dvalue = 4.5
  Group = -> [Se_element001]
  conduct = 2
  density = 1
  expand = 3
  formula = Se
  name = G4_Se
  specific = 4
FEATURE [App::DocumentObjectGroupPython] Br_element007  label="Br_element : 004"  # scripted group (container) (typed FeaturePython)
  n = 1
  ref = Br_element
FEATURE [App::DocumentObjectGroupPython] G4_Br  # scripted group (container) (typed FeaturePython)
  Dunit = g/cm3
  Dvalue = 0.0070721
  Group = -> [Br_element007]
  conduct = 2
  density = 1
  expand = 3
  formula = Br
  name = G4_Br
  specific = 4
FEATURE [App::DocumentObjectGroupPython] Kr_element001  label="Kr_element : 1"  # scripted group (container) (typed FeaturePython)
  n = 1
  ref = Kr_element
FEATURE [App::DocumentObjectGroupPython] G4_Kr  # scripted group (container) (typed FeaturePython)
  Dunit = g/cm3
  Dvalue = 0.00347832
  Group = -> [Kr_element001]
  conduct = 2
  density = 1
  expand = 3
  formula = Kr
  name = G4_Kr
  specific = 4
FEATURE [App::DocumentObjectGroupPython] Rb_element001  label="Rb_element : 1"  # scripted group (container) (typed FeaturePython)
  n = 1
  ref = Rb_element
FEATURE [App::DocumentObjectGroupPython] G4_Rb  # scripted group (container) (typed FeaturePython)
  Dunit = g/cm3
  Dvalue = 1.532
  Group = -> [Rb_element001]
  conduct = 2
  density = 1
  expand = 3
  formula = Rb
  name = G4_Rb
  specific = 4
FEATURE [App::DocumentObjectGroupPython] Sr_element001  label="Sr_element : 1"  # scripted group (container) (typed FeaturePython)
  n = 1
  ref = Sr_element
FEATURE [App::DocumentObjectGroupPython] G4_Sr  # scripted group (container) (typed FeaturePython)
  Dunit = g/cm3
  Dvalue = 2.54
  Group = -> [Sr_element001]
  conduct = 2
  density = 1
  expand = 3
  formula = Sr
  name = G4_Sr
  specific = 4
FEATURE [App::DocumentObjectGroupPython] Y_element001  label="Y_element : 1"  # scripted group (container) (typed FeaturePython)
  n = 1
  ref = Y_element
FEATURE [App::DocumentObjectGroupPython] G4_Y  # scripted group (container) (typed FeaturePython)
  Dunit = g/cm3
  Dvalue = 4.469
  Group = -> [Y_element001]
  conduct = 2
  density = 1
  expand = 3
  formula = Y
  name = G4_Y
  specific = 4
FEATURE [App::DocumentObjectGroupPython] Zr_element001  label="Zr_element : 1"  # scripted group (container) (typed FeaturePython)
  n = 1
  ref = Zr_element
FEATURE [App::DocumentObjectGroupPython] G4_Zr  # scripted group (container) (typed FeaturePython)
  Dunit = g/cm3
  Dvalue = 6.506
  Group = -> [Zr_element001]
  conduct = 2
  density = 1
  expand = 3
  formula = Zr
  name = G4_Zr
  specific = 4
FEATURE [App::DocumentObjectGroupPython] Nb_element001  label="Nb_element : 1"  # scripted group (container) (typed FeaturePython)
  n = 1
  ref = Nb_element
FEATURE [App::DocumentObjectGroupPython] G4_Nb  # scripted group (container) (typed FeaturePython)
  Dunit = g/cm3
  Dvalue = 8.57
  Group = -> [Nb_element001]
  conduct = 2
  density = 1
  expand = 3
  formula = Nb
  name = G4_Nb
  specific = 4
FEATURE [App::DocumentObjectGroupPython] Mo_element001  label="Mo_element : 1"  # scripted group (container) (typed FeaturePython)
  n = 1
  ref = Mo_element
FEATURE [App::DocumentObjectGroupPython] G4_Mo  # scripted group (container) (typed FeaturePython)
  Dunit = g/cm3
  Dvalue = 10.22
  Group = -> [Mo_element001]
  conduct = 2
  density = 1
  expand = 3
  formula = Mo
  name = G4_Mo
  specific = 4
FEATURE [App::DocumentObjectGroupPython] Tc_element001  label="Tc_element : 1"  # scripted group (container) (typed FeaturePython)
  n = 1
  ref = Tc_element
FEATURE [App::DocumentObjectGroupPython] G4_Tc  # scripted group (container) (typed FeaturePython)
  Dunit = g/cm3
  Dvalue = 11.5
  Group = -> [Tc_element001]
  conduct = 2
  density = 1
  expand = 3
  formula = Tc
  name = G4_Tc
  specific = 4
FEATURE [App::DocumentObjectGroupPython] Ru_element001  label="Ru_element : 1"  # scripted group (container) (typed FeaturePython)
  n = 1
  ref = Ru_element
FEATURE [App::DocumentObjectGroupPython] G4_Ru  # scripted group (container) (typed FeaturePython)
  Dunit = g/cm3
  Dvalue = 12.41
  Group = -> [Ru_element001]
  conduct = 2
  density = 1
  expand = 3
  formula = Ru
  name = G4_Ru
  specific = 4
FEATURE [App::DocumentObjectGroupPython] Rh_element001  label="Rh_element : 1"  # scripted group (container) (typed FeaturePython)
  n = 1
  ref = Rh_element
FEATURE [App::DocumentObjectGroupPython] G4_Rh  # scripted group (container) (typed FeaturePython)
  Dunit = g/cm3
  Dvalue = 12.41
  Group = -> [Rh_element001]
  conduct = 2
  density = 1
  expand = 3
  formula = Rh
  name = G4_Rh
  specific = 4
FEATURE [App::DocumentObjectGroupPython] Pd_element001  label="Pd_element : 1"  # scripted group (container) (typed FeaturePython)
  n = 1
  ref = Pd_element
FEATURE [App::DocumentObjectGroupPython] G4_Pd  # scripted group (container) (typed FeaturePython)
  Dunit = g/cm3
  Dvalue = 12.02
  Group = -> [Pd_element001]
  conduct = 2
  density = 1
  expand = 3
  formula = Pd
  name = G4_Pd
  specific = 4
FEATURE [App::DocumentObjectGroupPython] Ag_element006  label="Ag_element : 004"  # scripted group (container) (typed FeaturePython)
  n = 1
  ref = Ag_element
FEATURE [App::DocumentObjectGroupPython] G4_Ag  # scripted group (container) (typed FeaturePython)
  Dunit = g/cm3
  Dvalue = 10.5
  Group = -> [Ag_element006]
  conduct = 2
  density = 1
  expand = 3
  formula = Ag
  name = G4_Ag
  specific = 4
FEATURE [App::DocumentObjectGroupPython] Cd_element003  label="Cd_element : 003"  # scripted group (container) (typed FeaturePython)
  n = 1
  ref = Cd_element
FEATURE [App::DocumentObjectGroupPython] G4_Cd  # scripted group (container) (typed FeaturePython)
  Dunit = g/cm3
  Dvalue = 8.65
  Group = -> [Cd_element003]
  conduct = 2
  density = 1
  expand = 3
  formula = Cd
  name = G4_Cd
  specific = 4
FEATURE [App::DocumentObjectGroupPython] In_element001  label="In_element : 1"  # scripted group (container) (typed FeaturePython)
  n = 1
  ref = In_element
FEATURE [App::DocumentObjectGroupPython] G4_In  # scripted group (container) (typed FeaturePython)
  Dunit = g/cm3
  Dvalue = 7.31
  Group = -> [In_element001]
  conduct = 2
  density = 1
  expand = 3
  formula = In
  name = G4_In
  specific = 4
FEATURE [App::DocumentObjectGroupPython] Sn_element001  label="Sn_element : 1"  # scripted group (container) (typed FeaturePython)
  n = 1
  ref = Sn_element
FEATURE [App::DocumentObjectGroupPython] G4_Sn  # scripted group (container) (typed FeaturePython)
  Dunit = g/cm3
  Dvalue = 7.31
  Group = -> [Sn_element001]
  conduct = 2
  density = 1
  expand = 3
  formula = Sn
  name = G4_Sn
  specific = 4
FEATURE [App::DocumentObjectGroupPython] Sb_element001  label="Sb_element : 1"  # scripted group (container) (typed FeaturePython)
  n = 1
  ref = Sb_element
FEATURE [App::DocumentObjectGroupPython] G4_Sb  # scripted group (container) (typed FeaturePython)
  Dunit = g/cm3
  Dvalue = 6.691
  Group = -> [Sb_element001]
  conduct = 2
  density = 1
  expand = 3
  formula = Sb
  name = G4_Sb
  specific = 4
FEATURE [App::DocumentObjectGroupPython] Te_element002  label="Te_element : 002"  # scripted group (container) (typed FeaturePython)
  n = 1
  ref = Te_element
FEATURE [App::DocumentObjectGroupPython] G4_Te  # scripted group (container) (typed FeaturePython)
  Dunit = g/cm3
  Dvalue = 6.24
  Group = -> [Te_element002]
  conduct = 2
  density = 1
  expand = 3
  formula = Te
  name = G4_Te
  specific = 4
FEATURE [App::DocumentObjectGroupPython] I_element010  label="I_element : 006"  # scripted group (container) (typed FeaturePython)
  n = 1
  ref = I_element
FEATURE [App::DocumentObjectGroupPython] G4_I  # scripted group (container) (typed FeaturePython)
  Dunit = g/cm3
  Dvalue = 4.93
  Group = -> [I_element010]
  conduct = 2
  density = 1
  expand = 3
  formula = I
  name = G4_I
  specific = 4
FEATURE [App::DocumentObjectGroupPython] Xe_element001  label="Xe_element : 1"  # scripted group (container) (typed FeaturePython)
  n = 1
  ref = Xe_element
FEATURE [App::DocumentObjectGroupPython] G4_Xe  # scripted group (container) (typed FeaturePython)
  Dunit = g/cm3
  Dvalue = 0.00548536
  Group = -> [Xe_element001]
  conduct = 2
  density = 1
  expand = 3
  formula = Xe
  name = G4_Xe
  specific = 4
FEATURE [App::DocumentObjectGroupPython] Cs_element003  label="Cs_element : 003"  # scripted group (container) (typed FeaturePython)
  n = 1
  ref = Cs_element
FEATURE [App::DocumentObjectGroupPython] G4_Cs  # scripted group (container) (typed FeaturePython)
  Dunit = g/cm3
  Dvalue = 1.873
  Group = -> [Cs_element003]
  conduct = 2
  density = 1
  expand = 3
  formula = Cs
  name = G4_Cs
  specific = 4
FEATURE [App::DocumentObjectGroupPython] Ba_element003  label="Ba_element : 003"  # scripted group (container) (typed FeaturePython)
  n = 1
  ref = Ba_element
FEATURE [App::DocumentObjectGroupPython] G4_Ba  # scripted group (container) (typed FeaturePython)
  Dunit = g/cm3
  Dvalue = 3.5
  Group = -> [Ba_element003]
  conduct = 2
  density = 1
  expand = 3
  formula = Ba
  name = G4_Ba
  specific = 4
FEATURE [App::DocumentObjectGroupPython] La_element003  label="La_element : 003"  # scripted group (container) (typed FeaturePython)
  n = 1
  ref = La_element
FEATURE [App::DocumentObjectGroupPython] G4_La  # scripted group (container) (typed FeaturePython)
  Dunit = g/cm3
  Dvalue = 6.154
  Group = -> [La_element003]
  conduct = 2
  density = 1
  expand = 3
  formula = La
  name = G4_La
  specific = 4
FEATURE [App::DocumentObjectGroupPython] Ce_element002  label="Ce_element : 1"  # scripted group (container) (typed FeaturePython)
  n = 1
  ref = Ce_element
FEATURE [App::DocumentObjectGroupPython] G4_Ce  # scripted group (container) (typed FeaturePython)
  Dunit = g/cm3
  Dvalue = 6.657
  Group = -> [Ce_element002]
  conduct = 2
  density = 1
  expand = 3
  formula = Ce
  name = G4_Ce
  specific = 4
FEATURE [App::DocumentObjectGroupPython] Pr_element001  label="Pr_element : 1"  # scripted group (container) (typed FeaturePython)
  n = 1
  ref = Pr_element
FEATURE [App::DocumentObjectGroupPython] G4_Pr  # scripted group (container) (typed FeaturePython)
  Dunit = g/cm3
  Dvalue = 6.71
  Group = -> [Pr_element001]
  conduct = 2
  density = 1
  expand = 3
  formula = Pr
  name = G4_Pr
  specific = 4
FEATURE [App::DocumentObjectGroupPython] Nd_element001  label="Nd_element : 1"  # scripted group (container) (typed FeaturePython)
  n = 1
  ref = Nd_element
FEATURE [App::DocumentObjectGroupPython] G4_Nd  # scripted group (container) (typed FeaturePython)
  Dunit = g/cm3
  Dvalue = 6.9
  Group = -> [Nd_element001]
  conduct = 2
  density = 1
  expand = 3
  formula = Nd
  name = G4_Nd
  specific = 4
FEATURE [App::DocumentObjectGroupPython] Pm_element001  label="Pm_element : 1"  # scripted group (container) (typed FeaturePython)
  n = 1
  ref = Pm_element
FEATURE [App::DocumentObjectGroupPython] G4_Pm  # scripted group (container) (typed FeaturePython)
  Dunit = g/cm3
  Dvalue = 7.22
  Group = -> [Pm_element001]
  conduct = 2
  density = 1
  expand = 3
  formula = Pm
  name = G4_Pm
  specific = 4
FEATURE [App::DocumentObjectGroupPython] Sm_element001  label="Sm_element : 1"  # scripted group (container) (typed FeaturePython)
  n = 1
  ref = Sm_element
FEATURE [App::DocumentObjectGroupPython] G4_Sm  # scripted group (container) (typed FeaturePython)
  Dunit = g/cm3
  Dvalue = 7.46
  Group = -> [Sm_element001]
  conduct = 2
  density = 1
  expand = 3
  formula = Sm
  name = G4_Sm
  specific = 4
FEATURE [App::DocumentObjectGroupPython] Eu_element001  label="Eu_element : 1"  # scripted group (container) (typed FeaturePython)
  n = 1
  ref = Eu_element
FEATURE [App::DocumentObjectGroupPython] G4_Eu  # scripted group (container) (typed FeaturePython)
  Dunit = g/cm3
  Dvalue = 5.243
  Group = -> [Eu_element001]
  conduct = 2
  density = 1
  expand = 3
  formula = Eu
  name = G4_Eu
  specific = 4
FEATURE [App::DocumentObjectGroupPython] Gd_element002  label="Gd_element : 1"  # scripted group (container) (typed FeaturePython)
  n = 1
  ref = Gd_element
FEATURE [App::DocumentObjectGroupPython] G4_Gd  # scripted group (container) (typed FeaturePython)
  Dunit = g/cm3
  Dvalue = 7.9004
  Group = -> [Gd_element002]
  conduct = 2
  density = 1
  expand = 3
  formula = Gd
  name = G4_Gd
  specific = 4
FEATURE [App::DocumentObjectGroupPython] Tb_element001  label="Tb_element : 1"  # scripted group (container) (typed FeaturePython)
  n = 1
  ref = Tb_element
FEATURE [App::DocumentObjectGroupPython] G4_Tb  # scripted group (container) (typed FeaturePython)
  Dunit = g/cm3
  Dvalue = 8.229
  Group = -> [Tb_element001]
  conduct = 2
  density = 1
  expand = 3
  formula = Tb
  name = G4_Tb
  specific = 4
FEATURE [App::DocumentObjectGroupPython] Dy_element001  label="Dy_element : 1"  # scripted group (container) (typed FeaturePython)
  n = 1
  ref = Dy_element
FEATURE [App::DocumentObjectGroupPython] G4_Dy  # scripted group (container) (typed FeaturePython)
  Dunit = g/cm3
  Dvalue = 8.55
  Group = -> [Dy_element001]
  conduct = 2
  density = 1
  expand = 3
  formula = Dy
  name = G4_Dy
  specific = 4
FEATURE [App::DocumentObjectGroupPython] Ho_element001  label="Ho_element : 1"  # scripted group (container) (typed FeaturePython)
  n = 1
  ref = Ho_element
FEATURE [App::DocumentObjectGroupPython] G4_Ho  # scripted group (container) (typed FeaturePython)
  Dunit = g/cm3
  Dvalue = 8.795
  Group = -> [Ho_element001]
  conduct = 2
  density = 1
  expand = 3
  formula = Ho
  name = G4_Ho
  specific = 4
FEATURE [App::DocumentObjectGroupPython] Er_element001  label="Er_element : 1"  # scripted group (container) (typed FeaturePython)
  n = 1
  ref = Er_element
FEATURE [App::DocumentObjectGroupPython] G4_Er  # scripted group (container) (typed FeaturePython)
  Dunit = g/cm3
  Dvalue = 9.066
  Group = -> [Er_element001]
  conduct = 2
  density = 1
  expand = 3
  formula = Er
  name = G4_Er
  specific = 4
FEATURE [App::DocumentObjectGroupPython] Tm_element001  label="Tm_element : 1"  # scripted group (container) (typed FeaturePython)
  n = 1
  ref = Tm_element
FEATURE [App::DocumentObjectGroupPython] G4_Tm  # scripted group (container) (typed FeaturePython)
  Dunit = g/cm3
  Dvalue = 9.321
  Group = -> [Tm_element001]
  conduct = 2
  density = 1
  expand = 3
  formula = Tm
  name = G4_Tm
  specific = 4
FEATURE [App::DocumentObjectGroupPython] Yb_element001  label="Yb_element : 1"  # scripted group (container) (typed FeaturePython)
  n = 1
  ref = Yb_element
FEATURE [App::DocumentObjectGroupPython] G4_Yb  # scripted group (container) (typed FeaturePython)
  Dunit = g/cm3
  Dvalue = 6.73
  Group = -> [Yb_element001]
  conduct = 2
  density = 1
  expand = 3
  formula = Yb
  name = G4_Yb
  specific = 4
FEATURE [App::DocumentObjectGroupPython] Lu_element001  label="Lu_element : 1"  # scripted group (container) (typed FeaturePython)
  n = 1
  ref = Lu_element
FEATURE [App::DocumentObjectGroupPython] G4_Lu  # scripted group (container) (typed FeaturePython)
  Dunit = g/cm3
  Dvalue = 9.84
  Group = -> [Lu_element001]
  conduct = 2
  density = 1
  expand = 3
  formula = Lu
  name = G4_Lu
  specific = 4
FEATURE [App::DocumentObjectGroupPython] Hf_element001  label="Hf_element : 1"  # scripted group (container) (typed FeaturePython)
  n = 1
  ref = Hf_element
FEATURE [App::DocumentObjectGroupPython] G4_Hf  # scripted group (container) (typed FeaturePython)
  Dunit = g/cm3
  Dvalue = 13.31
  Group = -> [Hf_element001]
  conduct = 2
  density = 1
  expand = 3
  formula = Hf
  name = G4_Hf
  specific = 4
FEATURE [App::DocumentObjectGroupPython] Ta_element001  label="Ta_element : 1"  # scripted group (container) (typed FeaturePython)
  n = 1
  ref = Ta_element
FEATURE [App::DocumentObjectGroupPython] G4_Ta  # scripted group (container) (typed FeaturePython)
  Dunit = g/cm3
  Dvalue = 16.654
  Group = -> [Ta_element001]
  conduct = 2
  density = 1
  expand = 3
  formula = Ta
  name = G4_Ta
  specific = 4
FEATURE [App::DocumentObjectGroupPython] W_element004  label="W_element : 004"  # scripted group (container) (typed FeaturePython)
  n = 1
  ref = W_element
FEATURE [App::DocumentObjectGroupPython] G4_W  # scripted group (container) (typed FeaturePython)
  Dunit = g/cm3
  Dvalue = 19.3
  Group = -> [W_element004]
  conduct = 2
  density = 1
  expand = 3
  formula = W
  name = G4_W
  specific = 4
FEATURE [App::DocumentObjectGroupPython] Re_element001  label="Re_element : 1"  # scripted group (container) (typed FeaturePython)
  n = 1
  ref = Re_element
FEATURE [App::DocumentObjectGroupPython] G4_Re  # scripted group (container) (typed FeaturePython)
  Dunit = g/cm3
  Dvalue = 21.02
  Group = -> [Re_element001]
  conduct = 2
  density = 1
  expand = 3
  formula = Re
  name = G4_Re
  specific = 4
FEATURE [App::DocumentObjectGroupPython] Os_element001  label="Os_element : 1"  # scripted group (container) (typed FeaturePython)
  n = 1
  ref = Os_element
FEATURE [App::DocumentObjectGroupPython] G4_Os  # scripted group (container) (typed FeaturePython)
  Dunit = g/cm3
  Dvalue = 22.57
  Group = -> [Os_element001]
  conduct = 2
  density = 1
  expand = 3
  formula = Os
  name = G4_Os
  specific = 4
FEATURE [App::DocumentObjectGroupPython] Ir_element001  label="Ir_element : 1"  # scripted group (container) (typed FeaturePython)
  n = 1
  ref = Ir_element
FEATURE [App::DocumentObjectGroupPython] G4_Ir  # scripted group (container) (typed FeaturePython)
  Dunit = g/cm3
  Dvalue = 22.42
  Group = -> [Ir_element001]
  conduct = 2
  density = 1
  expand = 3
  formula = Ir
  name = G4_Ir
  specific = 4
FEATURE [App::DocumentObjectGroupPython] Pt_element001  label="Pt_element : 1"  # scripted group (container) (typed FeaturePython)
  n = 1
  ref = Pt_element
FEATURE [App::DocumentObjectGroupPython] G4_Pt  # scripted group (container) (typed FeaturePython)
  Dunit = g/cm3
  Dvalue = 21.45
  Group = -> [Pt_element001]
  conduct = 2
  density = 1
  expand = 3
  formula = Pt
  name = G4_Pt
  specific = 4
FEATURE [App::DocumentObjectGroupPython] Au_element001  label="Au_element : 1"  # scripted group (container) (typed FeaturePython)
  n = 1
  ref = Au_element
FEATURE [App::DocumentObjectGroupPython] G4_Au  # scripted group (container) (typed FeaturePython)
  Dunit = g/cm3
  Dvalue = 19.32
  Group = -> [Au_element001]
  conduct = 2
  density = 1
  expand = 3
  formula = Au
  name = G4_Au
  specific = 4
FEATURE [App::DocumentObjectGroupPython] Hg_element002  label="Hg_element : 002"  # scripted group (container) (typed FeaturePython)
  n = 1
  ref = Hg_element
FEATURE [App::DocumentObjectGroupPython] G4_Hg  # scripted group (container) (typed FeaturePython)
  Dunit = g/cm3
  Dvalue = 13.546
  Group = -> [Hg_element002]
  conduct = 2
  density = 1
  expand = 3
  formula = Hg
  name = G4_Hg
  specific = 4
FEATURE [App::DocumentObjectGroupPython] Tl_element002  label="Tl_element : 002"  # scripted group (container) (typed FeaturePython)
  n = 1
  ref = Tl_element
FEATURE [App::DocumentObjectGroupPython] G4_Tl  # scripted group (container) (typed FeaturePython)
  Dunit = g/cm3
  Dvalue = 11.72
  Group = -> [Tl_element002]
  conduct = 2
  density = 1
  expand = 3
  formula = Tl
  name = G4_Tl
  specific = 4
FEATURE [App::DocumentObjectGroupPython] Pb_element003  label="Pb_element : 1"  # scripted group (container) (typed FeaturePython)
  n = 1
  ref = Pb_element
FEATURE [App::DocumentObjectGroupPython] G4_Pb  # scripted group (container) (typed FeaturePython)
  Dunit = g/cm3
  Dvalue = 11.35
  Group = -> [Pb_element003]
  conduct = 2
  density = 1
  expand = 3
  formula = Pb
  name = G4_Pb
  specific = 4
FEATURE [App::DocumentObjectGroupPython] Bi_element002  label="Bi_element : 1"  # scripted group (container) (typed FeaturePython)
  n = 1
  ref = Bi_element
FEATURE [App::DocumentObjectGroupPython] G4_Bi  # scripted group (container) (typed FeaturePython)
  Dunit = g/cm3
  Dvalue = 9.747
  Group = -> [Bi_element002]
  conduct = 2
  density = 1
  expand = 3
  formula = Bi
  name = G4_Bi
  specific = 4
FEATURE [App::DocumentObjectGroupPython] Po_element001  label="Po_element : 1"  # scripted group (container) (typed FeaturePython)
  n = 1
  ref = Po_element
FEATURE [App::DocumentObjectGroupPython] G4_Po  # scripted group (container) (typed FeaturePython)
  Dunit = g/cm3
  Dvalue = 9.32
  Group = -> [Po_element001]
  conduct = 2
  density = 1
  expand = 3
  formula = Po
  name = G4_Po
  specific = 4
FEATURE [App::DocumentObjectGroupPython] At_element001  label="At_element : 1"  # scripted group (container) (typed FeaturePython)
  n = 1
  ref = At_element
FEATURE [App::DocumentObjectGroupPython] G4_At  # scripted group (container) (typed FeaturePython)
  Dunit = g/cm3
  Dvalue = 9.32
  Group = -> [At_element001]
  conduct = 2
  density = 1
  expand = 3
  formula = At
  name = G4_At
  specific = 4
FEATURE [App::DocumentObjectGroupPython] Rn_element001  label="Rn_element : 1"  # scripted group (container) (typed FeaturePython)
  n = 1
  ref = Rn_element
FEATURE [App::DocumentObjectGroupPython] G4_Rn  # scripted group (container) (typed FeaturePython)
  Dunit = g/cm3
  Dvalue = 0.00900662
  Group = -> [Rn_element001]
  conduct = 2
  density = 1
  expand = 3
  formula = Rn
  name = G4_Rn
  specific = 4
FEATURE [App::DocumentObjectGroupPython] Fr_element001  label="Fr_element : 1"  # scripted group (container) (typed FeaturePython)
  n = 1
  ref = Fr_element
FEATURE [App::DocumentObjectGroupPython] G4_Fr  # scripted group (container) (typed FeaturePython)
  Dunit = g/cm3
  Dvalue = 1
  Group = -> [Fr_element001]
  conduct = 2
  density = 1
  expand = 3
  formula = Fr
  name = G4_Fr
  specific = 4
FEATURE [App::DocumentObjectGroupPython] Ra_element001  label="Ra_element : 1"  # scripted group (container) (typed FeaturePython)
  n = 1
  ref = Ra_element
FEATURE [App::DocumentObjectGroupPython] G4_Ra  # scripted group (container) (typed FeaturePython)
  Dunit = g/cm3
  Dvalue = 5
  Group = -> [Ra_element001]
  conduct = 2
  density = 1
  expand = 3
  formula = Ra
  name = G4_Ra
  specific = 4
FEATURE [App::DocumentObjectGroupPython] Ac_element001  label="Ac_element : 1"  # scripted group (container) (typed FeaturePython)
  n = 1
  ref = Ac_element
FEATURE [App::DocumentObjectGroupPython] G4_Ac  # scripted group (container) (typed FeaturePython)
  Dunit = g/cm3
  Dvalue = 10.07
  Group = -> [Ac_element001]
  conduct = 2
  density = 1
  expand = 3
  formula = Ac
  name = G4_Ac
  specific = 4
FEATURE [App::DocumentObjectGroupPython] Th_element001  label="Th_element : 1"  # scripted group (container) (typed FeaturePython)
  n = 1
  ref = Th_element
FEATURE [App::DocumentObjectGroupPython] G4_Th  # scripted group (container) (typed FeaturePython)
  Dunit = g/cm3
  Dvalue = 11.72
  Group = -> [Th_element001]
  conduct = 2
  density = 1
  expand = 3
  formula = Th
  name = G4_Th
  specific = 4
FEATURE [App::DocumentObjectGroupPython] Pa_element001  label="Pa_element : 1"  # scripted group (container) (typed FeaturePython)
  n = 1
  ref = Pa_element
FEATURE [App::DocumentObjectGroupPython] G4_Pa  # scripted group (container) (typed FeaturePython)
  Dunit = g/cm3
  Dvalue = 15.37
  Group = -> [Pa_element001]
  conduct = 2
  density = 1
  expand = 3
  formula = Pa
  name = G4_Pa
  specific = 4
FEATURE [App::DocumentObjectGroupPython] U_element004  label="U_element : 004"  # scripted group (container) (typed FeaturePython)
  n = 1
  ref = U_element
FEATURE [App::DocumentObjectGroupPython] G4_U  # scripted group (container) (typed FeaturePython)
  Dunit = g/cm3
  Dvalue = 18.95
  Group = -> [U_element004]
  conduct = 2
  density = 1
  expand = 3
  formula = U
  name = G4_U
  specific = 4
FEATURE [App::DocumentObjectGroupPython] Np_element001  label="Np_element : 1"  # scripted group (container) (typed FeaturePython)
  n = 1
  ref = Np_element
FEATURE [App::DocumentObjectGroupPython] G4_Np  # scripted group (container) (typed FeaturePython)
  Dunit = g/cm3
  Dvalue = 20.25
  Group = -> [Np_element001]
  conduct = 2
  density = 1
  expand = 3
  formula = Np
  name = G4_Np
  specific = 4
FEATURE [App::DocumentObjectGroupPython] Pu_element002  label="Pu_element : 002"  # scripted group (container) (typed FeaturePython)
  n = 1
  ref = Pu_element
FEATURE [App::DocumentObjectGroupPython] G4_Pu  # scripted group (container) (typed FeaturePython)
  Dunit = g/cm3
  Dvalue = 19.84
  Group = -> [Pu_element002]
  conduct = 2
  density = 1
  expand = 3
  formula = Pu
  name = G4_Pu
  specific = 4
FEATURE [App::DocumentObjectGroupPython] Am_element001  label="Am_element : 1"  # scripted group (container) (typed FeaturePython)
  n = 1
  ref = Am_element
FEATURE [App::DocumentObjectGroupPython] G4_Am  # scripted group (container) (typed FeaturePython)
  Dunit = g/cm3
  Dvalue = 13.67
  Group = -> [Am_element001]
  conduct = 2
  density = 1
  expand = 3
  formula = Am
  name = G4_Am
  specific = 4
FEATURE [App::DocumentObjectGroupPython] Cm_element001  label="Cm_element : 1"  # scripted group (container) (typed FeaturePython)
  n = 1
  ref = Cm_element
FEATURE [App::DocumentObjectGroupPython] G4_Cm  # scripted group (container) (typed FeaturePython)
  Dunit = g/cm3
  Dvalue = 13.51
  Group = -> [Cm_element001]
  conduct = 2
  density = 1
  expand = 3
  formula = Cm
  name = G4_Cm
  specific = 4
FEATURE [App::DocumentObjectGroupPython] Bk_element001  label="Bk_element : 1"  # scripted group (container) (typed FeaturePython)
  n = 1
  ref = Bk_element
FEATURE [App::DocumentObjectGroupPython] G4_Bk  # scripted group (container) (typed FeaturePython)
  Dunit = g/cm3
  Dvalue = 14
  Group = -> [Bk_element001]
  conduct = 2
  density = 1
  expand = 3
  formula = Bk
  name = G4_Bk
  specific = 4
FEATURE [App::DocumentObjectGroupPython] Cf_element001  label="Cf_element : 1"  # scripted group (container) (typed FeaturePython)
  n = 1
  ref = Cf_element
FEATURE [App::DocumentObjectGroupPython] G4_Cf  # scripted group (container) (typed FeaturePython)
  Dunit = g/cm3
  Dvalue = 10
  Group = -> [Cf_element001]
  conduct = 2
  density = 1
  expand = 3
  formula = Cf
  name = G4_Cf
  specific = 4
FEATURE [App::DocumentObjectGroupPython] Element  # scripted group (container) (typed FeaturePython)
  Group = -> [G4_H,G4_He,G4_Li,G4_Be,G4_B,G4_C,G4_N,G4_O,G4_F,G4_Ne,G4_Na,G4_Mg,G4_Al,G4_Si,G4_P,G4_S,G4_Cl,G4_Ar,G4_K,G4_Ca,G4_Sc,G4_Ti,G4_V,G4_Cr,G4_Mn,G4_Fe,G4_Co,G4_Ni,G4_Cu,G4_Zn,G4_Ga,G4_Ge,G4_As,G4_Se,G4_Br,G4_Kr,G4_Rb,G4_Sr,G4_Y,G4_Zr,G4_Nb,G4_Mo,G4_Tc,G4_Ru,G4_Rh,G4_Pd,G4_Ag,G4_Cd,G4_In,G4_Sn,G4_Sb,G4_Te,G4_I,G4_Xe,G4_Cs,G4_Ba,G4_La,G4_Ce,G4_Pr,G4_Nd,G4_Pm,G4_Sm,G4_Eu,G4_Gd,G4_Tb,G4_Dy,G4_Ho,G4_Er,+30 more]
FEATURE [App::DocumentObjectGroupPython] H_element114  label="H_element : 063"  # scripted group (container) (typed FeaturePython)
  n = 2
  ref = H_element
FEATURE [App::DocumentObjectGroupPython] G4_lH2  # scripted group (container) (typed FeaturePython)
  Dunit = g/cm3
  Dvalue = 0.0708
  Group = -> [H_element114]
  conduct = 2
  density = 1
  expand = 3
  formula = G4_lH2
  name = G4_lH2
  specific = 4
FEATURE [App::DocumentObjectGroupPython] N_element049  label="N_element : 022"  # scripted group (container) (typed FeaturePython)
  n = 2
  ref = N_element
FEATURE [App::DocumentObjectGroupPython] G4_lN2  # scripted group (container) (typed FeaturePython)
  Dunit = g/cm3
  Dvalue = 0.807
  Group = -> [N_element049]
  conduct = 2
  density = 1
  expand = 3
  formula = G4_lN2
  name = G4_lN2
  specific = 4
FEATURE [App::DocumentObjectGroupPython] O_element106  label="O_element : 060"  # scripted group (container) (typed FeaturePython)
  n = 2
  ref = O_element
FEATURE [App::DocumentObjectGroupPython] G4_lO2  # scripted group (container) (typed FeaturePython)
  Dunit = g/cm3
  Dvalue = 1.141
  Group = -> [O_element106]
  conduct = 2
  density = 1
  expand = 3
  formula = G4_lO2
  name = G4_lO2
  specific = 4
FEATURE [App::DocumentObjectGroupPython] Ar  label="Ar : 1"  # scripted group (container) (typed FeaturePython)
  n = 1
  ref = Ar
FEATURE [App::DocumentObjectGroupPython] G4_lAr  # scripted group (container) (typed FeaturePython)
  Dunit = g/cm3
  Dvalue = 1.396
  Group = -> [Ar]
  conduct = 2
  density = 1
  expand = 3
  formula = G4_lAr
  name = G4_lAr
  specific = 4
FEATURE [App::DocumentObjectGroupPython] Br  label="Br : 1"  # scripted group (container) (typed FeaturePython)
  n = 1
  ref = Br
FEATURE [App::DocumentObjectGroupPython] G4_lBr  # scripted group (container) (typed FeaturePython)
  Dunit = g/cm3
  Dvalue = 3.1028
  Group = -> [Br]
  conduct = 2
  density = 1
  expand = 3
  formula = G4_lBr
  name = G4_lBr
  specific = 4
FEATURE [App::DocumentObjectGroupPython] Kr  label="Kr : 1"  # scripted group (container) (typed FeaturePython)
  n = 1
  ref = Kr
FEATURE [App::DocumentObjectGroupPython] G4_lKr  # scripted group (container) (typed FeaturePython)
  Dunit = g/cm3
  Dvalue = 2.418
  Group = -> [Kr]
  conduct = 2
  density = 1
  expand = 3
  formula = G4_lKr
  name = G4_lKr
  specific = 4
FEATURE [App::DocumentObjectGroupPython] Xe  label="Xe : 1"  # scripted group (container) (typed FeaturePython)
  n = 1
  ref = Xe
FEATURE [App::DocumentObjectGroupPython] G4_lXe  # scripted group (container) (typed FeaturePython)
  Dunit = g/cm3
  Dvalue = 2.953
  Group = -> [Xe]
  conduct = 2
  density = 1
  expand = 3
  formula = G4_lXe
  name = G4_lXe
  specific = 4
FEATURE [App::DocumentObjectGroupPython] O_element107  label="O_element : 061"  # scripted group (container) (typed FeaturePython)
  n = 4
  ref = O_element
FEATURE [App::DocumentObjectGroupPython] Pb_element004  label="Pb_element : 002"  # scripted group (container) (typed FeaturePython)
  n = 1
  ref = Pb_element
FEATURE [App::DocumentObjectGroupPython] W_element005  label="W_element : 005"  # scripted group (container) (typed FeaturePython)
  n = 1
  ref = W_element
FEATURE [App::DocumentObjectGroupPython] G4_PbWO4  # scripted group (container) (typed FeaturePython)
  Dunit = g/cm3
  Dvalue = 8.28
  Group = -> [O_element107,Pb_element004,W_element005]
  conduct = 2
  density = 1
  expand = 3
  formula = G4_PbWO4
  name = G4_PbWO4
  specific = 4
FEATURE [App::DocumentObjectGroupPython] alactic  label="alactic : 1"  # scripted group (container) (typed FeaturePython)
  n = 1
  ref = alactic
FEATURE [App::DocumentObjectGroupPython] G4_Galactic  # scripted group (container) (typed FeaturePython)
  Dunit = g/cm3
  Dvalue = 0
  Group = -> [alactic]
  conduct = 2
  density = 1
  expand = 3
  formula = G4_Galactic
  name = G4_Galactic
  specific = 4
FEATURE [App::DocumentObjectGroupPython] RAPHITE_POROUS  label="RAPHITE_POROUS : 1"  # scripted group (container) (typed FeaturePython)
  n = 1
  ref = RAPHITE_POROUS
FEATURE [App::DocumentObjectGroupPython] G4_GRAPHITE_POROUS  # scripted group (container) (typed FeaturePython)
  Dunit = g/cm3
  Dvalue = 1.7
  Group = -> [RAPHITE_POROUS]
  conduct = 2
  density = 1
  expand = 3
  formula = G4_GRAPHITE_POROUS
  name = G4_GRAPHITE_POROUS
  specific = 4
FEATURE [App::DocumentObjectGroupPython] H_element115  label="H_element : 0.150"  # scripted group (container) (typed FeaturePython)
  n = 0.080538
FEATURE [App::DocumentObjectGroupPython] C_element125  label="C_element : 0.600"  # scripted group (container) (typed FeaturePython)
  n = 0.599848
FEATURE [App::DocumentObjectGroupPython] O_element108  label="O_element : 0.320"  # scripted group (container) (typed FeaturePython)
  n = 0.319614
FEATURE [App::DocumentObjectGroupPython] G4_LUCITE  # scripted group (container) (typed FeaturePython)
  Dunit = g/cm3
  Dvalue = 1.19
  Group = -> [H_element115,C_element125,O_element108]
  conduct = 2
  density = 1
  expand = 3
  formula = G4_LUCITE
  name = G4_LUCITE
  specific = 4
FEATURE [App::DocumentObjectGroupPython] Cu_element002  label="Cu_element : 62"  # scripted group (container) (typed FeaturePython)
  n = 62
  ref = Cu_element
FEATURE [App::DocumentObjectGroupPython] Zn_element002  label="Zn_element : 35"  # scripted group (container) (typed FeaturePython)
  n = 35
  ref = Zn_element
FEATURE [App::DocumentObjectGroupPython] Pb_element005  label="Pb_element : 3"  # scripted group (container) (typed FeaturePython)
  n = 3
  ref = Pb_element
FEATURE [App::DocumentObjectGroupPython] G4_BRASS  # scripted group (container) (typed FeaturePython)
  Dunit = g/cm3
  Dvalue = 8.52
  Group = -> [Cu_element002,Zn_element002,Pb_element005]
  conduct = 2
  density = 1
  expand = 3
  formula = G4_BRASS
  name = G4_BRASS
  specific = 4
FEATURE [App::DocumentObjectGroupPython] Cu_element003  label="Cu_element : 89"  # scripted group (container) (typed FeaturePython)
  n = 89
  ref = Cu_element
FEATURE [App::DocumentObjectGroupPython] Zn_element003  label="Zn_element : 9"  # scripted group (container) (typed FeaturePython)
  n = 9
  ref = Zn_element
FEATURE [App::DocumentObjectGroupPython] Pb_element006  label="Pb_element : 2"  # scripted group (container) (typed FeaturePython)
  n = 2
  ref = Pb_element
FEATURE [App::DocumentObjectGroupPython] G4_BRONZE  # scripted group (container) (typed FeaturePython)
  Dunit = g/cm3
  Dvalue = 8.82
  Group = -> [Cu_element003,Zn_element003,Pb_element006]
  conduct = 2
  density = 1
  expand = 3
  formula = G4_BRONZE
  name = G4_BRONZE
  specific = 4
FEATURE [App::DocumentObjectGroupPython] Fe_element008  label="Fe_element : 74"  # scripted group (container) (typed FeaturePython)
  n = 74
  ref = Fe_element
FEATURE [App::DocumentObjectGroupPython] Cr_element002  label="Cr_element : 18"  # scripted group (container) (typed FeaturePython)
  n = 18
  ref = Cr_element
FEATURE [App::DocumentObjectGroupPython] Ni_element002  label="Ni_element : 8"  # scripted group (container) (typed FeaturePython)
  n = 8
  ref = Ni_element
FEATURE [App::DocumentObjectGroupPython] G4_STAINLESS_STEEL  label="G4_STAINLESS-STEEL"  # scripted group (container) (typed FeaturePython)
  Dunit = g/cm3
  Dvalue = 8
  Group = -> [Fe_element008,Cr_element002,Ni_element002]
  conduct = 2
  density = 1
  expand = 3
  formula = G4_STAINLESS-STEEL
  name = G4_STAINLESS-STEEL
  specific = 4
FEATURE [App::DocumentObjectGroupPython] H_element116  label="H_element : 064"  # scripted group (container) (typed FeaturePython)
  n = 18
  ref = H_element
FEATURE [App::DocumentObjectGroupPython] C_element126  label="C_element : 071"  # scripted group (container) (typed FeaturePython)
  n = 12
  ref = C_element
FEATURE [App::DocumentObjectGroupPython] O_element109  label="O_element : 062"  # scripted group (container) (typed FeaturePython)
  n = 7
  ref = O_element
FEATURE [App::DocumentObjectGroupPython] G4_CR39  # scripted group (container) (typed FeaturePython)
  Dunit = g/cm3
  Dvalue = 1.32
  Group = -> [H_element116,C_element126,O_element109]
  conduct = 2
  density = 1
  expand = 3
  formula = G4_CR39
  name = G4_CR39
  specific = 4
FEATURE [App::DocumentObjectGroupPython] H_element117  label="H_element : 38"  # scripted group (container) (typed FeaturePython)
  n = 38
  ref = H_element
FEATURE [App::DocumentObjectGroupPython] C_element127  label="C_element : 072"  # scripted group (container) (typed FeaturePython)
  n = 18
  ref = C_element
FEATURE [App::DocumentObjectGroupPython] O_element110  label="O_element : 063"  # scripted group (container) (typed FeaturePython)
  n = 1
  ref = O_element
FEATURE [App::DocumentObjectGroupPython] G4_OCTADECANOL  # scripted group (container) (typed FeaturePython)
  Dunit = g/cm3
  Dvalue = 0.812
  Group = -> [H_element117,C_element127,O_element110]
  conduct = 2
  density = 1
  expand = 3
  formula = G4_OCTADECANOL
  name = G4_OCTADECANOL
  specific = 4
FEATURE [App::DocumentObjectGroupPython] HEP  # scripted group (container) (typed FeaturePython)
  Group = -> [G4_lH2,G4_lN2,G4_lO2,G4_lAr,G4_lBr,G4_lKr,G4_lXe,G4_PbWO4,G4_Galactic,G4_GRAPHITE_POROUS,G4_LUCITE,G4_BRASS,G4_BRONZE,G4_STAINLESS_STEEL,G4_CR39,G4_OCTADECANOL]
FEATURE [App::DocumentObjectGroupPython] C_element128  label="C_element : 073"  # scripted group (container) (typed FeaturePython)
  n = 14
  ref = C_element
FEATURE [App::DocumentObjectGroupPython] H_element118  label="H_element : 065"  # scripted group (container) (typed FeaturePython)
  n = 10
  ref = H_element
FEATURE [App::DocumentObjectGroupPython] O_element111  label="O_element : 064"  # scripted group (container) (typed FeaturePython)
  n = 2
  ref = O_element
FEATURE [App::DocumentObjectGroupPython] N_element050  label="N_element : 023"  # scripted group (container) (typed FeaturePython)
  n = 2
  ref = N_element
FEATURE [App::DocumentObjectGroupPython] G4_KEVLAR  # scripted group (container) (typed FeaturePython)
  Dunit = g/cm3
  Dvalue = 1.44
  Group = -> [C_element128,H_element118,O_element111,N_element050]
  conduct = 2
  density = 1
  expand = 3
  formula = G4_KEVLAR
  name = G4_KEVLAR
  specific = 4
FEATURE [App::DocumentObjectGroupPython] C_element129  label="C_element : 074"  # scripted group (container) (typed FeaturePython)
  n = 10
  ref = C_element
FEATURE [App::DocumentObjectGroupPython] H_element119  label="H_element : 066"  # scripted group (container) (typed FeaturePython)
  n = 8
  ref = H_element
FEATURE [App::DocumentObjectGroupPython] O_element112  label="O_element : 065"  # scripted group (container) (typed FeaturePython)
  n = 4
  ref = O_element
FEATURE [App::DocumentObjectGroupPython] G4_DACRON  # scripted group (container) (typed FeaturePython)
  Dunit = g/cm3
  Dvalue = 1.4
  Group = -> [C_element129,H_element119,O_element112]
  conduct = 2
  density = 1
  expand = 3
  formula = G4_DACRON
  name = G4_DACRON
  specific = 4
FEATURE [App::DocumentObjectGroupPython] C_element130  label="C_element : 075"  # scripted group (container) (typed FeaturePython)
  n = 4
  ref = C_element
FEATURE [App::DocumentObjectGroupPython] H_element120  label="H_element : 067"  # scripted group (container) (typed FeaturePython)
  n = 5
  ref = H_element
FEATURE [App::DocumentObjectGroupPython] Cl_element030  label="Cl_element : 016"  # scripted group (container) (typed FeaturePython)
  n = 1
  ref = Cl_element
FEATURE [App::DocumentObjectGroupPython] G4_NEOPRENE  # scripted group (container) (typed FeaturePython)
  Dunit = g/cm3
  Dvalue = 1.23
  Group = -> [C_element130,H_element120,Cl_element030]
  conduct = 2
  density = 1
  expand = 3
  formula = G4_NEOPRENE
  name = G4_NEOPRENE
  specific = 4
FEATURE [App::DocumentObjectGroupPython] Space  # scripted group (container) (typed FeaturePython)
  Group = -> [G4_KEVLAR,G4_DACRON,G4_NEOPRENE]
FEATURE [App::DocumentObjectGroupPython] H_element121  label="H_element : 068"  # scripted group (container) (typed FeaturePython)
  n = 5
  ref = H_element
FEATURE [App::DocumentObjectGroupPython] C_element131  label="C_element : 076"  # scripted group (container) (typed FeaturePython)
  n = 4
  ref = C_element
FEATURE [App::DocumentObjectGroupPython] N_element051  label="N_element : 3"  # scripted group (container) (typed FeaturePython)
  n = 3
  ref = N_element
FEATURE [App::DocumentObjectGroupPython] O_element113  label="O_element : 066"  # scripted group (container) (typed FeaturePython)
  n = 1
  ref = O_element
FEATURE [App::DocumentObjectGroupPython] G4_CYTOSINE  # scripted group (container) (typed FeaturePython)
  Dunit = g/cm3
  Dvalue = 1.55
  Group = -> [H_element121,C_element131,N_element051,O_element113]
  conduct = 2
  density = 1
  expand = 3
  formula = G4_CYTOSINE
  name = G4_CYTOSINE
  specific = 4
FEATURE [App::DocumentObjectGroupPython] H_element122  label="H_element : 069"  # scripted group (container) (typed FeaturePython)
  n = 6
  ref = H_element
FEATURE [App::DocumentObjectGroupPython] C_element132  label="C_element : 077"  # scripted group (container) (typed FeaturePython)
  n = 5
  ref = C_element
FEATURE [App::DocumentObjectGroupPython] N_element052  label="N_element : 024"  # scripted group (container) (typed FeaturePython)
  n = 2
  ref = N_element
FEATURE [App::DocumentObjectGroupPython] O_element114  label="O_element : 067"  # scripted group (container) (typed FeaturePython)
  n = 2
  ref = O_element
FEATURE [App::DocumentObjectGroupPython] G4_THYMINE  # scripted group (container) (typed FeaturePython)
  Dunit = g/cm3
  Dvalue = 1.23
  Group = -> [H_element122,C_element132,N_element052,O_element114]
  conduct = 2
  density = 1
  expand = 3
  formula = G4_THYMINE
  name = G4_THYMINE
  specific = 4
FEATURE [App::DocumentObjectGroupPython] H_element123  label="H_element : 070"  # scripted group (container) (typed FeaturePython)
  n = 4
  ref = H_element
FEATURE [App::DocumentObjectGroupPython] C_element133  label="C_element : 078"  # scripted group (container) (typed FeaturePython)
  n = 4
  ref = C_element
FEATURE [App::DocumentObjectGroupPython] N_element053  label="N_element : 025"  # scripted group (container) (typed FeaturePython)
  n = 2
  ref = N_element
FEATURE [App::DocumentObjectGroupPython] O_element115  label="O_element : 068"  # scripted group (container) (typed FeaturePython)
  n = 2
  ref = O_element
FEATURE [App::DocumentObjectGroupPython] G4_URACIL  # scripted group (container) (typed FeaturePython)
  Dunit = g/cm3
  Dvalue = 1.32
  Group = -> [H_element123,C_element133,N_element053,O_element115]
  conduct = 2
  density = 1
  expand = 3
  formula = G4_URACIL
  name = G4_URACIL
  specific = 4
FEATURE [App::DocumentObjectGroupPython] H_element124  label="H_element : 071"  # scripted group (container) (typed FeaturePython)
  n = 4
  ref = H_element
FEATURE [App::DocumentObjectGroupPython] C_element134  label="C_element : 079"  # scripted group (container) (typed FeaturePython)
  n = 5
  ref = C_element
FEATURE [App::DocumentObjectGroupPython] N_element054  label="N_element : 026"  # scripted group (container) (typed FeaturePython)
  n = 5
  ref = N_element
FEATURE [App::DocumentObjectGroupPython] G4_DNA_ADENINE  # scripted group (container) (typed FeaturePython)
  Dunit = g/cm3
  Dvalue = 1
  Group = -> [H_element124,C_element134,N_element054]
  conduct = 2
  density = 1
  expand = 3
  formula = G4_DNA_ADENINE
  name = G4_DNA_ADENINE
  specific = 4
FEATURE [App::DocumentObjectGroupPython] H_element125  label="H_element : 072"  # scripted group (container) (typed FeaturePython)
  n = 4
  ref = H_element
FEATURE [App::DocumentObjectGroupPython] C_element135  label="C_element : 080"  # scripted group (container) (typed FeaturePython)
  n = 5
  ref = C_element
FEATURE [App::DocumentObjectGroupPython] N_element055  label="N_element : 027"  # scripted group (container) (typed FeaturePython)
  n = 5
  ref = N_element
FEATURE [App::DocumentObjectGroupPython] O_element116  label="O_element : 069"  # scripted group (container) (typed FeaturePython)
  n = 1
  ref = O_element
FEATURE [App::DocumentObjectGroupPython] G4_DNA_GUANINE  # scripted group (container) (typed FeaturePython)
  Dunit = g/cm3
  Dvalue = 1
  Group = -> [H_element125,C_element135,N_element055,O_element116]
  conduct = 2
  density = 1
  expand = 3
  formula = G4_DNA_GUANINE
  name = G4_DNA_GUANINE
  specific = 4
FEATURE [App::DocumentObjectGroupPython] H_element126  label="H_element : 073"  # scripted group (container) (typed FeaturePython)
  n = 4
  ref = H_element
FEATURE [App::DocumentObjectGroupPython] C_element136  label="C_element : 081"  # scripted group (container) (typed FeaturePython)
  n = 4
  ref = C_element
FEATURE [App::DocumentObjectGroupPython] N_element056  label="N_element : 028"  # scripted group (container) (typed FeaturePython)
  n = 3
  ref = N_element
FEATURE [App::DocumentObjectGroupPython] O_element117  label="O_element : 070"  # scripted group (container) (typed FeaturePython)
  n = 1
  ref = O_element
FEATURE [App::DocumentObjectGroupPython] G4_DNA_CYTOSINE  # scripted group (container) (typed FeaturePython)
  Dunit = g/cm3
  Dvalue = 1
  Group = -> [H_element126,C_element136,N_element056,O_element117]
  conduct = 2
  density = 1
  expand = 3
  formula = G4_DNA_CYTOSINE
  name = G4_DNA_CYTOSINE
  specific = 4
FEATURE [App::DocumentObjectGroupPython] H_element127  label="H_element : 074"  # scripted group (container) (typed FeaturePython)
  n = 5
  ref = H_element
FEATURE [App::DocumentObjectGroupPython] C_element137  label="C_element : 082"  # scripted group (container) (typed FeaturePython)
  n = 5
  ref = C_element
FEATURE [App::DocumentObjectGroupPython] N_element057  label="N_element : 029"  # scripted group (container) (typed FeaturePython)
  n = 2
  ref = N_element
FEATURE [App::DocumentObjectGroupPython] O_element118  label="O_element : 071"  # scripted group (container) (typed FeaturePython)
  n = 2
  ref = O_element
FEATURE [App::DocumentObjectGroupPython] G4_DNA_THYMINE  # scripted group (container) (typed FeaturePython)
  Dunit = g/cm3
  Dvalue = 1
  Group = -> [H_element127,C_element137,N_element057,O_element118]
  conduct = 2
  density = 1
  expand = 3
  formula = G4_DNA_THYMINE
  name = G4_DNA_THYMINE
  specific = 4
FEATURE [App::DocumentObjectGroupPython] H_element128  label="H_element : 075"  # scripted group (container) (typed FeaturePython)
  n = 3
  ref = H_element
FEATURE [App::DocumentObjectGroupPython] C_element138  label="C_element : 083"  # scripted group (container) (typed FeaturePython)
  n = 4
  ref = C_element
FEATURE [App::DocumentObjectGroupPython] N_element058  label="N_element : 030"  # scripted group (container) (typed FeaturePython)
  n = 2
  ref = N_element
FEATURE [App::DocumentObjectGroupPython] O_element119  label="O_element : 072"  # scripted group (container) (typed FeaturePython)
  n = 2
  ref = O_element
FEATURE [App::DocumentObjectGroupPython] G4_DNA_URACIL  # scripted group (container) (typed FeaturePython)
  Dunit = g/cm3
  Dvalue = 1
  Group = -> [H_element128,C_element138,N_element058,O_element119]
  conduct = 2
  density = 1
  expand = 3
  formula = G4_DNA_URACIL
  name = G4_DNA_URACIL
  specific = 4
FEATURE [App::DocumentObjectGroupPython] H_element129  label="H_element : 076"  # scripted group (container) (typed FeaturePython)
  n = 10
  ref = H_element
FEATURE [App::DocumentObjectGroupPython] C_element139  label="C_element : 084"  # scripted group (container) (typed FeaturePython)
  n = 10
  ref = C_element
FEATURE [App::DocumentObjectGroupPython] N_element059  label="N_element : 031"  # scripted group (container) (typed FeaturePython)
  n = 5
  ref = N_element
FEATURE [App::DocumentObjectGroupPython] O_element120  label="O_element : 073"  # scripted group (container) (typed FeaturePython)
  n = 4
  ref = O_element
FEATURE [App::DocumentObjectGroupPython] G4_DNA_ADENOSINE  # scripted group (container) (typed FeaturePython)
  Dunit = g/cm3
  Dvalue = 1
  Group = -> [H_element129,C_element139,N_element059,O_element120]
  conduct = 2
  density = 1
  expand = 3
  formula = G4_DNA_ADENOSINE
  name = G4_DNA_ADENOSINE
  specific = 4
FEATURE [App::DocumentObjectGroupPython] H_element130  label="H_element : 077"  # scripted group (container) (typed FeaturePython)
  n = 10
  ref = H_element
FEATURE [App::DocumentObjectGroupPython] C_element140  label="C_element : 085"  # scripted group (container) (typed FeaturePython)
  n = 10
  ref = C_element
FEATURE [App::DocumentObjectGroupPython] N_element060  label="N_element : 032"  # scripted group (container) (typed FeaturePython)
  n = 5
  ref = N_element
FEATURE [App::DocumentObjectGroupPython] O_element121  label="O_element : 074"  # scripted group (container) (typed FeaturePython)
  n = 5
  ref = O_element
FEATURE [App::DocumentObjectGroupPython] G4_DNA_GUANOSINE  # scripted group (container) (typed FeaturePython)
  Dunit = g/cm3
  Dvalue = 1
  Group = -> [H_element130,C_element140,N_element060,O_element121]
  conduct = 2
  density = 1
  expand = 3
  formula = G4_DNA_GUANOSINE
  name = G4_DNA_GUANOSINE
  specific = 4
FEATURE [App::DocumentObjectGroupPython] H_element131  label="H_element : 078"  # scripted group (container) (typed FeaturePython)
  n = 10
  ref = H_element
FEATURE [App::DocumentObjectGroupPython] C_element141  label="C_element : 086"  # scripted group (container) (typed FeaturePython)
  n = 9
  ref = C_element
FEATURE [App::DocumentObjectGroupPython] N_element061  label="N_element : 033"  # scripted group (container) (typed FeaturePython)
  n = 3
  ref = N_element
FEATURE [App::DocumentObjectGroupPython] O_element122  label="O_element : 075"  # scripted group (container) (typed FeaturePython)
  n = 5
  ref = O_element
FEATURE [App::DocumentObjectGroupPython] G4_DNA_CYTIDINE  # scripted group (container) (typed FeaturePython)
  Dunit = g/cm3
  Dvalue = 1
  Group = -> [H_element131,C_element141,N_element061,O_element122]
  conduct = 2
  density = 1
  expand = 3
  formula = G4_DNA_CYTIDINE
  name = G4_DNA_CYTIDINE
  specific = 4
FEATURE [App::DocumentObjectGroupPython] H_element132  label="H_element : 079"  # scripted group (container) (typed FeaturePython)
  n = 9
  ref = H_element
FEATURE [App::DocumentObjectGroupPython] C_element142  label="C_element : 087"  # scripted group (container) (typed FeaturePython)
  n = 9
  ref = C_element
FEATURE [App::DocumentObjectGroupPython] N_element062  label="N_element : 034"  # scripted group (container) (typed FeaturePython)
  n = 2
  ref = N_element
FEATURE [App::DocumentObjectGroupPython] O_element123  label="O_element : 076"  # scripted group (container) (typed FeaturePython)
  n = 6
  ref = O_element
FEATURE [App::DocumentObjectGroupPython] G4_DNA_URIDINE  # scripted group (container) (typed FeaturePython)
  Dunit = g/cm3
  Dvalue = 1
  Group = -> [H_element132,C_element142,N_element062,O_element123]
  conduct = 2
  density = 1
  expand = 3
  formula = G4_DNA_URIDINE
  name = G4_DNA_URIDINE
  specific = 4
FEATURE [App::DocumentObjectGroupPython] H_element133  label="H_element : 080"  # scripted group (container) (typed FeaturePython)
  n = 11
  ref = H_element
FEATURE [App::DocumentObjectGroupPython] C_element143  label="C_element : 088"  # scripted group (container) (typed FeaturePython)
  n = 10
  ref = C_element
FEATURE [App::DocumentObjectGroupPython] N_element063  label="N_element : 035"  # scripted group (container) (typed FeaturePython)
  n = 2
  ref = N_element
FEATURE [App::DocumentObjectGroupPython] O_element124  label="O_element : 077"  # scripted group (container) (typed FeaturePython)
  n = 6
  ref = O_element
FEATURE [App::DocumentObjectGroupPython] G4_DNA_METHYLURIDINE  # scripted group (container) (typed FeaturePython)
  Dunit = g/cm3
  Dvalue = 1
  Group = -> [H_element133,C_element143,N_element063,O_element124]
  conduct = 2
  density = 1
  expand = 3
  formula = G4_DNA_METHYLURIDINE
  name = G4_DNA_METHYLURIDINE
  specific = 4
FEATURE [App::DocumentObjectGroupPython] P_element014  label="P_element : 003"  # scripted group (container) (typed FeaturePython)
  n = 1
  ref = P_element
FEATURE [App::DocumentObjectGroupPython] O_element125  label="O_element : 078"  # scripted group (container) (typed FeaturePython)
  n = 3
  ref = O_element
FEATURE [App::DocumentObjectGroupPython] G4_DNA_MONOPHOSPHATE  # scripted group (container) (typed FeaturePython)
  Dunit = g/cm3
  Dvalue = 1
  Group = -> [P_element014,O_element125]
  conduct = 2
  density = 1
  expand = 3
  formula = G4_DNA_MONOPHOSPHATE
  name = G4_DNA_MONOPHOSPHATE
  specific = 4
FEATURE [App::DocumentObjectGroupPython] H_element134  label="H_element : 081"  # scripted group (container) (typed FeaturePython)
  n = 10
  ref = H_element
FEATURE [App::DocumentObjectGroupPython] C_element144  label="C_element : 089"  # scripted group (container) (typed FeaturePython)
  n = 10
  ref = C_element
FEATURE [App::DocumentObjectGroupPython] N_element064  label="N_element : 036"  # scripted group (container) (typed FeaturePython)
  n = 5
  ref = N_element
FEATURE [App::DocumentObjectGroupPython] O_element126  label="O_element : 079"  # scripted group (container) (typed FeaturePython)
  n = 7
  ref = O_element
FEATURE [App::DocumentObjectGroupPython] P_element015  label="P_element : 004"  # scripted group (container) (typed FeaturePython)
  n = 1
  ref = P_element
FEATURE [App::DocumentObjectGroupPython] G4_DNA_A  # scripted group (container) (typed FeaturePython)
  Dunit = g/cm3
  Dvalue = 1
  Group = -> [H_element134,C_element144,N_element064,O_element126,P_element015]
  conduct = 2
  density = 1
  expand = 3
  formula = G4_DNA_A
  name = G4_DNA_A
  specific = 4
FEATURE [App::DocumentObjectGroupPython] H_element135  label="H_element : 082"  # scripted group (container) (typed FeaturePython)
  n = 10
  ref = H_element
FEATURE [App::DocumentObjectGroupPython] C_element145  label="C_element : 090"  # scripted group (container) (typed FeaturePython)
  n = 10
  ref = C_element
FEATURE [App::DocumentObjectGroupPython] N_element065  label="N_element : 037"  # scripted group (container) (typed FeaturePython)
  n = 5
  ref = N_element
FEATURE [App::DocumentObjectGroupPython] O_element127  label="O_element : 8"  # scripted group (container) (typed FeaturePython)
  n = 8
  ref = O_element
FEATURE [App::DocumentObjectGroupPython] P_element016  label="P_element : 005"  # scripted group (container) (typed FeaturePython)
  n = 1
  ref = P_element
FEATURE [App::DocumentObjectGroupPython] G4_DNA_G  # scripted group (container) (typed FeaturePython)
  Dunit = g/cm3
  Dvalue = 1
  Group = -> [H_element135,C_element145,N_element065,O_element127,P_element016]
  conduct = 2
  density = 1
  expand = 3
  formula = G4_DNA_G
  name = G4_DNA_G
  specific = 4
FEATURE [App::DocumentObjectGroupPython] H_element136  label="H_element : 083"  # scripted group (container) (typed FeaturePython)
  n = 10
  ref = H_element
FEATURE [App::DocumentObjectGroupPython] C_element146  label="C_element : 091"  # scripted group (container) (typed FeaturePython)
  n = 9
  ref = C_element
FEATURE [App::DocumentObjectGroupPython] N_element066  label="N_element : 038"  # scripted group (container) (typed FeaturePython)
  n = 3
  ref = N_element
FEATURE [App::DocumentObjectGroupPython] O_element128  label="O_element : 080"  # scripted group (container) (typed FeaturePython)
  n = 8
  ref = O_element
FEATURE [App::DocumentObjectGroupPython] P_element017  label="P_element : 006"  # scripted group (container) (typed FeaturePython)
  n = 1
  ref = P_element
FEATURE [App::DocumentObjectGroupPython] G4_DNA_C  # scripted group (container) (typed FeaturePython)
  Dunit = g/cm3
  Dvalue = 1
  Group = -> [H_element136,C_element146,N_element066,O_element128,P_element017]
  conduct = 2
  density = 1
  expand = 3
  formula = G4_DNA_C
  name = G4_DNA_C
  specific = 4
FEATURE [App::DocumentObjectGroupPython] H_element137  label="H_element : 084"  # scripted group (container) (typed FeaturePython)
  n = 9
  ref = H_element
FEATURE [App::DocumentObjectGroupPython] C_element147  label="C_element : 092"  # scripted group (container) (typed FeaturePython)
  n = 9
  ref = C_element
FEATURE [App::DocumentObjectGroupPython] N_element067  label="N_element : 039"  # scripted group (container) (typed FeaturePython)
  n = 2
  ref = N_element
FEATURE [App::DocumentObjectGroupPython] O_element129  label="O_element : 9"  # scripted group (container) (typed FeaturePython)
  n = 9
  ref = O_element
FEATURE [App::DocumentObjectGroupPython] P_element018  label="P_element : 007"  # scripted group (container) (typed FeaturePython)
  n = 1
  ref = P_element
FEATURE [App::DocumentObjectGroupPython] G4_DNA_U  # scripted group (container) (typed FeaturePython)
  Dunit = g/cm3
  Dvalue = 1
  Group = -> [H_element137,C_element147,N_element067,O_element129,P_element018]
  conduct = 2
  density = 1
  expand = 3
  formula = G4_DNA_U
  name = G4_DNA_U
  specific = 4
FEATURE [App::DocumentObjectGroupPython] H_element138  label="H_element : 085"  # scripted group (container) (typed FeaturePython)
  n = 11
  ref = H_element
FEATURE [App::DocumentObjectGroupPython] C_element148  label="C_element : 093"  # scripted group (container) (typed FeaturePython)
  n = 10
  ref = C_element
FEATURE [App::DocumentObjectGroupPython] N_element068  label="N_element : 040"  # scripted group (container) (typed FeaturePython)
  n = 2
  ref = N_element
FEATURE [App::DocumentObjectGroupPython] O_element130  label="O_element : 081"  # scripted group (container) (typed FeaturePython)
  n = 9
  ref = O_element
FEATURE [App::DocumentObjectGroupPython] P_element019  label="P_element : 008"  # scripted group (container) (typed FeaturePython)
  n = 1
  ref = P_element
FEATURE [App::DocumentObjectGroupPython] G4_DNA_MU  # scripted group (container) (typed FeaturePython)
  Dunit = g/cm3
  Dvalue = 1
  Group = -> [H_element138,C_element148,N_element068,O_element130,P_element019]
  conduct = 2
  density = 1
  expand = 3
  formula = G4_DNA_MU
  name = G4_DNA_MU
  specific = 4
FEATURE [App::DocumentObjectGroupPython] BioChemical  # scripted group (container) (typed FeaturePython)
  Group = -> [G4_CYTOSINE,G4_THYMINE,G4_URACIL,G4_DNA_ADENINE,G4_DNA_GUANINE,G4_DNA_CYTOSINE,G4_DNA_THYMINE,G4_DNA_URACIL,G4_DNA_ADENOSINE,G4_DNA_GUANOSINE,G4_DNA_CYTIDINE,G4_DNA_URIDINE,G4_DNA_METHYLURIDINE,G4_DNA_MONOPHOSPHATE,G4_DNA_A,G4_DNA_G,G4_DNA_C,G4_DNA_U,G4_DNA_MU]
FEATURE [App::DocumentObjectGroupPython] G4Materials  # scripted group (container) (typed FeaturePython)
  Group = -> [NIST,Element,HEP,Space,BioChemical]
  version = 1
FEATURE [App::DocumentObjectGroupPython] Geant4  # scripted group (container) (typed FeaturePython)
  Group = -> [G4Isotopes,G4Elements,G4Materials]
FEATURE [App::DocumentObjectGroupPython] Materials  # scripted group (container) (typed FeaturePython)
  Group = -> [Geant4]
FEATURE [Part::FeaturePython] GDMLBox_WorldBox  # WARN: FeaturePython — macro-defined, semantics opaque (R4)
  lunit = 2
  material = 5
  x = 100
  y = 100
  z = 100
FEATURE [Part::Box] Box  label="Cube"
  AttacherType = Attacher::AttachEngine3D
  Height = 5
  Length = 5
  Placement = pos=(5,0,0) rot=(0,0,1;0rad)
  Width = 5
FEATURE [Part::FeaturePython] Array001  # Draft array (typed FeaturePython)
  Angle = 360
  ArrayType = 0
  Axis = (0,0,1)
  Base = -> Box
  Center = (0,0,0)
  Count = 4
  Fuse = false
  IntervalAxis = (0,0,0)
  IntervalX = (50,0,0)
  IntervalY = (0,30,0)
  IntervalZ = (0,0,100)
  NumberCircles = 3
  NumberPolar = 5
  NumberX = 2
  NumberY = 2
  NumberZ = 1
  Placement = pos=(-20,-14,0) rot=(0,0,1;0rad)
  RadialDistance = 50
  Symmetry = 1
  TangentialDistance = 25
FEATURE [App::Part] Part
  Group = -> [Array001]
  Origin = -> Origin002
FEATURE [App::Part] worldVOL
  Group = -> [GDMLBox_WorldBox,Part]
  Origin = -> Origin
